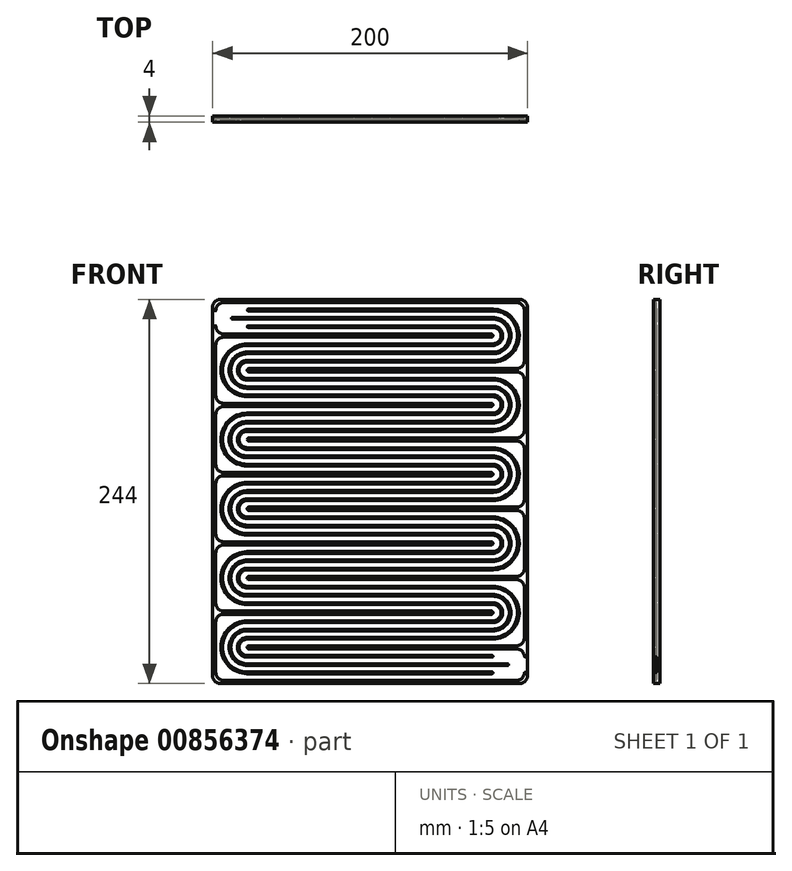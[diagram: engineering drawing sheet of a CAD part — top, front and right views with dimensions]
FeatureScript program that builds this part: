
annotation { "Feature Type Name" : "Feature", "Feature Type Description" : "" }
export const myFeature = defineFeature(function(context is Context, id is Id, definition is map)
    precondition{}
    {
        {
            var Q0;
            Q0=qCreatedBy(makeId("Front.planeOp"),FACE);
            var sketch = newSketch(context, id + "F0", { "sketchPlane" : qUnion([Q0])});
            skLineSegment(sketch, "E0.bottom", {"start": v(5, 0) * mm, "end": v(195, 0) * mm});
            skLineSegment(sketch, "E0.top", {"start": v(5, 244) * mm, "end": v(195, 244) * mm});
            skLineSegment(sketch, "E0.left", {"start": v(0, 5) * mm, "end": v(0, 239) * mm});
            skLineSegment(sketch, "E0.right", {"start": v(200, 5) * mm, "end": v(200, 239) * mm});
            skPoint(sketch, "E1.visualSharp", {"position": v(0, 244) * mm});
            skArc(sketch, "E1.filletArc", {"start": v(5, 244) * mm, "mid": v(1.46, 242.54) * mm, "end": v(0, 239) * mm});
            skPoint(sketch, "E2.visualSharp", {"position": v(200, 244) * mm});
            skArc(sketch, "E2.filletArc", {"start": v(200, 239) * mm, "mid": v(198.54, 242.54) * mm, "end": v(195, 244) * mm});
            skPoint(sketch, "E3.visualSharp", {"position": v(200, 0) * mm});
            skArc(sketch, "E3.filletArc", {"start": v(195, 0) * mm, "mid": v(198.54, 1.46) * mm, "end": v(200, 5) * mm});
            skPoint(sketch, "E4.visualSharp", {"position": v(0, 0) * mm});
            skArc(sketch, "E4.filletArc", {"start": v(0, 5) * mm, "mid": v(1.46, 1.46) * mm, "end": v(5, 0) * mm});
            skSolve(sketch);
        }
        {
            var Q0;
            Q0 = qSketchRegion(id + "F0", true);
            extrude(context, id + "F1", {"entities" : qUnion([Q0]), "depth" : 4 * mm, "offsetDistance" : 25 * mm});
        }
        {
            var Q0;
            Q0=makeQuery(id+"F1.opExtrude","CAP_FACE",FACE,{"disambiguationData":[OSD([sQuery(id+"F0.wireOp",EDGE,"E0.bottom"),sQuery(id+"F0.wireOp",EDGE,"E0.top"),sQuery(id+"F0.wireOp",EDGE,"E0.left"),sQuery(id+"F0.wireOp",EDGE,"E0.right"),sQuery(id+"F0.wireOp",EDGE,"E1.filletArc"),sQuery(id+"F0.wireOp",EDGE,"E2.filletArc"),sQuery(id+"F0.wireOp",EDGE,"E3.filletArc"),sQuery(id+"F0.wireOp",EDGE,"E4.filletArc")])],"isStart":false});
            var sketch = newSketch(context, id + "F2", { "sketchPlane" : qUnion([Q0])});
            skLineSegment(sketch, "E5.bottom", {"start": v(7, 242) * mm, "end": v(193, 242) * mm});
            skLineSegment(sketch, "E5.top", {"start": v(7, 2) * mm, "end": v(193, 2) * mm});
            skLineSegment(sketch, "E5.right", {"start": v(198, 237) * mm, "end": v(198, 205) * mm});
            skPoint(sketch, "E6.visualSharp", {"position": v(2, 242) * mm});
            skArc(sketch, "E6.filletArc", {"start": v(7, 242) * mm, "mid": v(3.46, 240.54) * mm, "end": v(2, 237) * mm});
            skPoint(sketch, "E7.visualSharp", {"position": v(198, 242) * mm});
            skArc(sketch, "E7.filletArc", {"start": v(198, 237) * mm, "mid": v(196.54, 240.54) * mm, "end": v(193, 242) * mm});
            skLineSegment(sketch, "E8.bottom", {"start": v(7, 46) * mm, "end": v(177, 46) * mm});
            skLineSegment(sketch, "E8.top", {"start": v(6.8, 44) * mm, "end": v(177, 44) * mm});
            skLineSegment(sketch, "E8.right", {"start": v(178, 45) * mm, "end": v(178, 45) * mm});
            skLineSegment(sketch, "E9.bottom", {"start": v(193, 24) * mm, "end": v(23, 24) * mm});
            skLineSegment(sketch, "E9.top", {"start": v(193, 22) * mm, "end": v(23, 22) * mm});
            skLineSegment(sketch, "E9.right", {"start": v(22, 23) * mm, "end": v(22, 23) * mm});
            skPoint(sketch, "E10.visualSharp", {"position": v(178, 46) * mm});
            skArc(sketch, "E10.filletArc", {"start": v(178, 45) * mm, "mid": v(177.7, 45.7) * mm, "end": v(177, 46) * mm});
            skPoint(sketch, "E11.visualSharp", {"position": v(178, 44) * mm});
            skArc(sketch, "E11.filletArc", {"start": v(177, 44) * mm, "mid": v(177.7, 44.3) * mm, "end": v(178, 45) * mm});
            skPoint(sketch, "E12.visualSharp", {"position": v(22, 24) * mm});
            skArc(sketch, "E12.filletArc", {"start": v(23, 24) * mm, "mid": v(22.3, 23.7) * mm, "end": v(22, 23) * mm});
            skPoint(sketch, "E13.visualSharp", {"position": v(22, 22) * mm});
            skArc(sketch, "E13.filletArc", {"start": v(22, 23) * mm, "mid": v(22.3, 22.3) * mm, "end": v(23, 22) * mm});
            skLineSegment(sketch, "E14.0.1.0", {"start": v(7, 88) * mm, "end": v(177, 88) * mm});
            skLineSegment(sketch, "E14.0.1.1", {"start": v(193, 68) * mm, "end": v(23, 68) * mm});
            skPoint(sketch, "E14.0.1.2", {"position": v(22, 68) * mm});
            skLineSegment(sketch, "E14.0.1.3", {"start": v(193, 66) * mm, "end": v(23, 66) * mm});
            skLineSegment(sketch, "E14.0.1.4", {"start": v(7, 90) * mm, "end": v(177, 90) * mm});
            skPoint(sketch, "E14.0.1.5", {"position": v(178, 90) * mm});
            skPoint(sketch, "E14.0.1.6", {"position": v(22, 66) * mm});
            skPoint(sketch, "E14.0.1.7", {"position": v(178, 88) * mm});
            skArc(sketch, "E14.0.1.10", {"start": v(22, 67) * mm, "mid": v(22.3, 66.3) * mm, "end": v(23, 66) * mm});
            skArc(sketch, "E14.0.1.11", {"start": v(23, 68) * mm, "mid": v(22.3, 67.7) * mm, "end": v(22, 67) * mm});
            skArc(sketch, "E14.0.1.12", {"start": v(177, 88) * mm, "mid": v(177.7, 88.3) * mm, "end": v(178, 89) * mm});
            skArc(sketch, "E14.0.1.13", {"start": v(178, 89) * mm, "mid": v(177.7, 89.7) * mm, "end": v(177, 90) * mm});
            skLineSegment(sketch, "E14.0.2.0", {"start": v(7, 132) * mm, "end": v(177, 132) * mm});
            skLineSegment(sketch, "E14.0.2.1", {"start": v(193, 112) * mm, "end": v(23, 112) * mm});
            skPoint(sketch, "E14.0.2.2", {"position": v(22, 112) * mm});
            skLineSegment(sketch, "E14.0.2.3", {"start": v(193, 110) * mm, "end": v(23, 110) * mm});
            skLineSegment(sketch, "E14.0.2.4", {"start": v(7, 134) * mm, "end": v(177, 134) * mm});
            skPoint(sketch, "E14.0.2.5", {"position": v(178, 134) * mm});
            skPoint(sketch, "E14.0.2.6", {"position": v(22, 110) * mm});
            skPoint(sketch, "E14.0.2.7", {"position": v(178, 132) * mm});
            skArc(sketch, "E14.0.2.10", {"start": v(22, 111) * mm, "mid": v(22.3, 110.3) * mm, "end": v(23, 110) * mm});
            skArc(sketch, "E14.0.2.11", {"start": v(23, 112) * mm, "mid": v(22.3, 111.7) * mm, "end": v(22, 111) * mm});
            skArc(sketch, "E14.0.2.12", {"start": v(177, 132) * mm, "mid": v(177.7, 132.3) * mm, "end": v(178, 133) * mm});
            skArc(sketch, "E14.0.2.13", {"start": v(178, 133) * mm, "mid": v(177.7, 133.7) * mm, "end": v(177, 134) * mm});
            skLineSegment(sketch, "E14.0.3.0", {"start": v(7, 176) * mm, "end": v(177, 176) * mm});
            skLineSegment(sketch, "E14.0.3.1", {"start": v(193, 156) * mm, "end": v(23, 156) * mm});
            skPoint(sketch, "E14.0.3.2", {"position": v(22, 156) * mm});
            skLineSegment(sketch, "E14.0.3.3", {"start": v(193, 154) * mm, "end": v(23, 154) * mm});
            skLineSegment(sketch, "E14.0.3.4", {"start": v(7, 178) * mm, "end": v(177, 178) * mm});
            skPoint(sketch, "E14.0.3.5", {"position": v(178, 178) * mm});
            skPoint(sketch, "E14.0.3.6", {"position": v(22, 154) * mm});
            skPoint(sketch, "E14.0.3.7", {"position": v(178, 176) * mm});
            skArc(sketch, "E14.0.3.10", {"start": v(22, 155) * mm, "mid": v(22.3, 154.3) * mm, "end": v(23, 154) * mm});
            skArc(sketch, "E14.0.3.11", {"start": v(23, 156) * mm, "mid": v(22.3, 155.7) * mm, "end": v(22, 155) * mm});
            skArc(sketch, "E14.0.3.12", {"start": v(177, 176) * mm, "mid": v(177.7, 176.3) * mm, "end": v(178, 177) * mm});
            skArc(sketch, "E14.0.3.13", {"start": v(178, 177) * mm, "mid": v(177.7, 177.7) * mm, "end": v(177, 178) * mm});
            skLineSegment(sketch, "E14.0.4.0", {"start": v(7, 220) * mm, "end": v(177, 220) * mm});
            skLineSegment(sketch, "E14.0.4.1", {"start": v(193, 200) * mm, "end": v(23, 200) * mm});
            skPoint(sketch, "E14.0.4.2", {"position": v(22, 200) * mm});
            skLineSegment(sketch, "E14.0.4.3", {"start": v(193, 198) * mm, "end": v(23, 198) * mm});
            skLineSegment(sketch, "E14.0.4.4", {"start": v(7, 222) * mm, "end": v(177, 222) * mm});
            skPoint(sketch, "E14.0.4.5", {"position": v(178, 222) * mm});
            skPoint(sketch, "E14.0.4.6", {"position": v(22, 198) * mm});
            skPoint(sketch, "E14.0.4.7", {"position": v(178, 220) * mm});
            skArc(sketch, "E14.0.4.10", {"start": v(22, 199) * mm, "mid": v(22.3, 198.3) * mm, "end": v(23, 198) * mm});
            skArc(sketch, "E14.0.4.11", {"start": v(23, 200) * mm, "mid": v(22.3, 199.7) * mm, "end": v(22, 199) * mm});
            skArc(sketch, "E14.0.4.12", {"start": v(177, 220) * mm, "mid": v(177.7, 220.3) * mm, "end": v(178, 221) * mm});
            skArc(sketch, "E14.0.4.13", {"start": v(178, 221) * mm, "mid": v(177.7, 221.7) * mm, "end": v(177, 222) * mm});
            skLineSegment(sketch, "E14.direction1", {"start": v(22, 22) * mm, "end": v(47, 22) * mm, "construction": true});
            skLineSegment(sketch, "E14.direction2", {"start": v(22, 22) * mm, "end": v(22, 66) * mm, "construction": true});
            skLineSegment(sketch, "E15.trimOffspring", {"start": v(2, 215) * mm, "end": v(2, 183) * mm});
            skLineSegment(sketch, "E16.trimOffspring", {"start": v(2, 171) * mm, "end": v(2, 139) * mm});
            skLineSegment(sketch, "E17.trimOffspring", {"start": v(2, 127) * mm, "end": v(2, 95) * mm});
            skLineSegment(sketch, "E18.trimOffspring", {"start": v(2, 83) * mm, "end": v(2, 51) * mm});
            skLineSegment(sketch, "E19.trimOffspring", {"start": v(2, 39.2) * mm, "end": v(2, 7) * mm});
            skLineSegment(sketch, "E20", {"start": v(2, 227) * mm, "end": v(2, 227) * mm});
            skLineSegment(sketch, "E21.trimOffspring", {"start": v(198, 17) * mm, "end": v(198, 17) * mm});
            skLineSegment(sketch, "E22.trimOffspring", {"start": v(198, 61) * mm, "end": v(198, 29) * mm});
            skLineSegment(sketch, "E23.trimOffspring", {"start": v(198, 193) * mm, "end": v(198, 161) * mm});
            skLineSegment(sketch, "E24.trimOffspring", {"start": v(198, 149) * mm, "end": v(198, 117) * mm});
            skPoint(sketch, "E25.visualSharp", {"position": v(2, 2) * mm});
            skArc(sketch, "E25.filletArc", {"start": v(2, 7) * mm, "mid": v(3.46, 3.46) * mm, "end": v(7, 2) * mm});
            skPoint(sketch, "E26.visualSharp", {"position": v(198, 2) * mm});
            skArc(sketch, "E26.filletArc", {"start": v(193, 2) * mm, "mid": v(196.54, 3.46) * mm, "end": v(198, 7) * mm});
            skLineSegment(sketch, "E27.trimOffspring", {"start": v(198, 105) * mm, "end": v(198, 73) * mm});
            skLineSegment(sketch, "E28", {"start": v(2, 237) * mm, "end": v(0, 237) * mm});
            skLineSegment(sketch, "E29", {"start": v(2, 227) * mm, "end": v(0, 227) * mm});
            skLineSegment(sketch, "E30", {"start": v(198, 7) * mm, "end": v(200, 7) * mm});
            skLineSegment(sketch, "E31", {"start": v(198, 17) * mm, "end": v(200, 17) * mm});
            skLineSegment(sketch, "E32", {"start": v(200, 17) * mm, "end": v(200, 7) * mm});
            skLineSegment(sketch, "E33", {"start": v(0, 237) * mm, "end": v(0, 227) * mm});
            skPoint(sketch, "E34.visualSharp", {"position": v(2, 222) * mm});
            skArc(sketch, "E34.filletArc", {"start": v(2, 227) * mm, "mid": v(3.46, 223.46) * mm, "end": v(7, 222) * mm});
            skPoint(sketch, "E35.visualSharp", {"position": v(2, 220) * mm});
            skArc(sketch, "E35.filletArc", {"start": v(7, 220) * mm, "mid": v(3.46, 218.54) * mm, "end": v(2, 215) * mm});
            skPoint(sketch, "E36.visualSharp", {"position": v(2, 178) * mm});
            skArc(sketch, "E36.filletArc", {"start": v(2, 183) * mm, "mid": v(3.46, 179.46) * mm, "end": v(7, 178) * mm});
            skPoint(sketch, "E37.visualSharp", {"position": v(2, 176) * mm});
            skArc(sketch, "E37.filletArc", {"start": v(7, 176) * mm, "mid": v(3.46, 174.54) * mm, "end": v(2, 171) * mm});
            skPoint(sketch, "E38.visualSharp", {"position": v(2, 134) * mm});
            skArc(sketch, "E38.filletArc", {"start": v(2, 139) * mm, "mid": v(3.46, 135.46) * mm, "end": v(7, 134) * mm});
            skPoint(sketch, "E39.visualSharp", {"position": v(2, 132) * mm});
            skArc(sketch, "E39.filletArc", {"start": v(7, 132) * mm, "mid": v(3.46, 130.54) * mm, "end": v(2, 127) * mm});
            skPoint(sketch, "E40.visualSharp", {"position": v(2, 90) * mm});
            skArc(sketch, "E40.filletArc", {"start": v(2, 95) * mm, "mid": v(3.46, 91.46) * mm, "end": v(7, 90) * mm});
            skPoint(sketch, "E41.visualSharp", {"position": v(198, 200) * mm});
            skArc(sketch, "E41.filletArc", {"start": v(193, 200) * mm, "mid": v(196.54, 201.46) * mm, "end": v(198, 205) * mm});
            skPoint(sketch, "E42.visualSharp", {"position": v(198, 198) * mm});
            skArc(sketch, "E42.filletArc", {"start": v(198, 193) * mm, "mid": v(196.54, 196.54) * mm, "end": v(193, 198) * mm});
            skPoint(sketch, "E43.visualSharp", {"position": v(198, 156) * mm});
            skArc(sketch, "E43.filletArc", {"start": v(193, 156) * mm, "mid": v(196.54, 157.46) * mm, "end": v(198, 161) * mm});
            skPoint(sketch, "E44.visualSharp", {"position": v(198, 112) * mm});
            skArc(sketch, "E44.filletArc", {"start": v(193, 112) * mm, "mid": v(196.54, 113.46) * mm, "end": v(198, 117) * mm});
            skPoint(sketch, "E45.visualSharp", {"position": v(198, 154) * mm});
            skArc(sketch, "E45.filletArc", {"start": v(198, 149) * mm, "mid": v(196.54, 152.54) * mm, "end": v(193, 154) * mm});
            skPoint(sketch, "E46.visualSharp", {"position": v(198, 110) * mm});
            skArc(sketch, "E46.filletArc", {"start": v(198, 105) * mm, "mid": v(196.54, 108.54) * mm, "end": v(193, 110) * mm});
            skPoint(sketch, "E47.visualSharp", {"position": v(198, 68) * mm});
            skArc(sketch, "E47.filletArc", {"start": v(193, 68) * mm, "mid": v(196.54, 69.46) * mm, "end": v(198, 73) * mm});
            skPoint(sketch, "E48.visualSharp", {"position": v(198, 24) * mm});
            skArc(sketch, "E48.filletArc", {"start": v(193, 24) * mm, "mid": v(196.54, 25.46) * mm, "end": v(198, 29) * mm});
            skPoint(sketch, "E49.visualSharp", {"position": v(2, 88) * mm});
            skArc(sketch, "E49.filletArc", {"start": v(7, 88) * mm, "mid": v(3.46, 86.54) * mm, "end": v(2, 83) * mm});
            skPoint(sketch, "E50.visualSharp", {"position": v(2, 46) * mm});
            skArc(sketch, "E50.filletArc", {"start": v(2, 51) * mm, "mid": v(3.46, 47.46) * mm, "end": v(7, 46) * mm});
            skPoint(sketch, "E51.visualSharp", {"position": v(2, 44) * mm});
            skArc(sketch, "E51.filletArc", {"start": v(6.8, 44) * mm, "mid": v(3.4, 42.6) * mm, "end": v(2, 39.2) * mm});
            skPoint(sketch, "E52.visualSharp", {"position": v(198, 66) * mm});
            skArc(sketch, "E52.filletArc", {"start": v(198, 61) * mm, "mid": v(196.54, 64.54) * mm, "end": v(193, 66) * mm});
            skPoint(sketch, "E53.visualSharp", {"position": v(198, 22) * mm});
            skArc(sketch, "E53.filletArc", {"start": v(198, 17) * mm, "mid": v(196.54, 20.54) * mm, "end": v(193, 22) * mm});
            skSolve(sketch);
        }
        {
            var Q0;
            Q0 = qSketchRegion(id + "F2", true);
            extrude(context, id + "F3", {"entities" : qUnion([Q0]), "operationType" : NewBodyOperationType.REMOVE, "oppositeDirection" : true, "depth" : 2 * mm, "offsetDistance" : 25 * mm});
        }
        {
            var Q0;
            Q0=makeQuery(id+"F3.boolean.opBoolean","COPY",FACE,{"derivedFrom":makeQuery(id+"F3.opExtrude","CAP_FACE",FACE,{"disambiguationData":[OSD([sQuery(id+"F2.wireOp",EDGE,"E5.bottom"),sQuery(id+"F2.wireOp",EDGE,"E5.top"),sQuery(id+"F2.wireOp",EDGE,"E5.right"),sQuery(id+"F2.wireOp",EDGE,"E6.filletArc"),sQuery(id+"F2.wireOp",EDGE,"E7.filletArc"),sQuery(id+"F2.wireOp",EDGE,"E8.bottom"),sQuery(id+"F2.wireOp",EDGE,"E8.top"),sQuery(id+"F2.wireOp",EDGE,"E9.bottom"),sQuery(id+"F2.wireOp",EDGE,"E9.top"),sQuery(id+"F2.wireOp",EDGE,"E10.filletArc"),sQuery(id+"F2.wireOp",EDGE,"E11.filletArc"),sQuery(id+"F2.wireOp",EDGE,"E12.filletArc"),sQuery(id+"F2.wireOp",EDGE,"E13.filletArc"),sQuery(id+"F2.wireOp",EDGE,"E14.0.1.0"),sQuery(id+"F2.wireOp",EDGE,"E14.0.1.1"),sQuery(id+"F2.wireOp",EDGE,"E14.0.1.3"),sQuery(id+"F2.wireOp",EDGE,"E14.0.1.4"),sQuery(id+"F2.wireOp",EDGE,"E14.0.1.10"),sQuery(id+"F2.wireOp",EDGE,"E14.0.1.11"),sQuery(id+"F2.wireOp",EDGE,"E14.0.1.12"),sQuery(id+"F2.wireOp",EDGE,"E14.0.1.13"),sQuery(id+"F2.wireOp",EDGE,"E14.0.2.0"),sQuery(id+"F2.wireOp",EDGE,"E14.0.2.1"),sQuery(id+"F2.wireOp",EDGE,"E14.0.2.3"),sQuery(id+"F2.wireOp",EDGE,"E14.0.2.4"),sQuery(id+"F2.wireOp",EDGE,"E14.0.2.10"),sQuery(id+"F2.wireOp",EDGE,"E14.0.2.11"),sQuery(id+"F2.wireOp",EDGE,"E14.0.2.12"),sQuery(id+"F2.wireOp",EDGE,"E14.0.2.13"),sQuery(id+"F2.wireOp",EDGE,"E14.0.3.0"),sQuery(id+"F2.wireOp",EDGE,"E14.0.3.1"),sQuery(id+"F2.wireOp",EDGE,"E14.0.3.3"),sQuery(id+"F2.wireOp",EDGE,"E14.0.3.4"),sQuery(id+"F2.wireOp",EDGE,"E14.0.3.10"),sQuery(id+"F2.wireOp",EDGE,"E14.0.3.11"),sQuery(id+"F2.wireOp",EDGE,"E14.0.3.12"),sQuery(id+"F2.wireOp",EDGE,"E14.0.3.13"),sQuery(id+"F2.wireOp",EDGE,"E14.0.4.0"),sQuery(id+"F2.wireOp",EDGE,"E14.0.4.1"),sQuery(id+"F2.wireOp",EDGE,"E14.0.4.3"),sQuery(id+"F2.wireOp",EDGE,"E14.0.4.4"),sQuery(id+"F2.wireOp",EDGE,"E14.0.4.10"),sQuery(id+"F2.wireOp",EDGE,"E14.0.4.11"),sQuery(id+"F2.wireOp",EDGE,"E14.0.4.12"),sQuery(id+"F2.wireOp",EDGE,"E14.0.4.13"),sQuery(id+"F2.wireOp",EDGE,"E15.trimOffspring"),sQuery(id+"F2.wireOp",EDGE,"E16.trimOffspring"),sQuery(id+"F2.wireOp",EDGE,"E17.trimOffspring"),sQuery(id+"F2.wireOp",EDGE,"E18.trimOffspring"),sQuery(id+"F2.wireOp",EDGE,"E19.trimOffspring"),sQuery(id+"F2.wireOp",EDGE,"E22.trimOffspring"),sQuery(id+"F2.wireOp",EDGE,"E23.trimOffspring"),sQuery(id+"F2.wireOp",EDGE,"E24.trimOffspring"),sQuery(id+"F2.wireOp",EDGE,"E25.filletArc"),sQuery(id+"F2.wireOp",EDGE,"E26.filletArc"),sQuery(id+"F2.wireOp",EDGE,"E27.trimOffspring"),sQuery(id+"F2.wireOp",EDGE,"E28"),sQuery(id+"F2.wireOp",EDGE,"E29"),sQuery(id+"F2.wireOp",EDGE,"E30"),sQuery(id+"F2.wireOp",EDGE,"E31"),sQuery(id+"F2.wireOp",EDGE,"E32"),sQuery(id+"F2.wireOp",EDGE,"E33"),sQuery(id+"F2.wireOp",EDGE,"E34.filletArc"),sQuery(id+"F2.wireOp",EDGE,"E35.filletArc"),sQuery(id+"F2.wireOp",EDGE,"E36.filletArc"),sQuery(id+"F2.wireOp",EDGE,"E37.filletArc"),sQuery(id+"F2.wireOp",EDGE,"E38.filletArc"),sQuery(id+"F2.wireOp",EDGE,"E39.filletArc"),sQuery(id+"F2.wireOp",EDGE,"E40.filletArc"),sQuery(id+"F2.wireOp",EDGE,"E41.filletArc"),sQuery(id+"F2.wireOp",EDGE,"E42.filletArc"),sQuery(id+"F2.wireOp",EDGE,"E43.filletArc"),sQuery(id+"F2.wireOp",EDGE,"E44.filletArc"),sQuery(id+"F2.wireOp",EDGE,"E45.filletArc"),sQuery(id+"F2.wireOp",EDGE,"E46.filletArc"),sQuery(id+"F2.wireOp",EDGE,"E47.filletArc"),sQuery(id+"F2.wireOp",EDGE,"E48.filletArc"),sQuery(id+"F2.wireOp",EDGE,"E49.filletArc"),sQuery(id+"F2.wireOp",EDGE,"E50.filletArc"),sQuery(id+"F2.wireOp",EDGE,"E51.filletArc"),sQuery(id+"F2.wireOp",EDGE,"E52.filletArc"),sQuery(id+"F2.wireOp",EDGE,"E53.filletArc")])],"isStart":false})});
            var sketch = newSketch(context, id + "F4", { "sketchPlane" : qUnion([Q0])});
            skLineSegment(sketch, "E54.bottom", {"start": v(22, 7.25) * mm, "end": v(178, 7.25) * mm});
            skLineSegment(sketch, "E54.top", {"start": v(22, 6.25) * mm, "end": v(178, 6.25) * mm});
            skLineSegment(sketch, "E54.left", {"start": v(22, 7.25) * mm, "end": v(22, 6.25) * mm});
            skLineSegment(sketch, "E54.right", {"start": v(178, 7.25) * mm, "end": v(178, 6.25) * mm});
            skLineSegment(sketch, "E55.0.1.0", {"start": v(22, 12.5) * mm, "end": v(178, 12.5) * mm});
            skLineSegment(sketch, "E55.0.1.1", {"start": v(22, 11.5) * mm, "end": v(178, 11.5) * mm});
            skLineSegment(sketch, "E55.0.1.3", {"start": v(22, 12.5) * mm, "end": v(22, 11.5) * mm});
            skLineSegment(sketch, "E55.0.2.0", {"start": v(22, 17.75) * mm, "end": v(178, 17.75) * mm});
            skLineSegment(sketch, "E55.0.2.1", {"start": v(22, 16.75) * mm, "end": v(178, 16.75) * mm});
            skLineSegment(sketch, "E55.0.2.2", {"start": v(178, 17.75) * mm, "end": v(178, 16.75) * mm});
            skLineSegment(sketch, "E55.0.2.3", {"start": v(22, 17.75) * mm, "end": v(22, 16.75) * mm});
            skLineSegment(sketch, "E55.direction1", {"start": v(22, 6.25) * mm, "end": v(47, 6.25) * mm, "construction": true});
            skLineSegment(sketch, "E56.0.1.0", {"start": v(22, 38.75) * mm, "end": v(178, 38.75) * mm});
            skLineSegment(sketch, "E56.0.1.1", {"start": v(22, 29.25) * mm, "end": v(178, 29.25) * mm});
            skLineSegment(sketch, "E56.0.1.2", {"start": v(22, 34.5) * mm, "end": v(178, 34.5) * mm});
            skLineSegment(sketch, "E56.0.1.3", {"start": v(22, 28.25) * mm, "end": v(178, 28.25) * mm});
            skLineSegment(sketch, "E56.0.1.4", {"start": v(22, 39.75) * mm, "end": v(178, 39.75) * mm});
            skLineSegment(sketch, "E56.0.1.5", {"start": v(22, 33.5) * mm, "end": v(178, 33.5) * mm});
            skLineSegment(sketch, "E56.0.1.6", {"start": v(22, 28.25) * mm, "end": v(47, 28.25) * mm, "construction": true});
            skLineSegment(sketch, "E56.0.1.9", {"start": v(22, 29.25) * mm, "end": v(22, 33.5) * mm, "construction": true});
            skLineSegment(sketch, "E56.0.1.13", {"start": v(22, 29.25) * mm, "end": v(22, 28.25) * mm});
            skLineSegment(sketch, "E56.0.2.0", {"start": v(22, 60.75) * mm, "end": v(178, 60.75) * mm});
            skLineSegment(sketch, "E56.0.2.1", {"start": v(22, 51.25) * mm, "end": v(178, 51.25) * mm});
            skLineSegment(sketch, "E56.0.2.2", {"start": v(22, 56.5) * mm, "end": v(178, 56.5) * mm});
            skLineSegment(sketch, "E56.0.2.3", {"start": v(22, 50.25) * mm, "end": v(178, 50.25) * mm});
            skLineSegment(sketch, "E56.0.2.4", {"start": v(22, 61.75) * mm, "end": v(178, 61.75) * mm});
            skLineSegment(sketch, "E56.0.2.5", {"start": v(22, 55.5) * mm, "end": v(178, 55.5) * mm});
            skLineSegment(sketch, "E56.0.2.6", {"start": v(22, 50.25) * mm, "end": v(47, 50.25) * mm, "construction": true});
            skLineSegment(sketch, "E56.0.2.7", {"start": v(22, 61.75) * mm, "end": v(22, 60.75) * mm});
            skLineSegment(sketch, "E56.0.2.9", {"start": v(22, 50.25) * mm, "end": v(22, 55.5) * mm, "construction": true});
            skLineSegment(sketch, "E56.0.2.12", {"start": v(22, 56.5) * mm, "end": v(22, 55.5) * mm});
            skLineSegment(sketch, "E56.0.2.13", {"start": v(22, 51.25) * mm, "end": v(22, 50.25) * mm});
            skLineSegment(sketch, "E56.0.3.0", {"start": v(22, 82.75) * mm, "end": v(178, 82.75) * mm});
            skLineSegment(sketch, "E56.0.3.1", {"start": v(22, 73.25) * mm, "end": v(178, 73.25) * mm});
            skLineSegment(sketch, "E56.0.3.2", {"start": v(22, 78.5) * mm, "end": v(178, 78.5) * mm});
            skLineSegment(sketch, "E56.0.3.3", {"start": v(22, 72.25) * mm, "end": v(178, 72.25) * mm});
            skLineSegment(sketch, "E56.0.3.4", {"start": v(22, 83.75) * mm, "end": v(178, 83.75) * mm});
            skLineSegment(sketch, "E56.0.3.5", {"start": v(22, 77.5) * mm, "end": v(178, 77.5) * mm});
            skLineSegment(sketch, "E56.0.3.6", {"start": v(22, 72.25) * mm, "end": v(47, 72.25) * mm, "construction": true});
            skLineSegment(sketch, "E56.0.3.7", {"start": v(22, 83.75) * mm, "end": v(22, 82.75) * mm});
            skLineSegment(sketch, "E56.0.3.8", {"start": v(178, 83.75) * mm, "end": v(178, 82.75) * mm});
            skLineSegment(sketch, "E56.0.3.9", {"start": v(22, 72.25) * mm, "end": v(22, 77.5) * mm, "construction": true});
            skLineSegment(sketch, "E56.0.3.10", {"start": v(178, 78.5) * mm, "end": v(178, 77.5) * mm});
            skLineSegment(sketch, "E56.0.3.11", {"start": v(178, 73.25) * mm, "end": v(178, 72.25) * mm});
            skLineSegment(sketch, "E56.0.3.12", {"start": v(22, 78.5) * mm, "end": v(22, 77.5) * mm});
            skLineSegment(sketch, "E56.0.3.13", {"start": v(22, 73.25) * mm, "end": v(22, 72.25) * mm});
            skLineSegment(sketch, "E56.0.4.0", {"start": v(22, 104.75) * mm, "end": v(178, 104.75) * mm});
            skLineSegment(sketch, "E56.0.4.1", {"start": v(22, 95.25) * mm, "end": v(178, 95.25) * mm});
            skLineSegment(sketch, "E56.0.4.2", {"start": v(22, 100.5) * mm, "end": v(178, 100.5) * mm});
            skLineSegment(sketch, "E56.0.4.3", {"start": v(22, 94.25) * mm, "end": v(178, 94.25) * mm});
            skLineSegment(sketch, "E56.0.4.4", {"start": v(22, 105.75) * mm, "end": v(178, 105.75) * mm});
            skLineSegment(sketch, "E56.0.4.5", {"start": v(22, 99.5) * mm, "end": v(178, 99.5) * mm});
            skLineSegment(sketch, "E56.0.4.6", {"start": v(22, 94.25) * mm, "end": v(47, 94.25) * mm, "construction": true});
            skLineSegment(sketch, "E56.0.4.7", {"start": v(22, 105.75) * mm, "end": v(22, 104.75) * mm});
            skLineSegment(sketch, "E56.0.4.8", {"start": v(178, 105.75) * mm, "end": v(178, 104.75) * mm});
            skLineSegment(sketch, "E56.0.4.9", {"start": v(22, 94.25) * mm, "end": v(22, 99.5) * mm, "construction": true});
            skLineSegment(sketch, "E56.0.4.10", {"start": v(178, 100.5) * mm, "end": v(178, 99.5) * mm});
            skLineSegment(sketch, "E56.0.4.11", {"start": v(178, 95.25) * mm, "end": v(178, 94.25) * mm});
            skLineSegment(sketch, "E56.0.4.12", {"start": v(22, 100.5) * mm, "end": v(22, 99.5) * mm});
            skLineSegment(sketch, "E56.0.4.13", {"start": v(22, 95.25) * mm, "end": v(22, 94.25) * mm});
            skLineSegment(sketch, "E56.0.5.0", {"start": v(22, 126.75) * mm, "end": v(178, 126.75) * mm});
            skLineSegment(sketch, "E56.0.5.1", {"start": v(22, 117.25) * mm, "end": v(178, 117.25) * mm});
            skLineSegment(sketch, "E56.0.5.2", {"start": v(22, 122.5) * mm, "end": v(178, 122.5) * mm});
            skLineSegment(sketch, "E56.0.5.3", {"start": v(22, 116.25) * mm, "end": v(178, 116.25) * mm});
            skLineSegment(sketch, "E56.0.5.4", {"start": v(22, 127.75) * mm, "end": v(178, 127.75) * mm});
            skLineSegment(sketch, "E56.0.5.5", {"start": v(22, 121.5) * mm, "end": v(178, 121.5) * mm});
            skLineSegment(sketch, "E56.0.5.6", {"start": v(22, 116.25) * mm, "end": v(47, 116.25) * mm, "construction": true});
            skLineSegment(sketch, "E56.0.5.7", {"start": v(22, 127.75) * mm, "end": v(22, 126.75) * mm});
            skLineSegment(sketch, "E56.0.5.8", {"start": v(178, 127.75) * mm, "end": v(178, 126.75) * mm});
            skLineSegment(sketch, "E56.0.5.9", {"start": v(22, 116.25) * mm, "end": v(22, 121.5) * mm, "construction": true});
            skLineSegment(sketch, "E56.0.5.10", {"start": v(178, 122.5) * mm, "end": v(178, 121.5) * mm});
            skLineSegment(sketch, "E56.0.5.11", {"start": v(178, 117.25) * mm, "end": v(178, 116.25) * mm});
            skLineSegment(sketch, "E56.0.5.12", {"start": v(22, 122.5) * mm, "end": v(22, 121.5) * mm});
            skLineSegment(sketch, "E56.0.5.13", {"start": v(22, 117.25) * mm, "end": v(22, 116.25) * mm});
            skLineSegment(sketch, "E56.0.6.0", {"start": v(22, 148.75) * mm, "end": v(178, 148.75) * mm});
            skLineSegment(sketch, "E56.0.6.1", {"start": v(22, 139.25) * mm, "end": v(178, 139.25) * mm});
            skLineSegment(sketch, "E56.0.6.2", {"start": v(22, 144.5) * mm, "end": v(178, 144.5) * mm});
            skLineSegment(sketch, "E56.0.6.3", {"start": v(22, 138.25) * mm, "end": v(178, 138.25) * mm});
            skLineSegment(sketch, "E56.0.6.4", {"start": v(22, 149.75) * mm, "end": v(178, 149.75) * mm});
            skLineSegment(sketch, "E56.0.6.5", {"start": v(22, 143.5) * mm, "end": v(178, 143.5) * mm});
            skLineSegment(sketch, "E56.0.6.6", {"start": v(22, 138.25) * mm, "end": v(47, 138.25) * mm, "construction": true});
            skLineSegment(sketch, "E56.0.6.7", {"start": v(22, 149.75) * mm, "end": v(22, 148.75) * mm});
            skLineSegment(sketch, "E56.0.6.8", {"start": v(178, 149.75) * mm, "end": v(178, 148.75) * mm});
            skLineSegment(sketch, "E56.0.6.9", {"start": v(22, 138.25) * mm, "end": v(22, 143.5) * mm, "construction": true});
            skLineSegment(sketch, "E56.0.6.10", {"start": v(178, 144.5) * mm, "end": v(178, 143.5) * mm});
            skLineSegment(sketch, "E56.0.6.11", {"start": v(178, 139.25) * mm, "end": v(178, 138.25) * mm});
            skLineSegment(sketch, "E56.0.6.12", {"start": v(22, 144.5) * mm, "end": v(22, 143.5) * mm});
            skLineSegment(sketch, "E56.0.6.13", {"start": v(22, 139.25) * mm, "end": v(22, 138.25) * mm});
            skLineSegment(sketch, "E56.0.7.0", {"start": v(22, 170.75) * mm, "end": v(178, 170.75) * mm});
            skLineSegment(sketch, "E56.0.7.1", {"start": v(22, 161.25) * mm, "end": v(178, 161.25) * mm});
            skLineSegment(sketch, "E56.0.7.2", {"start": v(22, 166.5) * mm, "end": v(178, 166.5) * mm});
            skLineSegment(sketch, "E56.0.7.3", {"start": v(22, 160.25) * mm, "end": v(178, 160.25) * mm});
            skLineSegment(sketch, "E56.0.7.4", {"start": v(22, 171.75) * mm, "end": v(178, 171.75) * mm});
            skLineSegment(sketch, "E56.0.7.5", {"start": v(22, 165.5) * mm, "end": v(178, 165.5) * mm});
            skLineSegment(sketch, "E56.0.7.6", {"start": v(22, 160.25) * mm, "end": v(47, 160.25) * mm, "construction": true});
            skLineSegment(sketch, "E56.0.7.7", {"start": v(22, 171.75) * mm, "end": v(22, 170.75) * mm});
            skLineSegment(sketch, "E56.0.7.8", {"start": v(178, 171.75) * mm, "end": v(178, 170.75) * mm});
            skLineSegment(sketch, "E56.0.7.9", {"start": v(22, 160.25) * mm, "end": v(22, 165.5) * mm, "construction": true});
            skLineSegment(sketch, "E56.0.7.10", {"start": v(178, 166.5) * mm, "end": v(178, 165.5) * mm});
            skLineSegment(sketch, "E56.0.7.11", {"start": v(178, 161.25) * mm, "end": v(178, 160.25) * mm});
            skLineSegment(sketch, "E56.0.7.12", {"start": v(22, 166.5) * mm, "end": v(22, 165.5) * mm});
            skLineSegment(sketch, "E56.0.7.13", {"start": v(22, 161.25) * mm, "end": v(22, 160.25) * mm});
            skLineSegment(sketch, "E56.0.8.0", {"start": v(22, 192.75) * mm, "end": v(178, 192.75) * mm});
            skLineSegment(sketch, "E56.0.8.1", {"start": v(22, 183.25) * mm, "end": v(178, 183.25) * mm});
            skLineSegment(sketch, "E56.0.8.2", {"start": v(22, 188.5) * mm, "end": v(178, 188.5) * mm});
            skLineSegment(sketch, "E56.0.8.3", {"start": v(22, 182.25) * mm, "end": v(178, 182.25) * mm});
            skLineSegment(sketch, "E56.0.8.4", {"start": v(22, 193.75) * mm, "end": v(178, 193.75) * mm});
            skLineSegment(sketch, "E56.0.8.5", {"start": v(22, 187.5) * mm, "end": v(178, 187.5) * mm});
            skLineSegment(sketch, "E56.0.8.6", {"start": v(22, 182.25) * mm, "end": v(47, 182.25) * mm, "construction": true});
            skLineSegment(sketch, "E56.0.8.7", {"start": v(22, 193.75) * mm, "end": v(22, 192.75) * mm});
            skLineSegment(sketch, "E56.0.8.8", {"start": v(178, 193.75) * mm, "end": v(178, 192.75) * mm});
            skLineSegment(sketch, "E56.0.8.9", {"start": v(22, 182.25) * mm, "end": v(22, 187.5) * mm, "construction": true});
            skLineSegment(sketch, "E56.0.8.10", {"start": v(178, 188.5) * mm, "end": v(178, 187.5) * mm});
            skLineSegment(sketch, "E56.0.8.11", {"start": v(178, 183.25) * mm, "end": v(178, 182.25) * mm});
            skLineSegment(sketch, "E56.0.8.12", {"start": v(22, 188.5) * mm, "end": v(22, 187.5) * mm});
            skLineSegment(sketch, "E56.0.8.13", {"start": v(22, 183.25) * mm, "end": v(22, 182.25) * mm});
            skLineSegment(sketch, "E56.0.9.0", {"start": v(22, 214.75) * mm, "end": v(178, 214.75) * mm});
            skLineSegment(sketch, "E56.0.9.1", {"start": v(22, 205.25) * mm, "end": v(178, 205.25) * mm});
            skLineSegment(sketch, "E56.0.9.2", {"start": v(22, 210.5) * mm, "end": v(178, 210.5) * mm});
            skLineSegment(sketch, "E56.0.9.3", {"start": v(22, 204.25) * mm, "end": v(178, 204.25) * mm});
            skLineSegment(sketch, "E56.0.9.4", {"start": v(22, 215.75) * mm, "end": v(178, 215.75) * mm});
            skLineSegment(sketch, "E56.0.9.5", {"start": v(22, 209.5) * mm, "end": v(178, 209.5) * mm});
            skLineSegment(sketch, "E56.0.9.6", {"start": v(22, 204.25) * mm, "end": v(47, 204.25) * mm, "construction": true});
            skLineSegment(sketch, "E56.0.9.7", {"start": v(22, 215.75) * mm, "end": v(22, 214.75) * mm});
            skLineSegment(sketch, "E56.0.9.8", {"start": v(178, 215.75) * mm, "end": v(178, 214.75) * mm});
            skLineSegment(sketch, "E56.0.9.9", {"start": v(22, 204.25) * mm, "end": v(22, 209.5) * mm, "construction": true});
            skLineSegment(sketch, "E56.0.9.10", {"start": v(178, 210.5) * mm, "end": v(178, 209.5) * mm});
            skLineSegment(sketch, "E56.0.9.11", {"start": v(178, 205.25) * mm, "end": v(178, 204.25) * mm});
            skLineSegment(sketch, "E56.0.9.12", {"start": v(22, 210.5) * mm, "end": v(22, 209.5) * mm});
            skLineSegment(sketch, "E56.0.9.13", {"start": v(22, 205.25) * mm, "end": v(22, 204.25) * mm});
            skLineSegment(sketch, "E56.0.10.0", {"start": v(22, 236.75) * mm, "end": v(178, 236.75) * mm});
            skLineSegment(sketch, "E56.0.10.1", {"start": v(22, 227.25) * mm, "end": v(178, 227.25) * mm});
            skLineSegment(sketch, "E56.0.10.2", {"start": v(22, 232.5) * mm, "end": v(178, 232.5) * mm});
            skLineSegment(sketch, "E56.0.10.3", {"start": v(22, 226.25) * mm, "end": v(178, 226.25) * mm});
            skLineSegment(sketch, "E56.0.10.4", {"start": v(22, 237.75) * mm, "end": v(178, 237.75) * mm});
            skLineSegment(sketch, "E56.0.10.5", {"start": v(22, 231.5) * mm, "end": v(178, 231.5) * mm});
            skLineSegment(sketch, "E56.0.10.6", {"start": v(22, 226.25) * mm, "end": v(47, 226.25) * mm, "construction": true});
            skLineSegment(sketch, "E56.0.10.7", {"start": v(22, 237.75) * mm, "end": v(22, 236.75) * mm});
            skLineSegment(sketch, "E56.0.10.8", {"start": v(178, 237.75) * mm, "end": v(178, 236.75) * mm});
            skLineSegment(sketch, "E56.0.10.10", {"start": v(178, 232.5) * mm, "end": v(178, 231.5) * mm});
            skLineSegment(sketch, "E56.0.10.11", {"start": v(178, 227.25) * mm, "end": v(178, 226.25) * mm});
            skLineSegment(sketch, "E56.0.10.13", {"start": v(22, 227.25) * mm, "end": v(22, 226.25) * mm});
            skLineSegment(sketch, "E56.direction2", {"start": v(22, 6.25) * mm, "end": v(22, 11.5) * mm, "construction": true});
            skLineSegment(sketch, "E57.trimOffspring", {"start": v(22, 23) * mm, "end": v(22.36, 23) * mm, "construction": true});
            skArc(sketch, "E58", {"start": v(22, 28.25) * mm, "mid": v(16.75, 23) * mm, "end": v(22, 17.75) * mm});
            skArc(sketch, "E59", {"start": v(22, 29.25) * mm, "mid": v(15.75, 23) * mm, "end": v(22, 16.75) * mm});
            skLineSegment(sketch, "E60.trimOffspring", {"start": v(22, 17.75) * mm, "end": v(22, 28.25) * mm, "construction": true});
            skArc(sketch, "E61", {"start": v(22, 33.5) * mm, "mid": v(11.5, 23) * mm, "end": v(22, 12.5) * mm});
            skArc(sketch, "E62", {"start": v(22, 34.5) * mm, "mid": v(10.5, 23) * mm, "end": v(22, 11.5) * mm});
            skArc(sketch, "E63", {"start": v(22, 38.75) * mm, "mid": v(6.25, 23) * mm, "end": v(22, 7.25) * mm});
            skArc(sketch, "E64", {"start": v(22, 39.75) * mm, "mid": v(5.27, 22.1) * mm, "end": v(23.8, 6.35) * mm});
            skLineSegment(sketch, "E65.trimOffspring", {"start": v(22, 12.5) * mm, "end": v(22, 16.75) * mm, "construction": true});
            skArc(sketch, "E66.0.1.0", {"start": v(22, 83.75) * mm, "mid": v(5.27, 66.1) * mm, "end": v(23.8, 50.35) * mm});
            skLineSegment(sketch, "E66.0.1.1", {"start": v(22, 73.25) * mm, "end": v(22, 77.5) * mm, "construction": true});
            skArc(sketch, "E66.0.1.2", {"start": v(22, 73.25) * mm, "mid": v(15.75, 67) * mm, "end": v(22, 60.75) * mm});
            skArc(sketch, "E66.0.1.3", {"start": v(22, 78.5) * mm, "mid": v(10.5, 67) * mm, "end": v(22, 55.5) * mm});
            skLineSegment(sketch, "E66.0.1.4", {"start": v(22, 61.75) * mm, "end": v(22, 72.25) * mm, "construction": true});
            skArc(sketch, "E66.0.1.5", {"start": v(22, 77.5) * mm, "mid": v(11.5, 67) * mm, "end": v(22, 56.5) * mm});
            skLineSegment(sketch, "E66.0.1.6", {"start": v(22, 56.5) * mm, "end": v(22, 60.75) * mm, "construction": true});
            skArc(sketch, "E66.0.1.8", {"start": v(22, 72.25) * mm, "mid": v(16.75, 67) * mm, "end": v(22, 61.75) * mm});
            skArc(sketch, "E66.0.1.9", {"start": v(22, 82.75) * mm, "mid": v(6.25, 67) * mm, "end": v(22, 51.25) * mm});
            skLineSegment(sketch, "E66.0.1.14", {"start": v(22, 67) * mm, "end": v(22.36, 67) * mm, "construction": true});
            skArc(sketch, "E66.0.2.0", {"start": v(22, 127.75) * mm, "mid": v(5.27, 110.1) * mm, "end": v(23.8, 94.35) * mm});
            skLineSegment(sketch, "E66.0.2.1", {"start": v(22, 117.25) * mm, "end": v(22, 121.5) * mm, "construction": true});
            skArc(sketch, "E66.0.2.2", {"start": v(22, 117.25) * mm, "mid": v(15.75, 111) * mm, "end": v(22, 104.75) * mm});
            skArc(sketch, "E66.0.2.3", {"start": v(22, 122.5) * mm, "mid": v(10.5, 111) * mm, "end": v(22, 99.5) * mm});
            skLineSegment(sketch, "E66.0.2.4", {"start": v(22, 105.75) * mm, "end": v(22, 116.25) * mm, "construction": true});
            skArc(sketch, "E66.0.2.5", {"start": v(22, 121.5) * mm, "mid": v(11.5, 111) * mm, "end": v(22, 100.5) * mm});
            skLineSegment(sketch, "E66.0.2.6", {"start": v(22, 100.5) * mm, "end": v(22, 104.75) * mm, "construction": true});
            skArc(sketch, "E66.0.2.8", {"start": v(22, 116.25) * mm, "mid": v(16.75, 111) * mm, "end": v(22, 105.75) * mm});
            skArc(sketch, "E66.0.2.9", {"start": v(22, 126.75) * mm, "mid": v(6.25, 111) * mm, "end": v(22, 95.25) * mm});
            skLineSegment(sketch, "E66.0.2.14", {"start": v(22, 111) * mm, "end": v(22.36, 111) * mm, "construction": true});
            skArc(sketch, "E66.0.3.0", {"start": v(22, 171.75) * mm, "mid": v(5.27, 154.1) * mm, "end": v(23.8, 138.35) * mm});
            skLineSegment(sketch, "E66.0.3.1", {"start": v(22, 161.25) * mm, "end": v(22, 165.5) * mm, "construction": true});
            skArc(sketch, "E66.0.3.2", {"start": v(22, 161.25) * mm, "mid": v(15.75, 155) * mm, "end": v(22, 148.75) * mm});
            skArc(sketch, "E66.0.3.3", {"start": v(22, 166.5) * mm, "mid": v(10.5, 155) * mm, "end": v(22, 143.5) * mm});
            skLineSegment(sketch, "E66.0.3.4", {"start": v(22, 149.75) * mm, "end": v(22, 160.25) * mm, "construction": true});
            skArc(sketch, "E66.0.3.5", {"start": v(22, 165.5) * mm, "mid": v(11.5, 155) * mm, "end": v(22, 144.5) * mm});
            skLineSegment(sketch, "E66.0.3.6", {"start": v(22, 144.5) * mm, "end": v(22, 148.75) * mm, "construction": true});
            skArc(sketch, "E66.0.3.8", {"start": v(22, 160.25) * mm, "mid": v(16.75, 155) * mm, "end": v(22, 149.75) * mm});
            skArc(sketch, "E66.0.3.9", {"start": v(22, 170.75) * mm, "mid": v(6.25, 155) * mm, "end": v(22, 139.25) * mm});
            skLineSegment(sketch, "E66.0.3.14", {"start": v(22, 155) * mm, "end": v(22.36, 155) * mm, "construction": true});
            skArc(sketch, "E66.0.4.0", {"start": v(22, 215.75) * mm, "mid": v(5.27, 198.1) * mm, "end": v(23.8, 182.35) * mm});
            skLineSegment(sketch, "E66.0.4.1", {"start": v(22, 205.25) * mm, "end": v(22, 209.5) * mm, "construction": true});
            skArc(sketch, "E66.0.4.2", {"start": v(22, 205.25) * mm, "mid": v(15.75, 199) * mm, "end": v(22, 192.75) * mm});
            skArc(sketch, "E66.0.4.3", {"start": v(22, 210.5) * mm, "mid": v(10.5, 199) * mm, "end": v(22, 187.5) * mm});
            skLineSegment(sketch, "E66.0.4.4", {"start": v(22, 193.75) * mm, "end": v(22, 204.25) * mm, "construction": true});
            skArc(sketch, "E66.0.4.5", {"start": v(22, 209.5) * mm, "mid": v(11.5, 199) * mm, "end": v(22, 188.5) * mm});
            skLineSegment(sketch, "E66.0.4.6", {"start": v(22, 188.5) * mm, "end": v(22, 192.75) * mm, "construction": true});
            skArc(sketch, "E66.0.4.8", {"start": v(22, 204.25) * mm, "mid": v(16.75, 199) * mm, "end": v(22, 193.75) * mm});
            skArc(sketch, "E66.0.4.9", {"start": v(22, 214.75) * mm, "mid": v(6.25, 199) * mm, "end": v(22, 183.25) * mm});
            skLineSegment(sketch, "E66.0.4.14", {"start": v(22, 199) * mm, "end": v(22.36, 199) * mm, "construction": true});
            skLineSegment(sketch, "E66.direction2", {"start": v(22, 6.25) * mm, "end": v(22, 50.25) * mm, "construction": true});
            skArc(sketch, "E67", {"start": v(178, 50.25) * mm, "mid": v(183.25, 45) * mm, "end": v(178, 39.75) * mm});
            skArc(sketch, "E68", {"start": v(178, 51.25) * mm, "mid": v(184.25, 45) * mm, "end": v(178, 38.75) * mm});
            skArc(sketch, "E69", {"start": v(178, 55.5) * mm, "mid": v(188.5, 45) * mm, "end": v(178, 34.5) * mm});
            skArc(sketch, "E70", {"start": v(178, 56.5) * mm, "mid": v(189.5, 45) * mm, "end": v(178, 33.5) * mm});
            skArc(sketch, "E71", {"start": v(178, 60.75) * mm, "mid": v(193.75, 45) * mm, "end": v(178, 29.25) * mm});
            skArc(sketch, "E72", {"start": v(178, 61.75) * mm, "mid": v(194.75, 45) * mm, "end": v(178, 28.25) * mm});
            skLineSegment(sketch, "E73.bottom", {"start": v(178, 12.5) * mm, "end": v(178, 12.5) * mm});
            skLineSegment(sketch, "E73.top", {"start": v(178, 11.5) * mm, "end": v(178, 11.5) * mm});
            skLineSegment(sketch, "E74.bottom", {"start": v(178, 12.5) * mm, "end": v(188, 12.5) * mm});
            skLineSegment(sketch, "E74.top", {"start": v(178, 11.5) * mm, "end": v(188, 11.5) * mm});
            skLineSegment(sketch, "E74.right", {"start": v(188, 12.5) * mm, "end": v(188, 11.5) * mm});
            skLineSegment(sketch, "E75.bottom", {"start": v(22, 232.5) * mm, "end": v(12, 232.5) * mm});
            skLineSegment(sketch, "E75.top", {"start": v(22, 231.5) * mm, "end": v(12, 231.5) * mm});
            skLineSegment(sketch, "E75.right", {"start": v(12, 232.5) * mm, "end": v(12, 231.5) * mm});
            skArc(sketch, "E76.0.1.0", {"start": v(178, 94.25) * mm, "mid": v(183.25, 89) * mm, "end": v(178, 83.75) * mm});
            skArc(sketch, "E76.0.1.1", {"start": v(178, 104.75) * mm, "mid": v(193.75, 89) * mm, "end": v(178, 73.25) * mm});
            skArc(sketch, "E76.0.1.2", {"start": v(178, 105.75) * mm, "mid": v(194.75, 89) * mm, "end": v(178, 72.25) * mm});
            skArc(sketch, "E76.0.1.3", {"start": v(178, 99.5) * mm, "mid": v(188.5, 89) * mm, "end": v(178, 78.5) * mm});
            skArc(sketch, "E76.0.1.4", {"start": v(178, 100.5) * mm, "mid": v(189.5, 89) * mm, "end": v(178, 77.5) * mm});
            skArc(sketch, "E76.0.1.5", {"start": v(178, 95.25) * mm, "mid": v(184.25, 89) * mm, "end": v(178, 82.75) * mm});
            skArc(sketch, "E76.0.2.0", {"start": v(178, 138.25) * mm, "mid": v(183.25, 133) * mm, "end": v(178, 127.75) * mm});
            skArc(sketch, "E76.0.2.1", {"start": v(178, 148.75) * mm, "mid": v(193.75, 133) * mm, "end": v(178, 117.25) * mm});
            skArc(sketch, "E76.0.2.2", {"start": v(178, 149.75) * mm, "mid": v(194.75, 133) * mm, "end": v(178, 116.25) * mm});
            skArc(sketch, "E76.0.2.3", {"start": v(178, 143.5) * mm, "mid": v(188.5, 133) * mm, "end": v(178, 122.5) * mm});
            skArc(sketch, "E76.0.2.4", {"start": v(178, 144.5) * mm, "mid": v(189.5, 133) * mm, "end": v(178, 121.5) * mm});
            skArc(sketch, "E76.0.2.5", {"start": v(178, 139.25) * mm, "mid": v(184.25, 133) * mm, "end": v(178, 126.75) * mm});
            skArc(sketch, "E76.0.3.0", {"start": v(178, 182.25) * mm, "mid": v(183.25, 177) * mm, "end": v(178, 171.75) * mm});
            skArc(sketch, "E76.0.3.1", {"start": v(178, 192.75) * mm, "mid": v(193.75, 177) * mm, "end": v(178, 161.25) * mm});
            skArc(sketch, "E76.0.3.2", {"start": v(178, 193.75) * mm, "mid": v(194.75, 177) * mm, "end": v(178, 160.25) * mm});
            skArc(sketch, "E76.0.3.3", {"start": v(178, 187.5) * mm, "mid": v(188.5, 177) * mm, "end": v(178, 166.5) * mm});
            skArc(sketch, "E76.0.3.4", {"start": v(178, 188.5) * mm, "mid": v(189.5, 177) * mm, "end": v(178, 165.5) * mm});
            skArc(sketch, "E76.0.3.5", {"start": v(178, 183.25) * mm, "mid": v(184.25, 177) * mm, "end": v(178, 170.75) * mm});
            skArc(sketch, "E76.0.4.0", {"start": v(178, 226.25) * mm, "mid": v(183.25, 221) * mm, "end": v(178, 215.75) * mm});
            skArc(sketch, "E76.0.4.1", {"start": v(178, 236.75) * mm, "mid": v(193.75, 221) * mm, "end": v(178, 205.25) * mm});
            skArc(sketch, "E76.0.4.2", {"start": v(178, 237.75) * mm, "mid": v(194.75, 221) * mm, "end": v(178, 204.25) * mm});
            skArc(sketch, "E76.0.4.3", {"start": v(178, 231.5) * mm, "mid": v(188.5, 221) * mm, "end": v(178, 210.5) * mm});
            skArc(sketch, "E76.0.4.4", {"start": v(178, 232.5) * mm, "mid": v(189.5, 221) * mm, "end": v(178, 209.5) * mm});
            skArc(sketch, "E76.0.4.5", {"start": v(178, 227.25) * mm, "mid": v(184.25, 221) * mm, "end": v(178, 214.75) * mm});
            skLineSegment(sketch, "E76.direction1", {"start": v(178, 28.25) * mm, "end": v(203, 28.25) * mm, "construction": true});
            skLineSegment(sketch, "E76.direction2", {"start": v(178, 28.25) * mm, "end": v(178, 72.25) * mm, "construction": true});
            skSolve(sketch);
        }
        {
            var Q0;
            Q0 = qSketchRegion(id + "F4", true);
            extrude(context, id + "F5", {"entities" : qUnion([Q0]), "operationType" : NewBodyOperationType.ADD, "depth" : 2 * mm, "offsetDistance" : 25 * mm});
        }
        {
            var Q0;
            Q0=makeQuery(id+"F3.boolean.opBoolean","COPY",FACE,{"derivedFrom":makeQuery(id+"F3.opExtrude","SWEPT_FACE",FACE,{"disambiguationData":[OSD([sQuery(id+"F2.wireOp",EDGE,"E14.0.1.4")])]})});
            var Q1;
            Q1=makeQuery(id+"F3.boolean.opBoolean","COPY",FACE,{"derivedFrom":makeQuery(id+"F3.opExtrude","SWEPT_FACE",FACE,{"disambiguationData":[OSD([sQuery(id+"F2.wireOp",EDGE,"E14.0.1.1")])]})});
            var Q2;
            Q2=makeQuery(id+"F3.boolean.opBoolean","COPY",FACE,{"derivedFrom":makeQuery(id+"F3.opExtrude","SWEPT_FACE",FACE,{"disambiguationData":[OSD([sQuery(id+"F2.wireOp",EDGE,"E14.0.1.3")])]})});
            var Q3;
            Q3=makeQuery(id+"F3.boolean.opBoolean","COPY",FACE,{"derivedFrom":makeQuery(id+"F3.opExtrude","SWEPT_FACE",FACE,{"disambiguationData":[OSD([sQuery(id+"F2.wireOp",EDGE,"E5.bottom")])]})});
            var Q4;
            Q4=makeQuery(id+"F3.boolean.opBoolean","COPY",FACE,{"derivedFrom":makeQuery(id+"F3.opExtrude","SWEPT_FACE",FACE,{"disambiguationData":[OSD([sQuery(id+"F2.wireOp",EDGE,"E5.right")])]})});
            var Q5;
            Q5=makeQuery(id+"F3.boolean.opBoolean","COPY",FACE,{"derivedFrom":makeQuery(id+"F3.opExtrude","SWEPT_FACE",FACE,{"disambiguationData":[OSD([sQuery(id+"F2.wireOp",EDGE,"E7.filletArc")])]})});
            var Q6;
            Q6=makeQuery(id+"F3.boolean.opBoolean","COPY",FACE,{"derivedFrom":makeQuery(id+"F3.opExtrude","SWEPT_FACE",FACE,{"disambiguationData":[OSD([sQuery(id+"F2.wireOp",EDGE,"E8.bottom")])]})});
            var Q7;
            Q7=makeQuery(id+"F3.boolean.opBoolean","COPY",FACE,{"derivedFrom":makeQuery(id+"F3.opExtrude","SWEPT_FACE",FACE,{"disambiguationData":[OSD([sQuery(id+"F2.wireOp",EDGE,"E8.top")])]})});
            var Q8;
            Q8=makeQuery(id+"F3.boolean.opBoolean","COPY",FACE,{"derivedFrom":makeQuery(id+"F3.opExtrude","SWEPT_FACE",FACE,{"disambiguationData":[OSD([sQuery(id+"F2.wireOp",EDGE,"E9.bottom")])]})});
            var Q9;
            Q9=makeQuery(id+"F3.boolean.opBoolean","COPY",FACE,{"derivedFrom":makeQuery(id+"F3.opExtrude","SWEPT_FACE",FACE,{"disambiguationData":[OSD([sQuery(id+"F2.wireOp",EDGE,"E9.top")])]})});
            var Q10;
            Q10=makeQuery(id+"F3.boolean.opBoolean","COPY",FACE,{"derivedFrom":makeQuery(id+"F3.opExtrude","SWEPT_FACE",FACE,{"disambiguationData":[OSD([sQuery(id+"F2.wireOp",EDGE,"E14.0.1.0")])]})});
            var Q11;
            Q11=makeQuery(id+"F5.opExtrude","SWEPT_FACE",FACE,{"disambiguationData":[OSD([sQuery(id+"F4.wireOp",EDGE,"E56.0.1.1")])]});
            var Q12;
            Q12=makeQuery(id+"F5.opExtrude","SWEPT_FACE",FACE,{"disambiguationData":[OSD([sQuery(id+"F4.wireOp",EDGE,"E55.0.2.2")])]});
            var Q13;
            Q13=makeQuery(id+"F5.opExtrude","SWEPT_FACE",FACE,{"disambiguationData":[OSD([sQuery(id+"F4.wireOp",EDGE,"E56.0.1.0")])]});
            var Q14;
            Q14=makeQuery(id+"F5.opExtrude","SWEPT_FACE",FACE,{"disambiguationData":[OSD([sQuery(id+"F4.wireOp",EDGE,"E54.bottom")])]});
            var Q15;
            Q15=makeQuery(id+"F5.opExtrude","CAP_FACE",FACE,{"disambiguationData":[OSD([sQuery(id+"F4.wireOp",EDGE,"E54.bottom"),sQuery(id+"F4.wireOp",EDGE,"E54.top"),sQuery(id+"F4.wireOp",EDGE,"E54.right"),sQuery(id+"F4.wireOp",EDGE,"E56.0.1.0"),sQuery(id+"F4.wireOp",EDGE,"E56.0.1.4"),sQuery(id+"F4.wireOp",EDGE,"E56.0.2.1"),sQuery(id+"F4.wireOp",EDGE,"E56.0.2.3"),sQuery(id+"F4.wireOp",EDGE,"E56.0.3.0"),sQuery(id+"F4.wireOp",EDGE,"E56.0.3.4"),sQuery(id+"F4.wireOp",EDGE,"E56.0.4.1"),sQuery(id+"F4.wireOp",EDGE,"E56.0.4.3"),sQuery(id+"F4.wireOp",EDGE,"E56.0.5.0"),sQuery(id+"F4.wireOp",EDGE,"E56.0.5.4"),sQuery(id+"F4.wireOp",EDGE,"E56.0.6.1"),sQuery(id+"F4.wireOp",EDGE,"E56.0.6.3"),sQuery(id+"F4.wireOp",EDGE,"E56.0.7.0"),sQuery(id+"F4.wireOp",EDGE,"E56.0.7.4"),sQuery(id+"F4.wireOp",EDGE,"E56.0.8.1"),sQuery(id+"F4.wireOp",EDGE,"E56.0.8.3"),sQuery(id+"F4.wireOp",EDGE,"E56.0.9.0"),sQuery(id+"F4.wireOp",EDGE,"E56.0.9.4"),sQuery(id+"F4.wireOp",EDGE,"E56.0.10.1"),sQuery(id+"F4.wireOp",EDGE,"E56.0.10.3"),sQuery(id+"F4.wireOp",EDGE,"E56.0.10.13"),sQuery(id+"F4.wireOp",EDGE,"E63"),sQuery(id+"F4.wireOp",EDGE,"E64"),sQuery(id+"F4.wireOp",EDGE,"E66.0.1.0"),sQuery(id+"F4.wireOp",EDGE,"E66.0.1.9"),sQuery(id+"F4.wireOp",EDGE,"E66.0.2.0"),sQuery(id+"F4.wireOp",EDGE,"E66.0.2.9"),sQuery(id+"F4.wireOp",EDGE,"E66.0.3.0"),sQuery(id+"F4.wireOp",EDGE,"E66.0.3.9"),sQuery(id+"F4.wireOp",EDGE,"E66.0.4.0"),sQuery(id+"F4.wireOp",EDGE,"E66.0.4.9"),sQuery(id+"F4.wireOp",EDGE,"E67"),sQuery(id+"F4.wireOp",EDGE,"E68"),sQuery(id+"F4.wireOp",EDGE,"E76.0.1.0"),sQuery(id+"F4.wireOp",EDGE,"E76.0.1.5"),sQuery(id+"F4.wireOp",EDGE,"E76.0.2.0"),sQuery(id+"F4.wireOp",EDGE,"E76.0.2.5"),sQuery(id+"F4.wireOp",EDGE,"E76.0.3.0"),sQuery(id+"F4.wireOp",EDGE,"E76.0.3.5"),sQuery(id+"F4.wireOp",EDGE,"E76.0.4.0"),sQuery(id+"F4.wireOp",EDGE,"E76.0.4.5")])],"isStart":false});
            var Q16;
            Q16=makeQuery(id+"F5.opExtrude","CAP_FACE",FACE,{"disambiguationData":[OSD([sQuery(id+"F4.wireOp",EDGE,"E55.0.1.0"),sQuery(id+"F4.wireOp",EDGE,"E55.0.1.1"),sQuery(id+"F4.wireOp",EDGE,"E56.0.1.2"),sQuery(id+"F4.wireOp",EDGE,"E56.0.1.5"),sQuery(id+"F4.wireOp",EDGE,"E56.0.2.2"),sQuery(id+"F4.wireOp",EDGE,"E56.0.2.5"),sQuery(id+"F4.wireOp",EDGE,"E56.0.3.2"),sQuery(id+"F4.wireOp",EDGE,"E56.0.3.5"),sQuery(id+"F4.wireOp",EDGE,"E56.0.4.2"),sQuery(id+"F4.wireOp",EDGE,"E56.0.4.5"),sQuery(id+"F4.wireOp",EDGE,"E56.0.5.2"),sQuery(id+"F4.wireOp",EDGE,"E56.0.5.5"),sQuery(id+"F4.wireOp",EDGE,"E56.0.6.2"),sQuery(id+"F4.wireOp",EDGE,"E56.0.6.5"),sQuery(id+"F4.wireOp",EDGE,"E56.0.7.2"),sQuery(id+"F4.wireOp",EDGE,"E56.0.7.5"),sQuery(id+"F4.wireOp",EDGE,"E56.0.8.2"),sQuery(id+"F4.wireOp",EDGE,"E56.0.8.5"),sQuery(id+"F4.wireOp",EDGE,"E56.0.9.2"),sQuery(id+"F4.wireOp",EDGE,"E56.0.9.5"),sQuery(id+"F4.wireOp",EDGE,"E56.0.10.2"),sQuery(id+"F4.wireOp",EDGE,"E56.0.10.5"),sQuery(id+"F4.wireOp",EDGE,"E61"),sQuery(id+"F4.wireOp",EDGE,"E62"),sQuery(id+"F4.wireOp",EDGE,"E66.0.1.3"),sQuery(id+"F4.wireOp",EDGE,"E66.0.1.5"),sQuery(id+"F4.wireOp",EDGE,"E66.0.2.3"),sQuery(id+"F4.wireOp",EDGE,"E66.0.2.5"),sQuery(id+"F4.wireOp",EDGE,"E66.0.3.3"),sQuery(id+"F4.wireOp",EDGE,"E66.0.3.5"),sQuery(id+"F4.wireOp",EDGE,"E66.0.4.3"),sQuery(id+"F4.wireOp",EDGE,"E66.0.4.5"),sQuery(id+"F4.wireOp",EDGE,"E69"),sQuery(id+"F4.wireOp",EDGE,"E70"),sQuery(id+"F4.wireOp",EDGE,"E74.bottom"),sQuery(id+"F4.wireOp",EDGE,"E74.top"),sQuery(id+"F4.wireOp",EDGE,"E74.right"),sQuery(id+"F4.wireOp",EDGE,"E75.bottom"),sQuery(id+"F4.wireOp",EDGE,"E75.top"),sQuery(id+"F4.wireOp",EDGE,"E75.right"),sQuery(id+"F4.wireOp",EDGE,"E76.0.1.3"),sQuery(id+"F4.wireOp",EDGE,"E76.0.1.4"),sQuery(id+"F4.wireOp",EDGE,"E76.0.2.3"),sQuery(id+"F4.wireOp",EDGE,"E76.0.2.4"),sQuery(id+"F4.wireOp",EDGE,"E76.0.3.3"),sQuery(id+"F4.wireOp",EDGE,"E76.0.3.4"),sQuery(id+"F4.wireOp",EDGE,"E76.0.4.3"),sQuery(id+"F4.wireOp",EDGE,"E76.0.4.4")])],"isStart":false});
            var Q17;
            Q17=makeQuery(id+"F5.opExtrude","SWEPT_FACE",FACE,{"disambiguationData":[OSD([sQuery(id+"F4.wireOp",EDGE,"E55.0.1.0"),sQuery(id+"F4.wireOp",EDGE,"E74.bottom")])]});
            var Q18;
            Q18=makeQuery(id+"F5.opExtrude","SWEPT_FACE",FACE,{"disambiguationData":[OSD([sQuery(id+"F4.wireOp",EDGE,"E55.0.1.1"),sQuery(id+"F4.wireOp",EDGE,"E74.top")])]});
            var Q19;
            Q19=makeQuery(id+"F5.opExtrude","SWEPT_FACE",FACE,{"disambiguationData":[OSD([sQuery(id+"F4.wireOp",EDGE,"E55.0.2.0")])]});
            var Q20;
            Q20=makeQuery(id+"F5.opExtrude","CAP_FACE",FACE,{"disambiguationData":[OSD([sQuery(id+"F4.wireOp",EDGE,"E55.0.2.0"),sQuery(id+"F4.wireOp",EDGE,"E55.0.2.1"),sQuery(id+"F4.wireOp",EDGE,"E55.0.2.2"),sQuery(id+"F4.wireOp",EDGE,"E56.0.1.1"),sQuery(id+"F4.wireOp",EDGE,"E56.0.1.3"),sQuery(id+"F4.wireOp",EDGE,"E56.0.2.0"),sQuery(id+"F4.wireOp",EDGE,"E56.0.2.4"),sQuery(id+"F4.wireOp",EDGE,"E56.0.3.1"),sQuery(id+"F4.wireOp",EDGE,"E56.0.3.3"),sQuery(id+"F4.wireOp",EDGE,"E56.0.4.0"),sQuery(id+"F4.wireOp",EDGE,"E56.0.4.4"),sQuery(id+"F4.wireOp",EDGE,"E56.0.5.1"),sQuery(id+"F4.wireOp",EDGE,"E56.0.5.3"),sQuery(id+"F4.wireOp",EDGE,"E56.0.6.0"),sQuery(id+"F4.wireOp",EDGE,"E56.0.6.4"),sQuery(id+"F4.wireOp",EDGE,"E56.0.7.1"),sQuery(id+"F4.wireOp",EDGE,"E56.0.7.3"),sQuery(id+"F4.wireOp",EDGE,"E56.0.8.0"),sQuery(id+"F4.wireOp",EDGE,"E56.0.8.4"),sQuery(id+"F4.wireOp",EDGE,"E56.0.9.1"),sQuery(id+"F4.wireOp",EDGE,"E56.0.9.3"),sQuery(id+"F4.wireOp",EDGE,"E56.0.10.0"),sQuery(id+"F4.wireOp",EDGE,"E56.0.10.4"),sQuery(id+"F4.wireOp",EDGE,"E56.0.10.7"),sQuery(id+"F4.wireOp",EDGE,"E58"),sQuery(id+"F4.wireOp",EDGE,"E59"),sQuery(id+"F4.wireOp",EDGE,"E66.0.1.2"),sQuery(id+"F4.wireOp",EDGE,"E66.0.1.8"),sQuery(id+"F4.wireOp",EDGE,"E66.0.2.2"),sQuery(id+"F4.wireOp",EDGE,"E66.0.2.8"),sQuery(id+"F4.wireOp",EDGE,"E66.0.3.2"),sQuery(id+"F4.wireOp",EDGE,"E66.0.3.8"),sQuery(id+"F4.wireOp",EDGE,"E66.0.4.2"),sQuery(id+"F4.wireOp",EDGE,"E66.0.4.8"),sQuery(id+"F4.wireOp",EDGE,"E71"),sQuery(id+"F4.wireOp",EDGE,"E72"),sQuery(id+"F4.wireOp",EDGE,"E76.0.1.1"),sQuery(id+"F4.wireOp",EDGE,"E76.0.1.2"),sQuery(id+"F4.wireOp",EDGE,"E76.0.2.1"),sQuery(id+"F4.wireOp",EDGE,"E76.0.2.2"),sQuery(id+"F4.wireOp",EDGE,"E76.0.3.1"),sQuery(id+"F4.wireOp",EDGE,"E76.0.3.2"),sQuery(id+"F4.wireOp",EDGE,"E76.0.4.1"),sQuery(id+"F4.wireOp",EDGE,"E76.0.4.2")])],"isStart":false});
            var Q21;
            Q21=makeQuery(id+"F5.opExtrude","SWEPT_FACE",FACE,{"disambiguationData":[OSD([sQuery(id+"F4.wireOp",EDGE,"E55.0.2.1")])]});
            var Q22;
            Q22=makeQuery(id+"F3.boolean.opBoolean","COPY",FACE,{"derivedFrom":makeQuery(id+"F3.opExtrude","SWEPT_FACE",FACE,{"disambiguationData":[OSD([sQuery(id+"F2.wireOp",EDGE,"E14.0.4.1")])]})});
            var Q23;
            Q23=makeQuery(id+"F3.boolean.opBoolean","COPY",FACE,{"derivedFrom":makeQuery(id+"F3.opExtrude","SWEPT_FACE",FACE,{"disambiguationData":[OSD([sQuery(id+"F2.wireOp",EDGE,"E46.filletArc")])]})});
            var Q24;
            Q24=makeQuery(id+"F3.boolean.opBoolean","COPY",FACE,{"derivedFrom":makeQuery(id+"F3.opExtrude","SWEPT_FACE",FACE,{"disambiguationData":[OSD([sQuery(id+"F2.wireOp",EDGE,"E44.filletArc")])]})});
            var Q25;
            Q25=makeQuery(id+"F3.boolean.opBoolean","COPY",FACE,{"derivedFrom":makeQuery(id+"F3.opExtrude","SWEPT_FACE",FACE,{"disambiguationData":[OSD([sQuery(id+"F2.wireOp",EDGE,"E14.0.4.0")])]})});
            var Q26;
            Q26=makeQuery(id+"F3.boolean.opBoolean","COPY",FACE,{"derivedFrom":makeQuery(id+"F3.opExtrude","SWEPT_FACE",FACE,{"disambiguationData":[OSD([sQuery(id+"F2.wireOp",EDGE,"E27.trimOffspring")])]})});
            var Q27;
            Q27=makeQuery(id+"F3.boolean.opBoolean","COPY",FACE,{"derivedFrom":makeQuery(id+"F3.opExtrude","SWEPT_FACE",FACE,{"disambiguationData":[OSD([sQuery(id+"F2.wireOp",EDGE,"E45.filletArc")])]})});
            var Q28;
            Q28=makeQuery(id+"F3.boolean.opBoolean","COPY",FACE,{"derivedFrom":makeQuery(id+"F3.opExtrude","SWEPT_FACE",FACE,{"disambiguationData":[OSD([sQuery(id+"F2.wireOp",EDGE,"E14.0.4.3")])]})});
            var Q29;
            Q29=makeQuery(id+"F3.boolean.opBoolean","COPY",FACE,{"derivedFrom":makeQuery(id+"F3.opExtrude","SWEPT_FACE",FACE,{"disambiguationData":[OSD([sQuery(id+"F2.wireOp",EDGE,"E47.filletArc")])]})});
            var Q30;
            Q30=makeQuery(id+"F3.boolean.opBoolean","COPY",FACE,{"derivedFrom":makeQuery(id+"F3.opExtrude","SWEPT_FACE",FACE,{"disambiguationData":[OSD([sQuery(id+"F2.wireOp",EDGE,"E14.0.4.4")])]})});
            var Q31;
            Q31=makeQuery(id+"F3.boolean.opBoolean","COPY",FACE,{"derivedFrom":makeQuery(id+"F3.opExtrude","SWEPT_FACE",FACE,{"disambiguationData":[OSD([sQuery(id+"F2.wireOp",EDGE,"E48.filletArc")])]})});
            var Q32;
            Q32=makeQuery(id+"F3.boolean.opBoolean","COPY",EDGE,{"derivedFrom":makeQuery(id+"F3.opExtrude","CAP_EDGE",EDGE,{"disambiguationData":[OSD([sQuery(id+"F2.wireOp",EDGE,"E52.filletArc")])],"isStart":true})});
            var Q33;
            Q33=makeQuery(id+"F3.boolean.opBoolean","COPY",FACE,{"derivedFrom":makeQuery(id+"F3.opExtrude","SWEPT_FACE",FACE,{"disambiguationData":[OSD([sQuery(id+"F2.wireOp",EDGE,"E14.0.2.0")])]})});
            var Q34;
            Q34=makeQuery(id+"F3.boolean.opBoolean","COPY",FACE,{"derivedFrom":makeQuery(id+"F3.opExtrude","SWEPT_FACE",FACE,{"disambiguationData":[OSD([sQuery(id+"F2.wireOp",EDGE,"E14.0.2.1")])]})});
            var Q35;
            Q35=makeQuery(id+"F3.boolean.opBoolean","COPY",EDGE,{"derivedFrom":makeQuery(id+"F3.opExtrude","CAP_EDGE",EDGE,{"disambiguationData":[OSD([sQuery(id+"F2.wireOp",EDGE,"E53.filletArc")])],"isStart":true})});
            var Q36;
            Q36=makeQuery(id+"F3.boolean.opBoolean","COPY",FACE,{"derivedFrom":makeQuery(id+"F3.opExtrude","SWEPT_FACE",FACE,{"disambiguationData":[OSD([sQuery(id+"F2.wireOp",EDGE,"E14.0.2.3")])]})});
            var Q37;
            Q37=makeQuery(id+"F3.boolean.opBoolean","COPY",FACE,{"derivedFrom":makeQuery(id+"F3.opExtrude","SWEPT_FACE",FACE,{"disambiguationData":[OSD([sQuery(id+"F2.wireOp",EDGE,"E14.0.2.4")])]})});
            var Q38;
            Q38=makeQuery(id+"F3.boolean.opBoolean","COPY",FACE,{"derivedFrom":makeQuery(id+"F3.opExtrude","SWEPT_FACE",FACE,{"disambiguationData":[OSD([sQuery(id+"F2.wireOp",EDGE,"E52.filletArc")])]})});
            var Q39;
            Q39=makeQuery(id+"F3.boolean.opBoolean","COPY",FACE,{"derivedFrom":makeQuery(id+"F3.opExtrude","SWEPT_FACE",FACE,{"disambiguationData":[OSD([sQuery(id+"F2.wireOp",EDGE,"E53.filletArc")])]})});
            var Q40;
            Q40=makeQuery(id+"F3.boolean.opBoolean","COPY",EDGE,{"derivedFrom":makeQuery(id+"F3.opExtrude","CAP_EDGE",EDGE,{"disambiguationData":[OSD([sQuery(id+"F2.wireOp",EDGE,"E47.filletArc")])],"isStart":true})});
            var Q41;
            Q41=makeQuery(id+"F3.boolean.opBoolean","COPY",FACE,{"derivedFrom":makeQuery(id+"F3.opExtrude","SWEPT_FACE",FACE,{"disambiguationData":[OSD([sQuery(id+"F2.wireOp",EDGE,"E14.0.3.0")])]})});
            var Q42;
            Q42=makeQuery(id+"F3.boolean.opBoolean","COPY",FACE,{"derivedFrom":makeQuery(id+"F3.opExtrude","SWEPT_FACE",FACE,{"disambiguationData":[OSD([sQuery(id+"F2.wireOp",EDGE,"E14.0.3.1")])]})});
            var Q43;
            Q43=makeQuery(id+"F3.boolean.opBoolean","COPY",FACE,{"derivedFrom":makeQuery(id+"F3.opExtrude","SWEPT_FACE",FACE,{"disambiguationData":[OSD([sQuery(id+"F2.wireOp",EDGE,"E22.trimOffspring")])]})});
            var Q44;
            Q44=makeQuery(id+"F3.boolean.opBoolean","COPY",EDGE,{"derivedFrom":makeQuery(id+"F3.opExtrude","CAP_EDGE",EDGE,{"disambiguationData":[OSD([sQuery(id+"F2.wireOp",EDGE,"E48.filletArc")])],"isStart":true})});
            var Q45;
            Q45=makeQuery(id+"F3.boolean.opBoolean","COPY",FACE,{"derivedFrom":makeQuery(id+"F3.opExtrude","SWEPT_FACE",FACE,{"disambiguationData":[OSD([sQuery(id+"F2.wireOp",EDGE,"E14.0.3.3")])]})});
            var Q46;
            Q46=makeQuery(id+"F3.boolean.opBoolean","COPY",FACE,{"derivedFrom":makeQuery(id+"F3.opExtrude","SWEPT_FACE",FACE,{"disambiguationData":[OSD([sQuery(id+"F2.wireOp",EDGE,"E23.trimOffspring")])]})});
            var Q47;
            Q47=makeQuery(id+"F3.boolean.opBoolean","COPY",FACE,{"derivedFrom":makeQuery(id+"F3.opExtrude","SWEPT_FACE",FACE,{"disambiguationData":[OSD([sQuery(id+"F2.wireOp",EDGE,"E41.filletArc")])]})});
            var Q48;
            Q48=makeQuery(id+"F3.boolean.opBoolean","COPY",FACE,{"derivedFrom":makeQuery(id+"F3.opExtrude","SWEPT_FACE",FACE,{"disambiguationData":[OSD([sQuery(id+"F2.wireOp",EDGE,"E14.0.3.4")])]})});
            var Q49;
            Q49=makeQuery(id+"F3.boolean.opBoolean","COPY",FACE,{"derivedFrom":makeQuery(id+"F3.opExtrude","SWEPT_FACE",FACE,{"disambiguationData":[OSD([sQuery(id+"F2.wireOp",EDGE,"E24.trimOffspring")])]})});
            var Q50;
            Q50=makeQuery(id+"F3.boolean.opBoolean","COPY",FACE,{"derivedFrom":makeQuery(id+"F3.opExtrude","SWEPT_FACE",FACE,{"disambiguationData":[OSD([sQuery(id+"F2.wireOp",EDGE,"E42.filletArc")])]})});
            var Q51;
            Q51=makeQuery(id+"F3.boolean.opBoolean","COPY",FACE,{"derivedFrom":makeQuery(id+"F3.opExtrude","SWEPT_FACE",FACE,{"disambiguationData":[OSD([sQuery(id+"F2.wireOp",EDGE,"E43.filletArc")])]})});
            var Q52;
            Q52=makeQuery(id+"F5.opExtrude","SWEPT_FACE",FACE,{"disambiguationData":[OSD([sQuery(id+"F4.wireOp",EDGE,"E56.0.3.5")])]});
            var Q53;
            Q53=makeQuery(id+"F5.opExtrude","SWEPT_FACE",FACE,{"disambiguationData":[OSD([sQuery(id+"F4.wireOp",EDGE,"E56.0.6.3")])]});
            var Q54;
            Q54=makeQuery(id+"F5.opExtrude","SWEPT_FACE",FACE,{"disambiguationData":[OSD([sQuery(id+"F4.wireOp",EDGE,"E56.0.9.1")])]});
            var Q55;
            Q55=makeQuery(id+"F5.opExtrude","SWEPT_FACE",FACE,{"disambiguationData":[OSD([sQuery(id+"F4.wireOp",EDGE,"E62")])]});
            var Q56;
            Q56=makeQuery(id+"F5.opExtrude","SWEPT_FACE",FACE,{"disambiguationData":[OSD([sQuery(id+"F4.wireOp",EDGE,"E66.0.3.2")])]});
            var Q57;
            Q57=makeQuery(id+"F5.opExtrude","SWEPT_FACE",FACE,{"disambiguationData":[OSD([sQuery(id+"F4.wireOp",EDGE,"E72")])]});
            var Q58;
            Q58=makeQuery(id+"F5.opExtrude","CAP_EDGE",EDGE,{"disambiguationData":[OSD([sQuery(id+"F4.wireOp",EDGE,"E66.0.1.0")])],"isStart":false});
            var Q59;
            Q59=makeQuery(id+"F5.opExtrude","CAP_EDGE",EDGE,{"disambiguationData":[OSD([sQuery(id+"F4.wireOp",EDGE,"E66.0.2.3")])],"isStart":false});
            var Q60;
            Q60=makeQuery(id+"F5.opExtrude","CAP_EDGE",EDGE,{"disambiguationData":[OSD([sQuery(id+"F4.wireOp",EDGE,"E66.0.3.8")])],"isStart":false});
            var Q61;
            Q61=makeQuery(id+"F5.opExtrude","CAP_EDGE",EDGE,{"disambiguationData":[OSD([sQuery(id+"F4.wireOp",EDGE,"E76.0.1.0")])],"isStart":false});
            var Q62;
            Q62=makeQuery(id+"F5.opExtrude","CAP_EDGE",EDGE,{"disambiguationData":[OSD([sQuery(id+"F4.wireOp",EDGE,"E76.0.2.2")])],"isStart":false});
            var Q63;
            Q63=makeQuery(id+"F5.opExtrude","CAP_EDGE",EDGE,{"disambiguationData":[OSD([sQuery(id+"F4.wireOp",EDGE,"E76.0.3.4")])],"isStart":false});
            var Q64;
            Q64=makeQuery(id+"F5.opExtrude","SWEPT_FACE",FACE,{"disambiguationData":[OSD([sQuery(id+"F4.wireOp",EDGE,"E56.0.3.3")])]});
            var Q65;
            Q65=makeQuery(id+"F5.opExtrude","SWEPT_FACE",FACE,{"disambiguationData":[OSD([sQuery(id+"F4.wireOp",EDGE,"E56.0.6.1")])]});
            var Q66;
            Q66=makeQuery(id+"F5.opExtrude","SWEPT_FACE",FACE,{"disambiguationData":[OSD([sQuery(id+"F4.wireOp",EDGE,"E56.0.8.5")])]});
            var Q67;
            Q67=makeQuery(id+"F5.opExtrude","SWEPT_FACE",FACE,{"disambiguationData":[OSD([sQuery(id+"F4.wireOp",EDGE,"E59")])]});
            var Q68;
            Q68=makeQuery(id+"F5.opExtrude","SWEPT_FACE",FACE,{"disambiguationData":[OSD([sQuery(id+"F4.wireOp",EDGE,"E70")])]});
            var Q69;
            Q69=makeQuery(id+"F5.opExtrude","SWEPT_FACE",FACE,{"disambiguationData":[OSD([sQuery(id+"F4.wireOp",EDGE,"E76.0.2.5")])]});
            var Q70;
            Q70=makeQuery(id+"F5.opExtrude","SWEPT_FACE",FACE,{"disambiguationData":[OSD([sQuery(id+"F4.wireOp",EDGE,"E56.0.6.2")])]});
            var Q71;
            Q71=makeQuery(id+"F5.opExtrude","SWEPT_FACE",FACE,{"disambiguationData":[OSD([sQuery(id+"F4.wireOp",EDGE,"E56.0.9.0")])]});
            var Q72;
            Q72=makeQuery(id+"F5.opExtrude","SWEPT_FACE",FACE,{"disambiguationData":[OSD([sQuery(id+"F4.wireOp",EDGE,"E66.0.3.0")])]});
            var Q73;
            Q73=makeQuery(id+"F5.opExtrude","CAP_EDGE",EDGE,{"disambiguationData":[OSD([sQuery(id+"F4.wireOp",EDGE,"E66.0.2.5")])],"isStart":false});
            var Q74;
            Q74=makeQuery(id+"F5.opExtrude","CAP_EDGE",EDGE,{"disambiguationData":[OSD([sQuery(id+"F4.wireOp",EDGE,"E66.0.3.9")])],"isStart":false});
            var Q75;
            Q75=makeQuery(id+"F5.opExtrude","CAP_EDGE",EDGE,{"disambiguationData":[OSD([sQuery(id+"F4.wireOp",EDGE,"E68")])],"isStart":false});
            var Q76;
            Q76=makeQuery(id+"F5.opExtrude","CAP_EDGE",EDGE,{"disambiguationData":[OSD([sQuery(id+"F4.wireOp",EDGE,"E76.0.1.1")])],"isStart":false});
            var Q77;
            Q77=makeQuery(id+"F5.opExtrude","CAP_EDGE",EDGE,{"disambiguationData":[OSD([sQuery(id+"F4.wireOp",EDGE,"E76.0.2.3")])],"isStart":false});
            var Q78;
            Q78=makeQuery(id+"F5.opExtrude","CAP_EDGE",EDGE,{"disambiguationData":[OSD([sQuery(id+"F4.wireOp",EDGE,"E76.0.3.5")])],"isStart":false});
            var Q79;
            Q79=makeQuery(id+"F5.opExtrude","SWEPT_FACE",FACE,{"disambiguationData":[OSD([sQuery(id+"F4.wireOp",EDGE,"E56.0.1.2")])]});
            var Q80;
            Q80=makeQuery(id+"F5.opExtrude","SWEPT_FACE",FACE,{"disambiguationData":[OSD([sQuery(id+"F4.wireOp",EDGE,"E56.0.6.4")])]});
            var Q81;
            Q81=makeQuery(id+"F5.opExtrude","SWEPT_FACE",FACE,{"disambiguationData":[OSD([sQuery(id+"F4.wireOp",EDGE,"E66.0.3.3")])]});
            var Q82;
            Q82=makeQuery(id+"F5.opExtrude","SWEPT_FACE",FACE,{"disambiguationData":[OSD([sQuery(id+"F4.wireOp",EDGE,"E74.right")])]});
            var Q83;
            Q83=makeQuery(id+"F5.opExtrude","SWEPT_FACE",FACE,{"disambiguationData":[OSD([sQuery(id+"F4.wireOp",EDGE,"E76.0.3.2")])]});
            var Q84;
            Q84=makeQuery(id+"F5.opExtrude","CAP_EDGE",EDGE,{"disambiguationData":[OSD([sQuery(id+"F4.wireOp",EDGE,"E58")])],"isStart":false});
            var Q85;
            Q85=makeQuery(id+"F5.opExtrude","CAP_EDGE",EDGE,{"disambiguationData":[OSD([sQuery(id+"F4.wireOp",EDGE,"E66.0.1.3")])],"isStart":false});
            var Q86;
            Q86=makeQuery(id+"F5.opExtrude","CAP_EDGE",EDGE,{"disambiguationData":[OSD([sQuery(id+"F4.wireOp",EDGE,"E66.0.2.8")])],"isStart":false});
            var Q87;
            Q87=makeQuery(id+"F5.opExtrude","CAP_EDGE",EDGE,{"disambiguationData":[OSD([sQuery(id+"F4.wireOp",EDGE,"E66.0.4.0")])],"isStart":false});
            var Q88;
            Q88=makeQuery(id+"F5.opExtrude","CAP_EDGE",EDGE,{"disambiguationData":[OSD([sQuery(id+"F4.wireOp",EDGE,"E69")])],"isStart":false});
            var Q89;
            Q89=makeQuery(id+"F5.opExtrude","CAP_EDGE",EDGE,{"disambiguationData":[OSD([sQuery(id+"F4.wireOp",EDGE,"E76.0.1.2")])],"isStart":false});
            var Q90;
            Q90=makeQuery(id+"F5.opExtrude","CAP_EDGE",EDGE,{"disambiguationData":[OSD([sQuery(id+"F4.wireOp",EDGE,"E76.0.2.4")])],"isStart":false});
            var Q91;
            Q91=makeQuery(id+"F5.opExtrude","CAP_EDGE",EDGE,{"disambiguationData":[OSD([sQuery(id+"F4.wireOp",EDGE,"E76.0.4.0")])],"isStart":false});
            var Q92;
            Q92=makeQuery(id+"F5.opExtrude","SWEPT_FACE",FACE,{"disambiguationData":[OSD([sQuery(id+"F4.wireOp",EDGE,"E56.0.4.1")])]});
            var Q93;
            Q93=makeQuery(id+"F5.opExtrude","SWEPT_FACE",FACE,{"disambiguationData":[OSD([sQuery(id+"F4.wireOp",EDGE,"E56.0.6.5")])]});
            var Q94;
            Q94=makeQuery(id+"F5.opExtrude","SWEPT_FACE",FACE,{"disambiguationData":[OSD([sQuery(id+"F4.wireOp",EDGE,"E56.0.9.3")])]});
            var Q95;
            Q95=makeQuery(id+"F5.opExtrude","SWEPT_FACE",FACE,{"disambiguationData":[OSD([sQuery(id+"F4.wireOp",EDGE,"E64")])]});
            var Q96;
            Q96=makeQuery(id+"F5.opExtrude","SWEPT_FACE",FACE,{"disambiguationData":[OSD([sQuery(id+"F4.wireOp",EDGE,"E56.0.4.2")])]});
            var Q97;
            Q97=makeQuery(id+"F5.opExtrude","SWEPT_FACE",FACE,{"disambiguationData":[OSD([sQuery(id+"F4.wireOp",EDGE,"E56.0.7.0")])]});
            var Q98;
            Q98=makeQuery(id+"F5.opExtrude","SWEPT_FACE",FACE,{"disambiguationData":[OSD([sQuery(id+"F4.wireOp",EDGE,"E56.0.9.4")])]});
            var Q99;
            Q99=makeQuery(id+"F5.opExtrude","SWEPT_FACE",FACE,{"disambiguationData":[OSD([sQuery(id+"F4.wireOp",EDGE,"E66.0.1.0")])]});
            var Q100;
            Q100=makeQuery(id+"F5.opExtrude","SWEPT_FACE",FACE,{"disambiguationData":[OSD([sQuery(id+"F4.wireOp",EDGE,"E76.0.3.4")])]});
            var Q101;
            Q101=makeQuery(id+"F5.opExtrude","CAP_EDGE",EDGE,{"disambiguationData":[OSD([sQuery(id+"F4.wireOp",EDGE,"E66.0.1.5")])],"isStart":false});
            var Q102;
            Q102=makeQuery(id+"F5.opExtrude","CAP_EDGE",EDGE,{"disambiguationData":[OSD([sQuery(id+"F4.wireOp",EDGE,"E66.0.2.9")])],"isStart":false});
            var Q103;
            Q103=makeQuery(id+"F5.opExtrude","CAP_EDGE",EDGE,{"disambiguationData":[OSD([sQuery(id+"F4.wireOp",EDGE,"E66.0.4.2")])],"isStart":false});
            var Q104;
            Q104=makeQuery(id+"F5.opExtrude","CAP_EDGE",EDGE,{"disambiguationData":[OSD([sQuery(id+"F4.wireOp",EDGE,"E70")])],"isStart":false});
            var Q105;
            Q105=makeQuery(id+"F5.opExtrude","CAP_EDGE",EDGE,{"disambiguationData":[OSD([sQuery(id+"F4.wireOp",EDGE,"E76.0.1.3")])],"isStart":false});
            var Q106;
            Q106=makeQuery(id+"F5.opExtrude","CAP_EDGE",EDGE,{"disambiguationData":[OSD([sQuery(id+"F4.wireOp",EDGE,"E76.0.2.5")])],"isStart":false});
            var Q107;
            Q107=makeQuery(id+"F5.opExtrude","CAP_EDGE",EDGE,{"disambiguationData":[OSD([sQuery(id+"F4.wireOp",EDGE,"E76.0.4.1")])],"isStart":false});
            var Q108;
            Q108=makeQuery(id+"F5.opExtrude","SWEPT_FACE",FACE,{"disambiguationData":[OSD([sQuery(id+"F4.wireOp",EDGE,"E56.0.1.5")])]});
            var Q109;
            Q109=makeQuery(id+"F5.opExtrude","SWEPT_FACE",FACE,{"disambiguationData":[OSD([sQuery(id+"F4.wireOp",EDGE,"E56.0.4.3")])]});
            var Q110;
            Q110=makeQuery(id+"F5.opExtrude","SWEPT_FACE",FACE,{"disambiguationData":[OSD([sQuery(id+"F4.wireOp",EDGE,"E56.0.7.1")])]});
            var Q111;
            Q111=makeQuery(id+"F5.opExtrude","SWEPT_FACE",FACE,{"disambiguationData":[OSD([sQuery(id+"F4.wireOp",EDGE,"E56.0.9.5")])]});
            var Q112;
            Q112=makeQuery(id+"F5.opExtrude","SWEPT_FACE",FACE,{"disambiguationData":[OSD([sQuery(id+"F4.wireOp",EDGE,"E66.0.1.2")])]});
            var Q113;
            Q113=makeQuery(id+"F5.opExtrude","SWEPT_FACE",FACE,{"disambiguationData":[OSD([sQuery(id+"F4.wireOp",EDGE,"E76.0.3.5")])]});
            var Q114;
            Q114=makeQuery(id+"F5.opExtrude","SWEPT_FACE",FACE,{"disambiguationData":[OSD([sQuery(id+"F4.wireOp",EDGE,"E56.0.10.0")])]});
            var Q115;
            Q115=makeQuery(id+"F5.opExtrude","SWEPT_FACE",FACE,{"disambiguationData":[OSD([sQuery(id+"F4.wireOp",EDGE,"E66.0.1.3")])]});
            var Q116;
            Q116=makeQuery(id+"F5.opExtrude","SWEPT_FACE",FACE,{"disambiguationData":[OSD([sQuery(id+"F4.wireOp",EDGE,"E66.0.4.0")])]});
            var Q117;
            Q117=makeQuery(id+"F5.opExtrude","SWEPT_FACE",FACE,{"disambiguationData":[OSD([sQuery(id+"F4.wireOp",EDGE,"E76.0.1.2")])]});
            var Q118;
            Q118=makeQuery(id+"F5.opExtrude","CAP_EDGE",EDGE,{"disambiguationData":[OSD([sQuery(id+"F4.wireOp",EDGE,"E61")])],"isStart":false});
            var Q119;
            Q119=makeQuery(id+"F5.opExtrude","CAP_EDGE",EDGE,{"disambiguationData":[OSD([sQuery(id+"F4.wireOp",EDGE,"E66.0.1.8")])],"isStart":false});
            var Q120;
            Q120=makeQuery(id+"F5.opExtrude","CAP_EDGE",EDGE,{"disambiguationData":[OSD([sQuery(id+"F4.wireOp",EDGE,"E66.0.3.0")])],"isStart":false});
            var Q121;
            Q121=makeQuery(id+"F5.opExtrude","CAP_EDGE",EDGE,{"disambiguationData":[OSD([sQuery(id+"F4.wireOp",EDGE,"E66.0.4.3")])],"isStart":false});
            var Q122;
            Q122=makeQuery(id+"F5.opExtrude","CAP_EDGE",EDGE,{"disambiguationData":[OSD([sQuery(id+"F4.wireOp",EDGE,"E71")])],"isStart":false});
            var Q123;
            Q123=makeQuery(id+"F5.opExtrude","CAP_EDGE",EDGE,{"disambiguationData":[OSD([sQuery(id+"F4.wireOp",EDGE,"E76.0.1.4")])],"isStart":false});
            var Q124;
            Q124=makeQuery(id+"F5.opExtrude","CAP_EDGE",EDGE,{"disambiguationData":[OSD([sQuery(id+"F4.wireOp",EDGE,"E76.0.3.0")])],"isStart":false});
            var Q125;
            Q125=makeQuery(id+"F5.opExtrude","CAP_EDGE",EDGE,{"disambiguationData":[OSD([sQuery(id+"F4.wireOp",EDGE,"E76.0.4.2")])],"isStart":false});
            var Q126;
            Q126=makeQuery(id+"F5.opExtrude","SWEPT_FACE",FACE,{"disambiguationData":[OSD([sQuery(id+"F4.wireOp",EDGE,"E56.0.2.1")])]});
            var Q127;
            Q127=makeQuery(id+"F5.opExtrude","SWEPT_FACE",FACE,{"disambiguationData":[OSD([sQuery(id+"F4.wireOp",EDGE,"E56.0.4.5")])]});
            var Q128;
            Q128=makeQuery(id+"F5.opExtrude","SWEPT_FACE",FACE,{"disambiguationData":[OSD([sQuery(id+"F4.wireOp",EDGE,"E56.0.7.3")])]});
            var Q129;
            Q129=makeQuery(id+"F5.opExtrude","SWEPT_FACE",FACE,{"disambiguationData":[OSD([sQuery(id+"F4.wireOp",EDGE,"E56.0.10.1")])]});
            var Q130;
            Q130=makeQuery(id+"F5.opExtrude","SWEPT_FACE",FACE,{"disambiguationData":[OSD([sQuery(id+"F4.wireOp",EDGE,"E66.0.4.2")])]});
            var Q131;
            Q131=makeQuery(id+"F5.opExtrude","SWEPT_FACE",FACE,{"disambiguationData":[OSD([sQuery(id+"F4.wireOp",EDGE,"E56.0.2.2")])]});
            var Q132;
            Q132=makeQuery(id+"F5.opExtrude","SWEPT_FACE",FACE,{"disambiguationData":[OSD([sQuery(id+"F4.wireOp",EDGE,"E56.0.5.0")])]});
            var Q133;
            Q133=makeQuery(id+"F5.opExtrude","SWEPT_FACE",FACE,{"disambiguationData":[OSD([sQuery(id+"F4.wireOp",EDGE,"E56.0.7.4")])]});
            var Q134;
            Q134=makeQuery(id+"F5.opExtrude","SWEPT_FACE",FACE,{"disambiguationData":[OSD([sQuery(id+"F4.wireOp",EDGE,"E66.0.4.3")])]});
            var Q135;
            Q135=makeQuery(id+"F5.opExtrude","SWEPT_FACE",FACE,{"disambiguationData":[OSD([sQuery(id+"F4.wireOp",EDGE,"E76.0.1.4")])]});
            var Q136;
            Q136=makeQuery(id+"F5.opExtrude","SWEPT_FACE",FACE,{"disambiguationData":[OSD([sQuery(id+"F4.wireOp",EDGE,"E76.0.4.2")])]});
            var Q137;
            Q137=makeQuery(id+"F5.opExtrude","CAP_EDGE",EDGE,{"disambiguationData":[OSD([sQuery(id+"F4.wireOp",EDGE,"E62")])],"isStart":false});
            var Q138;
            Q138=makeQuery(id+"F5.opExtrude","CAP_EDGE",EDGE,{"disambiguationData":[OSD([sQuery(id+"F4.wireOp",EDGE,"E66.0.1.9")])],"isStart":false});
            var Q139;
            Q139=makeQuery(id+"F5.opExtrude","CAP_EDGE",EDGE,{"disambiguationData":[OSD([sQuery(id+"F4.wireOp",EDGE,"E66.0.3.2")])],"isStart":false});
            var Q140;
            Q140=makeQuery(id+"F5.opExtrude","CAP_EDGE",EDGE,{"disambiguationData":[OSD([sQuery(id+"F4.wireOp",EDGE,"E66.0.4.5")])],"isStart":false});
            var Q141;
            Q141=makeQuery(id+"F5.opExtrude","CAP_EDGE",EDGE,{"disambiguationData":[OSD([sQuery(id+"F4.wireOp",EDGE,"E72")])],"isStart":false});
            var Q142;
            Q142=makeQuery(id+"F5.opExtrude","CAP_EDGE",EDGE,{"disambiguationData":[OSD([sQuery(id+"F4.wireOp",EDGE,"E76.0.1.5")])],"isStart":false});
            var Q143;
            Q143=makeQuery(id+"F5.opExtrude","CAP_EDGE",EDGE,{"disambiguationData":[OSD([sQuery(id+"F4.wireOp",EDGE,"E76.0.3.1")])],"isStart":false});
            var Q144;
            Q144=makeQuery(id+"F5.opExtrude","CAP_EDGE",EDGE,{"disambiguationData":[OSD([sQuery(id+"F4.wireOp",EDGE,"E76.0.4.3")])],"isStart":false});
            var Q145;
            Q145=makeQuery(id+"F5.opExtrude","SWEPT_FACE",FACE,{"disambiguationData":[OSD([sQuery(id+"F4.wireOp",EDGE,"E56.0.2.3")])]});
            var Q146;
            Q146=makeQuery(id+"F5.opExtrude","SWEPT_FACE",FACE,{"disambiguationData":[OSD([sQuery(id+"F4.wireOp",EDGE,"E56.0.5.1")])]});
            var Q147;
            Q147=makeQuery(id+"F5.opExtrude","SWEPT_FACE",FACE,{"disambiguationData":[OSD([sQuery(id+"F4.wireOp",EDGE,"E56.0.7.5")])]});
            var Q148;
            Q148=makeQuery(id+"F5.opExtrude","SWEPT_FACE",FACE,{"disambiguationData":[OSD([sQuery(id+"F4.wireOp",EDGE,"E56.0.10.3")])]});
            var Q149;
            Q149=makeQuery(id+"F5.opExtrude","SWEPT_FACE",FACE,{"disambiguationData":[OSD([sQuery(id+"F4.wireOp",EDGE,"E76.0.1.5")])]});
            var Q150;
            Q150=makeQuery(id+"F5.opExtrude","SWEPT_FACE",FACE,{"disambiguationData":[OSD([sQuery(id+"F4.wireOp",EDGE,"E56.0.5.2")])]});
            var Q151;
            Q151=makeQuery(id+"F5.opExtrude","SWEPT_FACE",FACE,{"disambiguationData":[OSD([sQuery(id+"F4.wireOp",EDGE,"E56.0.8.0")])]});
            var Q152;
            Q152=makeQuery(id+"F5.opExtrude","SWEPT_FACE",FACE,{"disambiguationData":[OSD([sQuery(id+"F4.wireOp",EDGE,"E56.0.10.4")])]});
            var Q153;
            Q153=makeQuery(id+"F5.opExtrude","SWEPT_FACE",FACE,{"disambiguationData":[OSD([sQuery(id+"F4.wireOp",EDGE,"E66.0.2.0")])]});
            var Q154;
            Q154=makeQuery(id+"F5.opExtrude","SWEPT_FACE",FACE,{"disambiguationData":[OSD([sQuery(id+"F4.wireOp",EDGE,"E76.0.4.4")])]});
            var Q155;
            Q155=makeQuery(id+"F5.opExtrude","CAP_EDGE",EDGE,{"disambiguationData":[OSD([sQuery(id+"F4.wireOp",EDGE,"E63")])],"isStart":false});
            var Q156;
            Q156=makeQuery(id+"F5.opExtrude","CAP_EDGE",EDGE,{"disambiguationData":[OSD([sQuery(id+"F4.wireOp",EDGE,"E66.0.2.0")])],"isStart":false});
            var Q157;
            Q157=makeQuery(id+"F5.opExtrude","CAP_EDGE",EDGE,{"disambiguationData":[OSD([sQuery(id+"F4.wireOp",EDGE,"E66.0.3.3")])],"isStart":false});
            var Q158;
            Q158=makeQuery(id+"F5.opExtrude","CAP_EDGE",EDGE,{"disambiguationData":[OSD([sQuery(id+"F4.wireOp",EDGE,"E66.0.4.8")])],"isStart":false});
            var Q159;
            Q159=makeQuery(id+"F5.opExtrude","CAP_EDGE",EDGE,{"disambiguationData":[OSD([sQuery(id+"F4.wireOp",EDGE,"E76.0.2.0")])],"isStart":false});
            var Q160;
            Q160=makeQuery(id+"F5.opExtrude","CAP_EDGE",EDGE,{"disambiguationData":[OSD([sQuery(id+"F4.wireOp",EDGE,"E76.0.3.2")])],"isStart":false});
            var Q161;
            Q161=makeQuery(id+"F5.opExtrude","CAP_EDGE",EDGE,{"disambiguationData":[OSD([sQuery(id+"F4.wireOp",EDGE,"E76.0.4.4")])],"isStart":false});
            var Q162;
            Q162=makeQuery(id+"F5.opExtrude","SWEPT_FACE",FACE,{"disambiguationData":[OSD([sQuery(id+"F4.wireOp",EDGE,"E56.0.2.5")])]});
            var Q163;
            Q163=makeQuery(id+"F5.opExtrude","SWEPT_FACE",FACE,{"disambiguationData":[OSD([sQuery(id+"F4.wireOp",EDGE,"E56.0.5.3")])]});
            var Q164;
            Q164=makeQuery(id+"F5.opExtrude","SWEPT_FACE",FACE,{"disambiguationData":[OSD([sQuery(id+"F4.wireOp",EDGE,"E56.0.8.1")])]});
            var Q165;
            Q165=makeQuery(id+"F5.opExtrude","SWEPT_FACE",FACE,{"disambiguationData":[OSD([sQuery(id+"F4.wireOp",EDGE,"E66.0.2.2")])]});
            var Q166;
            Q166=makeQuery(id+"F5.opExtrude","SWEPT_FACE",FACE,{"disambiguationData":[OSD([sQuery(id+"F4.wireOp",EDGE,"E76.0.4.5")])]});
            var Q167;
            Q167=makeQuery(id+"F5.opExtrude","SWEPT_FACE",FACE,{"disambiguationData":[OSD([sQuery(id+"F4.wireOp",EDGE,"E56.0.5.4")])]});
            var Q168;
            Q168=makeQuery(id+"F5.opExtrude","SWEPT_FACE",FACE,{"disambiguationData":[OSD([sQuery(id+"F4.wireOp",EDGE,"E56.0.10.7")])]});
            var Q169;
            Q169=makeQuery(id+"F5.opExtrude","SWEPT_FACE",FACE,{"disambiguationData":[OSD([sQuery(id+"F4.wireOp",EDGE,"E66.0.2.3")])]});
            var Q170;
            Q170=makeQuery(id+"F5.opExtrude","SWEPT_FACE",FACE,{"disambiguationData":[OSD([sQuery(id+"F4.wireOp",EDGE,"E76.0.2.2")])]});
            var Q171;
            Q171=makeQuery(id+"F5.opExtrude","CAP_EDGE",EDGE,{"disambiguationData":[OSD([sQuery(id+"F4.wireOp",EDGE,"E64")])],"isStart":false});
            var Q172;
            Q172=makeQuery(id+"F5.opExtrude","CAP_EDGE",EDGE,{"disambiguationData":[OSD([sQuery(id+"F4.wireOp",EDGE,"E66.0.2.2")])],"isStart":false});
            var Q173;
            Q173=makeQuery(id+"F5.opExtrude","CAP_EDGE",EDGE,{"disambiguationData":[OSD([sQuery(id+"F4.wireOp",EDGE,"E66.0.3.5")])],"isStart":false});
            var Q174;
            Q174=makeQuery(id+"F5.opExtrude","CAP_EDGE",EDGE,{"disambiguationData":[OSD([sQuery(id+"F4.wireOp",EDGE,"E66.0.4.9")])],"isStart":false});
            var Q175;
            Q175=makeQuery(id+"F5.opExtrude","CAP_EDGE",EDGE,{"disambiguationData":[OSD([sQuery(id+"F4.wireOp",EDGE,"E76.0.2.1")])],"isStart":false});
            var Q176;
            Q176=makeQuery(id+"F5.opExtrude","CAP_EDGE",EDGE,{"disambiguationData":[OSD([sQuery(id+"F4.wireOp",EDGE,"E76.0.3.3")])],"isStart":false});
            var Q177;
            Q177=makeQuery(id+"F5.opExtrude","CAP_EDGE",EDGE,{"disambiguationData":[OSD([sQuery(id+"F4.wireOp",EDGE,"E76.0.4.5")])],"isStart":false});
            var Q178;
            Q178=makeQuery(id+"F5.opExtrude","SWEPT_FACE",FACE,{"disambiguationData":[OSD([sQuery(id+"F4.wireOp",EDGE,"E56.0.3.1")])]});
            var Q179;
            Q179=makeQuery(id+"F5.opExtrude","SWEPT_FACE",FACE,{"disambiguationData":[OSD([sQuery(id+"F4.wireOp",EDGE,"E56.0.5.5")])]});
            var Q180;
            Q180=makeQuery(id+"F5.opExtrude","SWEPT_FACE",FACE,{"disambiguationData":[OSD([sQuery(id+"F4.wireOp",EDGE,"E56.0.8.3")])]});
            var Q181;
            Q181=makeQuery(id+"F5.opExtrude","SWEPT_FACE",FACE,{"disambiguationData":[OSD([sQuery(id+"F4.wireOp",EDGE,"E56.0.10.13")])]});
            var Q182;
            Q182=makeQuery(id+"F5.opExtrude","SWEPT_FACE",FACE,{"disambiguationData":[OSD([sQuery(id+"F4.wireOp",EDGE,"E68")])]});
            var Q183;
            Q183=makeQuery(id+"F5.opExtrude","SWEPT_FACE",FACE,{"disambiguationData":[OSD([sQuery(id+"F4.wireOp",EDGE,"E56.0.3.2")])]});
            var Q184;
            Q184=makeQuery(id+"F5.opExtrude","SWEPT_FACE",FACE,{"disambiguationData":[OSD([sQuery(id+"F4.wireOp",EDGE,"E56.0.6.0")])]});
            var Q185;
            Q185=makeQuery(id+"F5.opExtrude","SWEPT_FACE",FACE,{"disambiguationData":[OSD([sQuery(id+"F4.wireOp",EDGE,"E56.0.8.4")])]});
            var Q186;
            Q186=makeQuery(id+"F5.opExtrude","SWEPT_FACE",FACE,{"disambiguationData":[OSD([sQuery(id+"F4.wireOp",EDGE,"E76.0.2.4")])]});
            var Q187;
            Q187=makeQuery(id+"F3.boolean.opBoolean","COPY",EDGE,{"derivedFrom":makeQuery(id+"F3.opExtrude","SWEPT_EDGE",EDGE,{"disambiguationData":[OSD([sQuery(id+"F2.wireOp",EDGE,"E9.top"),sQuery(id+"F2.wireOp",EDGE,"E53.filletArc")])]})});
            var Q188;
            Q188=makeQuery(id+"F3.boolean.opBoolean","COPY",EDGE,{"derivedFrom":makeQuery(id+"F3.opExtrude","SWEPT_EDGE",EDGE,{"disambiguationData":[OSD([sQuery(id+"F2.wireOp",EDGE,"E8.bottom"),sQuery(id+"F2.wireOp",EDGE,"E10.filletArc")])]})});
            var Q189;
            Q189=makeQuery(id+"F3.boolean.opBoolean","COPY",EDGE,{"derivedFrom":makeQuery(id+"F3.opExtrude","SWEPT_EDGE",EDGE,{"disambiguationData":[OSD([sQuery(id+"F2.wireOp",EDGE,"E9.bottom"),sQuery(id+"F2.wireOp",EDGE,"E48.filletArc")])]})});
            var Q190;
            Q190=makeQuery(id+"F5.opExtrude","SWEPT_EDGE",EDGE,{"disambiguationData":[OSD([sQuery(id+"F4.wireOp",EDGE,"E54.bottom"),sQuery(id+"F4.wireOp",EDGE,"E54.left"),sQuery(id+"F4.wireOp",EDGE,"E63")])]});
            var Q191;
            Q191=makeQuery(id+"F5.opExtrude","SWEPT_FACE",FACE,{"disambiguationData":[OSD([sQuery(id+"F4.wireOp",EDGE,"E54.top")])]});
            var Q192;
            Q192=makeQuery(id+"F3.boolean.opBoolean","COPY",EDGE,{"derivedFrom":makeQuery(id+"F3.opExtrude","CAP_EDGE",EDGE,{"disambiguationData":[OSD([sQuery(id+"F2.wireOp",EDGE,"E14.0.1.0")])],"isStart":true})});
            var Q193;
            Q193=makeQuery(id+"F3.boolean.opBoolean","COPY",EDGE,{"derivedFrom":makeQuery(id+"F3.opExtrude","CAP_EDGE",EDGE,{"disambiguationData":[OSD([sQuery(id+"F2.wireOp",EDGE,"E14.0.2.3")])],"isStart":true})});
            var Q194;
            Q194=makeQuery(id+"F3.boolean.opBoolean","COPY",EDGE,{"derivedFrom":makeQuery(id+"F3.opExtrude","CAP_EDGE",EDGE,{"disambiguationData":[OSD([sQuery(id+"F2.wireOp",EDGE,"E14.0.3.10"),sQuery(id+"F2.wireOp",EDGE,"E14.0.3.11")])],"isStart":true})});
            var Q195;
            Q195=makeQuery(id+"F3.boolean.opBoolean","COPY",EDGE,{"derivedFrom":makeQuery(id+"F3.opExtrude","CAP_EDGE",EDGE,{"disambiguationData":[OSD([sQuery(id+"F2.wireOp",EDGE,"E42.filletArc")])],"isStart":true})});
            var Q196;
            Q196=makeQuery(id+"F3.boolean.opBoolean","COPY",EDGE,{"derivedFrom":makeQuery(id+"F3.opExtrude","CAP_EDGE",EDGE,{"disambiguationData":[OSD([sQuery(id+"F2.wireOp",EDGE,"E7.filletArc")])],"isStart":true})});
            var Q197;
            Q197=makeQuery(id+"F3.boolean.opBoolean","COPY",EDGE,{"derivedFrom":makeQuery(id+"F3.opExtrude","CAP_EDGE",EDGE,{"disambiguationData":[OSD([sQuery(id+"F2.wireOp",EDGE,"E14.0.1.1")])],"isStart":true})});
            var Q198;
            Q198=makeQuery(id+"F3.boolean.opBoolean","COPY",EDGE,{"derivedFrom":makeQuery(id+"F3.opExtrude","CAP_EDGE",EDGE,{"disambiguationData":[OSD([sQuery(id+"F2.wireOp",EDGE,"E14.0.2.4")])],"isStart":true})});
            var Q199;
            Q199=makeQuery(id+"F3.boolean.opBoolean","COPY",EDGE,{"derivedFrom":makeQuery(id+"F3.opExtrude","CAP_EDGE",EDGE,{"disambiguationData":[OSD([sQuery(id+"F2.wireOp",EDGE,"E14.0.3.12"),sQuery(id+"F2.wireOp",EDGE,"E14.0.3.13")])],"isStart":true})});
            var Q200;
            Q200=makeQuery(id+"F3.boolean.opBoolean","COPY",EDGE,{"derivedFrom":makeQuery(id+"F3.opExtrude","CAP_EDGE",EDGE,{"disambiguationData":[OSD([sQuery(id+"F2.wireOp",EDGE,"E43.filletArc")])],"isStart":true})});
            var Q201;
            Q201=makeQuery(id+"F3.boolean.opBoolean","COPY",EDGE,{"derivedFrom":makeQuery(id+"F3.opExtrude","CAP_EDGE",EDGE,{"disambiguationData":[OSD([sQuery(id+"F2.wireOp",EDGE,"E8.bottom")])],"isStart":true})});
            var Q202;
            Q202=makeQuery(id+"F3.boolean.opBoolean","COPY",EDGE,{"derivedFrom":makeQuery(id+"F3.opExtrude","CAP_EDGE",EDGE,{"disambiguationData":[OSD([sQuery(id+"F2.wireOp",EDGE,"E14.0.1.3")])],"isStart":true})});
            var Q203;
            Q203=makeQuery(id+"F3.boolean.opBoolean","COPY",EDGE,{"derivedFrom":makeQuery(id+"F3.opExtrude","CAP_EDGE",EDGE,{"disambiguationData":[OSD([sQuery(id+"F2.wireOp",EDGE,"E14.0.2.10"),sQuery(id+"F2.wireOp",EDGE,"E14.0.2.11")])],"isStart":true})});
            var Q204;
            Q204=makeQuery(id+"F3.boolean.opBoolean","COPY",EDGE,{"derivedFrom":makeQuery(id+"F3.opExtrude","CAP_EDGE",EDGE,{"disambiguationData":[OSD([sQuery(id+"F2.wireOp",EDGE,"E14.0.4.0")])],"isStart":true})});
            var Q205;
            Q205=makeQuery(id+"F3.boolean.opBoolean","COPY",EDGE,{"derivedFrom":makeQuery(id+"F3.opExtrude","CAP_EDGE",EDGE,{"disambiguationData":[OSD([sQuery(id+"F2.wireOp",EDGE,"E27.trimOffspring")])],"isStart":true})});
            var Q206;
            Q206=makeQuery(id+"F3.boolean.opBoolean","COPY",EDGE,{"derivedFrom":makeQuery(id+"F3.opExtrude","CAP_EDGE",EDGE,{"disambiguationData":[OSD([sQuery(id+"F2.wireOp",EDGE,"E44.filletArc")])],"isStart":true})});
            var Q207;
            Q207=makeQuery(id+"F3.boolean.opBoolean","COPY",EDGE,{"derivedFrom":makeQuery(id+"F3.opExtrude","CAP_EDGE",EDGE,{"disambiguationData":[OSD([sQuery(id+"F2.wireOp",EDGE,"E52.filletArc")])],"isStart":false})});
            var Q208;
            Q208=makeQuery(id+"F3.boolean.opBoolean","COPY",EDGE,{"derivedFrom":makeQuery(id+"F3.opExtrude","CAP_EDGE",EDGE,{"disambiguationData":[OSD([sQuery(id+"F2.wireOp",EDGE,"E8.top")])],"isStart":true})});
            var Q209;
            Q209=makeQuery(id+"F3.boolean.opBoolean","COPY",EDGE,{"derivedFrom":makeQuery(id+"F3.opExtrude","CAP_EDGE",EDGE,{"disambiguationData":[OSD([sQuery(id+"F2.wireOp",EDGE,"E14.0.1.4")])],"isStart":true})});
            var Q210;
            Q210=makeQuery(id+"F3.boolean.opBoolean","COPY",EDGE,{"derivedFrom":makeQuery(id+"F3.opExtrude","CAP_EDGE",EDGE,{"disambiguationData":[OSD([sQuery(id+"F2.wireOp",EDGE,"E14.0.2.12"),sQuery(id+"F2.wireOp",EDGE,"E14.0.2.13")])],"isStart":true})});
            var Q211;
            Q211=makeQuery(id+"F3.boolean.opBoolean","COPY",EDGE,{"derivedFrom":makeQuery(id+"F3.opExtrude","CAP_EDGE",EDGE,{"disambiguationData":[OSD([sQuery(id+"F2.wireOp",EDGE,"E14.0.4.1")])],"isStart":true})});
            var Q212;
            Q212=makeQuery(id+"F3.boolean.opBoolean","COPY",EDGE,{"derivedFrom":makeQuery(id+"F3.opExtrude","CAP_EDGE",EDGE,{"disambiguationData":[OSD([sQuery(id+"F2.wireOp",EDGE,"E45.filletArc")])],"isStart":true})});
            var Q213;
            Q213=makeQuery(id+"F3.boolean.opBoolean","COPY",EDGE,{"derivedFrom":makeQuery(id+"F3.opExtrude","CAP_EDGE",EDGE,{"disambiguationData":[OSD([sQuery(id+"F2.wireOp",EDGE,"E53.filletArc")])],"isStart":false})});
            var Q214;
            Q214=makeQuery(id+"F3.boolean.opBoolean","COPY",EDGE,{"derivedFrom":makeQuery(id+"F3.opExtrude","SWEPT_EDGE",EDGE,{"disambiguationData":[OSD([sQuery(id+"F2.wireOp",EDGE,"E31"),sQuery(id+"F2.wireOp",EDGE,"E53.filletArc")])]})});
            var Q215;
            Q215=makeQuery(id+"F3.boolean.opBoolean","COPY",EDGE,{"derivedFrom":makeQuery(id+"F3.opExtrude","CAP_EDGE",EDGE,{"disambiguationData":[OSD([sQuery(id+"F2.wireOp",EDGE,"E9.bottom")])],"isStart":true})});
            var Q216;
            Q216=makeQuery(id+"F3.boolean.opBoolean","COPY",EDGE,{"derivedFrom":makeQuery(id+"F3.opExtrude","CAP_EDGE",EDGE,{"disambiguationData":[OSD([sQuery(id+"F2.wireOp",EDGE,"E14.0.1.10"),sQuery(id+"F2.wireOp",EDGE,"E14.0.1.11")])],"isStart":true})});
            var Q217;
            Q217=makeQuery(id+"F3.boolean.opBoolean","COPY",EDGE,{"derivedFrom":makeQuery(id+"F3.opExtrude","CAP_EDGE",EDGE,{"disambiguationData":[OSD([sQuery(id+"F2.wireOp",EDGE,"E14.0.3.0")])],"isStart":true})});
            var Q218;
            Q218=makeQuery(id+"F3.boolean.opBoolean","COPY",EDGE,{"derivedFrom":makeQuery(id+"F3.opExtrude","CAP_EDGE",EDGE,{"disambiguationData":[OSD([sQuery(id+"F2.wireOp",EDGE,"E14.0.4.3")])],"isStart":true})});
            var Q219;
            Q219=makeQuery(id+"F3.boolean.opBoolean","COPY",EDGE,{"derivedFrom":makeQuery(id+"F3.opExtrude","CAP_EDGE",EDGE,{"disambiguationData":[OSD([sQuery(id+"F2.wireOp",EDGE,"E46.filletArc")])],"isStart":true})});
            var Q220;
            Q220=makeQuery(id+"F3.boolean.opBoolean","COPY",EDGE,{"derivedFrom":makeQuery(id+"F3.opExtrude","CAP_EDGE",EDGE,{"disambiguationData":[OSD([sQuery(id+"F2.wireOp",EDGE,"E5.bottom")])],"isStart":true})});
            var Q221;
            Q221=makeQuery(id+"F3.boolean.opBoolean","COPY",EDGE,{"derivedFrom":makeQuery(id+"F3.opExtrude","CAP_EDGE",EDGE,{"disambiguationData":[OSD([sQuery(id+"F2.wireOp",EDGE,"E9.top")])],"isStart":true})});
            var Q222;
            Q222=makeQuery(id+"F3.boolean.opBoolean","COPY",EDGE,{"derivedFrom":makeQuery(id+"F3.opExtrude","CAP_EDGE",EDGE,{"disambiguationData":[OSD([sQuery(id+"F2.wireOp",EDGE,"E14.0.1.12"),sQuery(id+"F2.wireOp",EDGE,"E14.0.1.13")])],"isStart":true})});
            var Q223;
            Q223=makeQuery(id+"F3.boolean.opBoolean","COPY",EDGE,{"derivedFrom":makeQuery(id+"F3.opExtrude","CAP_EDGE",EDGE,{"disambiguationData":[OSD([sQuery(id+"F2.wireOp",EDGE,"E14.0.3.1")])],"isStart":true})});
            var Q224;
            Q224=makeQuery(id+"F3.boolean.opBoolean","COPY",EDGE,{"derivedFrom":makeQuery(id+"F3.opExtrude","CAP_EDGE",EDGE,{"disambiguationData":[OSD([sQuery(id+"F2.wireOp",EDGE,"E14.0.4.4")])],"isStart":true})});
            var Q225;
            Q225=makeQuery(id+"F3.boolean.opBoolean","COPY",EDGE,{"derivedFrom":makeQuery(id+"F3.opExtrude","CAP_EDGE",EDGE,{"disambiguationData":[OSD([sQuery(id+"F2.wireOp",EDGE,"E22.trimOffspring")])],"isStart":true})});
            var Q226;
            Q226=makeQuery(id+"F3.boolean.opBoolean","COPY",EDGE,{"derivedFrom":makeQuery(id+"F3.opExtrude","CAP_EDGE",EDGE,{"disambiguationData":[OSD([sQuery(id+"F2.wireOp",EDGE,"E47.filletArc")])],"isStart":false})});
            var Q227;
            Q227=makeQuery(id+"F3.boolean.opBoolean","COPY",EDGE,{"derivedFrom":makeQuery(id+"F3.opExtrude","CAP_EDGE",EDGE,{"disambiguationData":[OSD([sQuery(id+"F2.wireOp",EDGE,"E10.filletArc"),sQuery(id+"F2.wireOp",EDGE,"E11.filletArc")])],"isStart":true})});
            var Q228;
            Q228=makeQuery(id+"F3.boolean.opBoolean","COPY",EDGE,{"derivedFrom":makeQuery(id+"F3.opExtrude","CAP_EDGE",EDGE,{"disambiguationData":[OSD([sQuery(id+"F2.wireOp",EDGE,"E14.0.2.0")])],"isStart":true})});
            var Q229;
            Q229=makeQuery(id+"F3.boolean.opBoolean","COPY",EDGE,{"derivedFrom":makeQuery(id+"F3.opExtrude","CAP_EDGE",EDGE,{"disambiguationData":[OSD([sQuery(id+"F2.wireOp",EDGE,"E14.0.3.3")])],"isStart":true})});
            var Q230;
            Q230=makeQuery(id+"F3.boolean.opBoolean","COPY",EDGE,{"derivedFrom":makeQuery(id+"F3.opExtrude","CAP_EDGE",EDGE,{"disambiguationData":[OSD([sQuery(id+"F2.wireOp",EDGE,"E14.0.4.10"),sQuery(id+"F2.wireOp",EDGE,"E14.0.4.11")])],"isStart":true})});
            var Q231;
            Q231=makeQuery(id+"F3.boolean.opBoolean","COPY",EDGE,{"derivedFrom":makeQuery(id+"F3.opExtrude","CAP_EDGE",EDGE,{"disambiguationData":[OSD([sQuery(id+"F2.wireOp",EDGE,"E23.trimOffspring")])],"isStart":true})});
            var Q232;
            Q232=makeQuery(id+"F3.boolean.opBoolean","COPY",EDGE,{"derivedFrom":makeQuery(id+"F3.opExtrude","CAP_EDGE",EDGE,{"disambiguationData":[OSD([sQuery(id+"F2.wireOp",EDGE,"E48.filletArc")])],"isStart":false})});
            var Q233;
            Q233=makeQuery(id+"F3.boolean.opBoolean","COPY",EDGE,{"derivedFrom":makeQuery(id+"F3.opExtrude","CAP_EDGE",EDGE,{"disambiguationData":[OSD([sQuery(id+"F2.wireOp",EDGE,"E5.right")])],"isStart":true})});
            var Q234;
            Q234=makeQuery(id+"F3.boolean.opBoolean","COPY",EDGE,{"derivedFrom":makeQuery(id+"F3.opExtrude","CAP_EDGE",EDGE,{"disambiguationData":[OSD([sQuery(id+"F2.wireOp",EDGE,"E14.0.2.1")])],"isStart":true})});
            var Q235;
            Q235=makeQuery(id+"F3.boolean.opBoolean","COPY",EDGE,{"derivedFrom":makeQuery(id+"F3.opExtrude","CAP_EDGE",EDGE,{"disambiguationData":[OSD([sQuery(id+"F2.wireOp",EDGE,"E14.0.3.4")])],"isStart":true})});
            var Q236;
            Q236=makeQuery(id+"F3.boolean.opBoolean","COPY",EDGE,{"derivedFrom":makeQuery(id+"F3.opExtrude","CAP_EDGE",EDGE,{"disambiguationData":[OSD([sQuery(id+"F2.wireOp",EDGE,"E14.0.4.12"),sQuery(id+"F2.wireOp",EDGE,"E14.0.4.13")])],"isStart":true})});
            var Q237;
            Q237=makeQuery(id+"F3.boolean.opBoolean","COPY",EDGE,{"derivedFrom":makeQuery(id+"F3.opExtrude","CAP_EDGE",EDGE,{"disambiguationData":[OSD([sQuery(id+"F2.wireOp",EDGE,"E24.trimOffspring")])],"isStart":true})});
            var Q238;
            Q238=makeQuery(id+"F3.boolean.opBoolean","COPY",EDGE,{"derivedFrom":makeQuery(id+"F3.opExtrude","CAP_EDGE",EDGE,{"disambiguationData":[OSD([sQuery(id+"F2.wireOp",EDGE,"E41.filletArc")])],"isStart":true})});
            var Q239;
            Q239=makeQuery(id+"F5.opExtrude","SWEPT_FACE",FACE,{"disambiguationData":[OSD([sQuery(id+"F4.wireOp",EDGE,"E76.0.3.1")])]});
            var Q240;
            Q240=makeQuery(id+"F5.opExtrude","CAP_EDGE",EDGE,{"disambiguationData":[OSD([sQuery(id+"F4.wireOp",EDGE,"E55.0.1.1"),sQuery(id+"F4.wireOp",EDGE,"E74.top")])],"isStart":false});
            var Q241;
            Q241=makeQuery(id+"F5.opExtrude","CAP_EDGE",EDGE,{"disambiguationData":[OSD([sQuery(id+"F4.wireOp",EDGE,"E56.0.4.2")])],"isStart":false});
            var Q242;
            Q242=makeQuery(id+"F5.opExtrude","CAP_EDGE",EDGE,{"disambiguationData":[OSD([sQuery(id+"F4.wireOp",EDGE,"E56.0.5.4")])],"isStart":false});
            var Q243;
            Q243=makeQuery(id+"F5.opExtrude","CAP_EDGE",EDGE,{"disambiguationData":[OSD([sQuery(id+"F4.wireOp",EDGE,"E56.0.7.0")])],"isStart":false});
            var Q244;
            Q244=makeQuery(id+"F5.opExtrude","CAP_EDGE",EDGE,{"disambiguationData":[OSD([sQuery(id+"F4.wireOp",EDGE,"E56.0.9.4")])],"isStart":false});
            var Q245;
            Q245=makeQuery(id+"F5.opExtrude","CAP_EDGE",EDGE,{"disambiguationData":[OSD([sQuery(id+"F4.wireOp",EDGE,"E67")])],"isStart":false});
            var Q246;
            Q246=makeQuery(id+"F5.opExtrude","SWEPT_FACE",FACE,{"disambiguationData":[OSD([sQuery(id+"F4.wireOp",EDGE,"E66.0.2.9")])]});
            var Q247;
            Q247=makeQuery(id+"F5.opExtrude","SWEPT_FACE",FACE,{"disambiguationData":[OSD([sQuery(id+"F4.wireOp",EDGE,"E56.0.3.4")])]});
            var Q248;
            Q248=makeQuery(id+"F5.opExtrude","SWEPT_FACE",FACE,{"disambiguationData":[OSD([sQuery(id+"F4.wireOp",EDGE,"E61")])]});
            var Q249;
            Q249=makeQuery(id+"F5.opExtrude","SWEPT_FACE",FACE,{"disambiguationData":[OSD([sQuery(id+"F4.wireOp",EDGE,"E71")])]});
            var Q250;
            Q250=makeQuery(id+"F5.opExtrude","SWEPT_FACE",FACE,{"disambiguationData":[OSD([sQuery(id+"F4.wireOp",EDGE,"E76.0.3.0")])]});
            var Q251;
            Q251=makeQuery(id+"F5.opExtrude","CAP_EDGE",EDGE,{"disambiguationData":[OSD([sQuery(id+"F4.wireOp",EDGE,"E55.0.2.0")])],"isStart":false});
            var Q252;
            Q252=makeQuery(id+"F5.opExtrude","CAP_EDGE",EDGE,{"disambiguationData":[OSD([sQuery(id+"F4.wireOp",EDGE,"E56.0.1.5")])],"isStart":false});
            var Q253;
            Q253=makeQuery(id+"F5.opExtrude","CAP_EDGE",EDGE,{"disambiguationData":[OSD([sQuery(id+"F4.wireOp",EDGE,"E56.0.3.1")])],"isStart":false});
            var Q254;
            Q254=makeQuery(id+"F5.opExtrude","CAP_EDGE",EDGE,{"disambiguationData":[OSD([sQuery(id+"F4.wireOp",EDGE,"E56.0.4.3")])],"isStart":false});
            var Q255;
            Q255=makeQuery(id+"F5.opExtrude","CAP_EDGE",EDGE,{"disambiguationData":[OSD([sQuery(id+"F4.wireOp",EDGE,"E56.0.5.5")])],"isStart":false});
            var Q256;
            Q256=makeQuery(id+"F5.opExtrude","CAP_EDGE",EDGE,{"disambiguationData":[OSD([sQuery(id+"F4.wireOp",EDGE,"E56.0.7.1")])],"isStart":false});
            var Q257;
            Q257=makeQuery(id+"F5.opExtrude","CAP_EDGE",EDGE,{"disambiguationData":[OSD([sQuery(id+"F4.wireOp",EDGE,"E56.0.8.3")])],"isStart":false});
            var Q258;
            Q258=makeQuery(id+"F5.opExtrude","CAP_EDGE",EDGE,{"disambiguationData":[OSD([sQuery(id+"F4.wireOp",EDGE,"E66.0.1.2")])],"isStart":false});
            var Q259;
            Q259=makeQuery(id+"F5.opExtrude","SWEPT_EDGE",EDGE,{"disambiguationData":[OSD([sQuery(id+"F4.wireOp",EDGE,"E56.0.4.1"),sQuery(id+"F4.wireOp",EDGE,"E66.0.2.9"),sQuery(id+"F4.wireOp",EDGE,"E56.0.4.13")])]});
            var Q260;
            Q260=makeQuery(id+"F5.opExtrude","SWEPT_FACE",FACE,{"disambiguationData":[OSD([sQuery(id+"F4.wireOp",EDGE,"E56.0.4.0")])]});
            var Q261;
            Q261=makeQuery(id+"F5.opExtrude","SWEPT_FACE",FACE,{"disambiguationData":[OSD([sQuery(id+"F4.wireOp",EDGE,"E56.0.9.2")])]});
            var Q262;
            Q262=makeQuery(id+"F5.opExtrude","SWEPT_FACE",FACE,{"disambiguationData":[OSD([sQuery(id+"F4.wireOp",EDGE,"E63")])]});
            var Q263;
            Q263=makeQuery(id+"F5.opExtrude","CAP_EDGE",EDGE,{"disambiguationData":[OSD([sQuery(id+"F4.wireOp",EDGE,"E56.0.3.2")])],"isStart":false});
            var Q264;
            Q264=makeQuery(id+"F5.opExtrude","CAP_EDGE",EDGE,{"disambiguationData":[OSD([sQuery(id+"F4.wireOp",EDGE,"E56.0.6.0")])],"isStart":false});
            var Q265;
            Q265=makeQuery(id+"F5.opExtrude","CAP_EDGE",EDGE,{"disambiguationData":[OSD([sQuery(id+"F4.wireOp",EDGE,"E56.0.8.4")])],"isStart":false});
            var Q266;
            Q266=makeQuery(id+"F5.opExtrude","CAP_EDGE",EDGE,{"disambiguationData":[OSD([sQuery(id+"F4.wireOp",EDGE,"E56.0.10.0")])],"isStart":false});
            var Q267;
            Q267=makeQuery(id+"F5.opExtrude","SWEPT_FACE",FACE,{"disambiguationData":[OSD([sQuery(id+"F4.wireOp",EDGE,"E56.0.1.3")])]});
            var Q268;
            Q268=makeQuery(id+"F5.opExtrude","SWEPT_FACE",FACE,{"disambiguationData":[OSD([sQuery(id+"F4.wireOp",EDGE,"E66.0.3.5")])]});
            var Q269;
            Q269=makeQuery(id+"F5.opExtrude","SWEPT_FACE",FACE,{"disambiguationData":[OSD([sQuery(id+"F4.wireOp",EDGE,"E75.right")])]});
            var Q270;
            Q270=makeQuery(id+"F5.opExtrude","SWEPT_FACE",FACE,{"disambiguationData":[OSD([sQuery(id+"F4.wireOp",EDGE,"E76.0.3.3")])]});
            var Q271;
            Q271=makeQuery(id+"F5.opExtrude","SWEPT_FACE",FACE,{"disambiguationData":[OSD([sQuery(id+"F4.wireOp",EDGE,"E56.0.1.4")])]});
            var Q272;
            Q272=makeQuery(id+"F5.opExtrude","SWEPT_FACE",FACE,{"disambiguationData":[OSD([sQuery(id+"F4.wireOp",EDGE,"E66.0.3.8")])]});
            var Q273;
            Q273=makeQuery(id+"F5.opExtrude","SWEPT_FACE",FACE,{"disambiguationData":[OSD([sQuery(id+"F4.wireOp",EDGE,"E76.0.1.0")])]});
            var Q274;
            Q274=makeQuery(id+"F5.opExtrude","CAP_EDGE",EDGE,{"disambiguationData":[OSD([sQuery(id+"F4.wireOp",EDGE,"E56.0.2.1")])],"isStart":false});
            var Q275;
            Q275=makeQuery(id+"F5.opExtrude","CAP_EDGE",EDGE,{"disambiguationData":[OSD([sQuery(id+"F4.wireOp",EDGE,"E56.0.3.3")])],"isStart":false});
            var Q276;
            Q276=makeQuery(id+"F5.opExtrude","CAP_EDGE",EDGE,{"disambiguationData":[OSD([sQuery(id+"F4.wireOp",EDGE,"E56.0.4.5")])],"isStart":false});
            var Q277;
            Q277=makeQuery(id+"F5.opExtrude","CAP_EDGE",EDGE,{"disambiguationData":[OSD([sQuery(id+"F4.wireOp",EDGE,"E56.0.6.1")])],"isStart":false});
            var Q278;
            Q278=makeQuery(id+"F5.opExtrude","CAP_EDGE",EDGE,{"disambiguationData":[OSD([sQuery(id+"F4.wireOp",EDGE,"E56.0.7.3")])],"isStart":false});
            var Q279;
            Q279=makeQuery(id+"F5.opExtrude","CAP_EDGE",EDGE,{"disambiguationData":[OSD([sQuery(id+"F4.wireOp",EDGE,"E56.0.10.1")])],"isStart":false});
            var Q280;
            Q280=makeQuery(id+"F5.opExtrude","CAP_EDGE",EDGE,{"disambiguationData":[OSD([sQuery(id+"F4.wireOp",EDGE,"E59")])],"isStart":false});
            var Q281;
            Q281=makeQuery(id+"F5.opExtrude","SWEPT_FACE",FACE,{"disambiguationData":[OSD([sQuery(id+"F4.wireOp",EDGE,"E66.0.3.9")])]});
            var Q282;
            Q282=makeQuery(id+"F5.opExtrude","SWEPT_FACE",FACE,{"disambiguationData":[OSD([sQuery(id+"F4.wireOp",EDGE,"E76.0.1.1")])]});
            var Q283;
            Q283=makeQuery(id+"F5.opExtrude","SWEPT_FACE",FACE,{"disambiguationData":[OSD([sQuery(id+"F4.wireOp",EDGE,"E56.0.2.0")])]});
            var Q284;
            Q284=makeQuery(id+"F5.opExtrude","SWEPT_FACE",FACE,{"disambiguationData":[OSD([sQuery(id+"F4.wireOp",EDGE,"E56.0.4.4")])]});
            var Q285;
            Q285=makeQuery(id+"F5.opExtrude","SWEPT_FACE",FACE,{"disambiguationData":[OSD([sQuery(id+"F4.wireOp",EDGE,"E56.0.7.2")])]});
            var Q286;
            Q286=makeQuery(id+"F5.opExtrude","SWEPT_FACE",FACE,{"disambiguationData":[OSD([sQuery(id+"F4.wireOp",EDGE,"E76.0.4.0")])]});
            var Q287;
            Q287=makeQuery(id+"F5.opExtrude","CAP_EDGE",EDGE,{"disambiguationData":[OSD([sQuery(id+"F4.wireOp",EDGE,"E56.0.2.2")])],"isStart":false});
            var Q288;
            Q288=makeQuery(id+"F5.opExtrude","CAP_EDGE",EDGE,{"disambiguationData":[OSD([sQuery(id+"F4.wireOp",EDGE,"E56.0.5.0")])],"isStart":false});
            var Q289;
            Q289=makeQuery(id+"F5.opExtrude","CAP_EDGE",EDGE,{"disambiguationData":[OSD([sQuery(id+"F4.wireOp",EDGE,"E56.0.6.2")])],"isStart":false});
            var Q290;
            Q290=makeQuery(id+"F5.opExtrude","CAP_EDGE",EDGE,{"disambiguationData":[OSD([sQuery(id+"F4.wireOp",EDGE,"E56.0.7.4")])],"isStart":false});
            var Q291;
            Q291=makeQuery(id+"F5.opExtrude","CAP_EDGE",EDGE,{"disambiguationData":[OSD([sQuery(id+"F4.wireOp",EDGE,"E56.0.9.0")])],"isStart":false});
            var Q292;
            Q292=makeQuery(id+"F5.opExtrude","SWEPT_FACE",FACE,{"disambiguationData":[OSD([sQuery(id+"F4.wireOp",EDGE,"E66.0.1.5")])]});
            var Q293;
            Q293=makeQuery(id+"F5.opExtrude","SWEPT_FACE",FACE,{"disambiguationData":[OSD([sQuery(id+"F4.wireOp",EDGE,"E76.0.1.3")])]});
            var Q294;
            Q294=makeQuery(id+"F5.opExtrude","SWEPT_FACE",FACE,{"disambiguationData":[OSD([sQuery(id+"F4.wireOp",EDGE,"E76.0.4.1")])]});
            var Q295;
            Q295=makeQuery(id+"F5.opExtrude","SWEPT_FACE",FACE,{"disambiguationData":[OSD([sQuery(id+"F4.wireOp",EDGE,"E56.0.10.2"),sQuery(id+"F4.wireOp",EDGE,"E75.bottom")])]});
            var Q296;
            Q296=makeQuery(id+"F5.opExtrude","SWEPT_FACE",FACE,{"disambiguationData":[OSD([sQuery(id+"F4.wireOp",EDGE,"E66.0.1.8")])]});
            var Q297;
            Q297=makeQuery(id+"F5.opExtrude","CAP_EDGE",EDGE,{"disambiguationData":[OSD([sQuery(id+"F4.wireOp",EDGE,"E56.0.2.3")])],"isStart":false});
            var Q298;
            Q298=makeQuery(id+"F5.opExtrude","CAP_EDGE",EDGE,{"disambiguationData":[OSD([sQuery(id+"F4.wireOp",EDGE,"E56.0.3.5")])],"isStart":false});
            var Q299;
            Q299=makeQuery(id+"F5.opExtrude","CAP_EDGE",EDGE,{"disambiguationData":[OSD([sQuery(id+"F4.wireOp",EDGE,"E56.0.5.1")])],"isStart":false});
            var Q300;
            Q300=makeQuery(id+"F5.opExtrude","CAP_EDGE",EDGE,{"disambiguationData":[OSD([sQuery(id+"F4.wireOp",EDGE,"E56.0.6.3")])],"isStart":false});
            var Q301;
            Q301=makeQuery(id+"F5.opExtrude","CAP_EDGE",EDGE,{"disambiguationData":[OSD([sQuery(id+"F4.wireOp",EDGE,"E56.0.9.1")])],"isStart":false});
            var Q302;
            Q302=makeQuery(id+"F5.opExtrude","CAP_EDGE",EDGE,{"disambiguationData":[OSD([sQuery(id+"F4.wireOp",EDGE,"E56.0.10.3")])],"isStart":false});
            var Q303;
            Q303=makeQuery(id+"F5.opExtrude","SWEPT_FACE",FACE,{"disambiguationData":[OSD([sQuery(id+"F4.wireOp",EDGE,"E66.0.1.9")])]});
            var Q304;
            Q304=makeQuery(id+"F5.opExtrude","SWEPT_FACE",FACE,{"disambiguationData":[OSD([sQuery(id+"F4.wireOp",EDGE,"E66.0.4.5")])]});
            var Q305;
            Q305=makeQuery(id+"F5.opExtrude","SWEPT_FACE",FACE,{"disambiguationData":[OSD([sQuery(id+"F4.wireOp",EDGE,"E76.0.4.3")])]});
            var Q306;
            Q306=makeQuery(id+"F5.opExtrude","SWEPT_FACE",FACE,{"disambiguationData":[OSD([sQuery(id+"F4.wireOp",EDGE,"E56.0.2.4")])]});
            var Q307;
            Q307=makeQuery(id+"F5.opExtrude","SWEPT_FACE",FACE,{"disambiguationData":[OSD([sQuery(id+"F4.wireOp",EDGE,"E66.0.4.8")])]});
            var Q308;
            Q308=makeQuery(id+"F5.opExtrude","SWEPT_FACE",FACE,{"disambiguationData":[OSD([sQuery(id+"F4.wireOp",EDGE,"E76.0.2.0")])]});
            var Q309;
            Q309=makeQuery(id+"F5.opExtrude","CAP_EDGE",EDGE,{"disambiguationData":[OSD([sQuery(id+"F4.wireOp",EDGE,"E56.0.1.2")])],"isStart":false});
            var Q310;
            Q310=makeQuery(id+"F5.opExtrude","CAP_EDGE",EDGE,{"disambiguationData":[OSD([sQuery(id+"F4.wireOp",EDGE,"E56.0.5.2")])],"isStart":false});
            var Q311;
            Q311=makeQuery(id+"F5.opExtrude","CAP_EDGE",EDGE,{"disambiguationData":[OSD([sQuery(id+"F4.wireOp",EDGE,"E56.0.6.4")])],"isStart":false});
            var Q312;
            Q312=makeQuery(id+"F5.opExtrude","CAP_EDGE",EDGE,{"disambiguationData":[OSD([sQuery(id+"F4.wireOp",EDGE,"E56.0.8.0")])],"isStart":false});
            var Q313;
            Q313=makeQuery(id+"F5.opExtrude","CAP_EDGE",EDGE,{"disambiguationData":[OSD([sQuery(id+"F4.wireOp",EDGE,"E56.0.10.4")])],"isStart":false});
            var Q314;
            Q314=makeQuery(id+"F5.opExtrude","SWEPT_FACE",FACE,{"disambiguationData":[OSD([sQuery(id+"F4.wireOp",EDGE,"E66.0.4.9")])]});
            var Q315;
            Q315=makeQuery(id+"F5.opExtrude","SWEPT_FACE",FACE,{"disambiguationData":[OSD([sQuery(id+"F4.wireOp",EDGE,"E76.0.2.1")])]});
            var Q316;
            Q316=makeQuery(id+"F5.opExtrude","SWEPT_FACE",FACE,{"disambiguationData":[OSD([sQuery(id+"F4.wireOp",EDGE,"E56.0.8.2")])]});
            var Q317;
            Q317=makeQuery(id+"F5.opExtrude","CAP_EDGE",EDGE,{"disambiguationData":[OSD([sQuery(id+"F4.wireOp",EDGE,"E55.0.1.0"),sQuery(id+"F4.wireOp",EDGE,"E74.bottom")])],"isStart":false});
            var Q318;
            Q318=makeQuery(id+"F5.opExtrude","CAP_EDGE",EDGE,{"disambiguationData":[OSD([sQuery(id+"F4.wireOp",EDGE,"E56.0.2.5")])],"isStart":false});
            var Q319;
            Q319=makeQuery(id+"F5.opExtrude","CAP_EDGE",EDGE,{"disambiguationData":[OSD([sQuery(id+"F4.wireOp",EDGE,"E56.0.4.1")])],"isStart":false});
            var Q320;
            Q320=makeQuery(id+"F5.opExtrude","CAP_EDGE",EDGE,{"disambiguationData":[OSD([sQuery(id+"F4.wireOp",EDGE,"E56.0.5.3")])],"isStart":false});
            var Q321;
            Q321=makeQuery(id+"F5.opExtrude","CAP_EDGE",EDGE,{"disambiguationData":[OSD([sQuery(id+"F4.wireOp",EDGE,"E56.0.6.5")])],"isStart":false});
            var Q322;
            Q322=makeQuery(id+"F5.opExtrude","CAP_EDGE",EDGE,{"disambiguationData":[OSD([sQuery(id+"F4.wireOp",EDGE,"E56.0.8.1")])],"isStart":false});
            var Q323;
            Q323=makeQuery(id+"F5.opExtrude","CAP_EDGE",EDGE,{"disambiguationData":[OSD([sQuery(id+"F4.wireOp",EDGE,"E56.0.9.3")])],"isStart":false});
            var Q324;
            Q324=makeQuery(id+"F5.opExtrude","SWEPT_FACE",FACE,{"disambiguationData":[OSD([sQuery(id+"F4.wireOp",EDGE,"E66.0.2.5")])]});
            var Q325;
            Q325=makeQuery(id+"F5.opExtrude","SWEPT_FACE",FACE,{"disambiguationData":[OSD([sQuery(id+"F4.wireOp",EDGE,"E76.0.2.3")])]});
            var Q326;
            Q326=makeQuery(id+"F5.opExtrude","SWEPT_FACE",FACE,{"disambiguationData":[OSD([sQuery(id+"F4.wireOp",EDGE,"E58")])]});
            var Q327;
            Q327=makeQuery(id+"F5.opExtrude","SWEPT_FACE",FACE,{"disambiguationData":[OSD([sQuery(id+"F4.wireOp",EDGE,"E66.0.2.8")])]});
            var Q328;
            Q328=makeQuery(id+"F5.opExtrude","SWEPT_FACE",FACE,{"disambiguationData":[OSD([sQuery(id+"F4.wireOp",EDGE,"E69")])]});
            var Q329;
            Q329=makeQuery(id+"F5.opExtrude","CAP_EDGE",EDGE,{"disambiguationData":[OSD([sQuery(id+"F4.wireOp",EDGE,"E66.0.3.9")])],"isStart":true});
            var Q330;
            Q330=makeQuery(id+"F5.opExtrude","CAP_EDGE",EDGE,{"disambiguationData":[OSD([sQuery(id+"F4.wireOp",EDGE,"E76.0.1.1")])],"isStart":true});
            var Q331;
            Q331=makeQuery(id+"F5.opExtrude","CAP_EDGE",EDGE,{"disambiguationData":[OSD([sQuery(id+"F4.wireOp",EDGE,"E76.0.3.5")])],"isStart":true});
            var Q332;
            Q332=makeQuery(id+"F5.opExtrude","CAP_EDGE",EDGE,{"disambiguationData":[OSD([sQuery(id+"F4.wireOp",EDGE,"E66.0.1.3")])],"isStart":true});
            var Q333;
            Q333=makeQuery(id+"F5.opExtrude","CAP_EDGE",EDGE,{"disambiguationData":[OSD([sQuery(id+"F4.wireOp",EDGE,"E66.0.4.0")])],"isStart":true});
            var Q334;
            Q334=makeQuery(id+"F5.opExtrude","CAP_EDGE",EDGE,{"disambiguationData":[OSD([sQuery(id+"F4.wireOp",EDGE,"E76.0.1.2")])],"isStart":true});
            var Q335;
            Q335=makeQuery(id+"F5.opExtrude","CAP_EDGE",EDGE,{"disambiguationData":[OSD([sQuery(id+"F4.wireOp",EDGE,"E66.0.4.2")])],"isStart":true});
            var Q336;
            Q336=makeQuery(id+"F5.opExtrude","CAP_EDGE",EDGE,{"disambiguationData":[OSD([sQuery(id+"F4.wireOp",EDGE,"E76.0.1.3")])],"isStart":true});
            var Q337;
            Q337=makeQuery(id+"F5.opExtrude","CAP_EDGE",EDGE,{"disambiguationData":[OSD([sQuery(id+"F4.wireOp",EDGE,"E76.0.4.1")])],"isStart":true});
            var Q338;
            Q338=makeQuery(id+"F5.opExtrude","CAP_EDGE",EDGE,{"disambiguationData":[OSD([sQuery(id+"F4.wireOp",EDGE,"E66.0.4.3")])],"isStart":true});
            var Q339;
            Q339=makeQuery(id+"F5.opExtrude","CAP_EDGE",EDGE,{"disambiguationData":[OSD([sQuery(id+"F4.wireOp",EDGE,"E76.0.1.4")])],"isStart":true});
            var Q340;
            Q340=makeQuery(id+"F5.opExtrude","CAP_EDGE",EDGE,{"disambiguationData":[OSD([sQuery(id+"F4.wireOp",EDGE,"E76.0.4.2")])],"isStart":true});
            var Q341;
            Q341=makeQuery(id+"F5.opExtrude","CAP_EDGE",EDGE,{"disambiguationData":[OSD([sQuery(id+"F4.wireOp",EDGE,"E76.0.1.5")])],"isStart":true});
            var Q342;
            Q342=makeQuery(id+"F5.opExtrude","CAP_EDGE",EDGE,{"disambiguationData":[OSD([sQuery(id+"F4.wireOp",EDGE,"E66.0.2.0")])],"isStart":true});
            var Q343;
            Q343=makeQuery(id+"F5.opExtrude","CAP_EDGE",EDGE,{"disambiguationData":[OSD([sQuery(id+"F4.wireOp",EDGE,"E76.0.4.4")])],"isStart":true});
            var Q344;
            Q344=makeQuery(id+"F5.opExtrude","CAP_EDGE",EDGE,{"disambiguationData":[OSD([sQuery(id+"F4.wireOp",EDGE,"E66.0.2.2")])],"isStart":true});
            var Q345;
            Q345=makeQuery(id+"F5.opExtrude","CAP_EDGE",EDGE,{"disambiguationData":[OSD([sQuery(id+"F4.wireOp",EDGE,"E66.0.4.9")])],"isStart":true});
            var Q346;
            Q346=makeQuery(id+"F5.opExtrude","CAP_EDGE",EDGE,{"disambiguationData":[OSD([sQuery(id+"F4.wireOp",EDGE,"E76.0.4.5")])],"isStart":true});
            var Q347;
            Q347=makeQuery(id+"F5.opExtrude","CAP_EDGE",EDGE,{"disambiguationData":[OSD([sQuery(id+"F4.wireOp",EDGE,"E66.0.2.3")])],"isStart":true});
            var Q348;
            Q348=makeQuery(id+"F5.opExtrude","CAP_EDGE",EDGE,{"disambiguationData":[OSD([sQuery(id+"F4.wireOp",EDGE,"E76.0.2.2")])],"isStart":true});
            var Q349;
            Q349=makeQuery(id+"F5.opExtrude","CAP_EDGE",EDGE,{"disambiguationData":[OSD([sQuery(id+"F4.wireOp",EDGE,"E68")])],"isStart":true});
            var Q350;
            Q350=makeQuery(id+"F5.opExtrude","CAP_EDGE",EDGE,{"disambiguationData":[OSD([sQuery(id+"F4.wireOp",EDGE,"E76.0.2.3")])],"isStart":true});
            var Q351;
            Q351=makeQuery(id+"F5.opExtrude","CAP_EDGE",EDGE,{"disambiguationData":[OSD([sQuery(id+"F4.wireOp",EDGE,"E69")])],"isStart":true});
            var Q352;
            Q352=makeQuery(id+"F5.opExtrude","CAP_EDGE",EDGE,{"disambiguationData":[OSD([sQuery(id+"F4.wireOp",EDGE,"E76.0.2.4")])],"isStart":true});
            var Q353;
            Q353=makeQuery(id+"F5.opExtrude","CAP_EDGE",EDGE,{"disambiguationData":[OSD([sQuery(id+"F4.wireOp",EDGE,"E66.0.2.9")])],"isStart":true});
            var Q354;
            Q354=makeQuery(id+"F5.opExtrude","CAP_EDGE",EDGE,{"disambiguationData":[OSD([sQuery(id+"F4.wireOp",EDGE,"E70")])],"isStart":true});
            var Q355;
            Q355=makeQuery(id+"F5.opExtrude","CAP_EDGE",EDGE,{"disambiguationData":[OSD([sQuery(id+"F4.wireOp",EDGE,"E76.0.2.5")])],"isStart":true});
            var Q356;
            Q356=makeQuery(id+"F5.opExtrude","CAP_EDGE",EDGE,{"disambiguationData":[OSD([sQuery(id+"F4.wireOp",EDGE,"E66.0.3.0")])],"isStart":true});
            var Q357;
            Q357=makeQuery(id+"F5.opExtrude","CAP_EDGE",EDGE,{"disambiguationData":[OSD([sQuery(id+"F4.wireOp",EDGE,"E71")])],"isStart":true});
            var Q358;
            Q358=makeQuery(id+"F5.opExtrude","CAP_EDGE",EDGE,{"disambiguationData":[OSD([sQuery(id+"F4.wireOp",EDGE,"E62")])],"isStart":true});
            var Q359;
            Q359=makeQuery(id+"F5.opExtrude","CAP_EDGE",EDGE,{"disambiguationData":[OSD([sQuery(id+"F4.wireOp",EDGE,"E66.0.3.2")])],"isStart":true});
            var Q360;
            Q360=makeQuery(id+"F5.opExtrude","CAP_EDGE",EDGE,{"disambiguationData":[OSD([sQuery(id+"F4.wireOp",EDGE,"E72")])],"isStart":true});
            var Q361;
            Q361=makeQuery(id+"F5.opExtrude","CAP_EDGE",EDGE,{"disambiguationData":[OSD([sQuery(id+"F4.wireOp",EDGE,"E76.0.3.1")])],"isStart":true});
            var Q362;
            Q362=makeQuery(id+"F5.opExtrude","CAP_EDGE",EDGE,{"disambiguationData":[OSD([sQuery(id+"F4.wireOp",EDGE,"E63")])],"isStart":true});
            var Q363;
            Q363=makeQuery(id+"F5.opExtrude","CAP_EDGE",EDGE,{"disambiguationData":[OSD([sQuery(id+"F4.wireOp",EDGE,"E66.0.3.3")])],"isStart":true});
            var Q364;
            Q364=makeQuery(id+"F5.opExtrude","CAP_EDGE",EDGE,{"disambiguationData":[OSD([sQuery(id+"F4.wireOp",EDGE,"E76.0.3.2")])],"isStart":true});
            var Q365;
            Q365=makeQuery(id+"F5.opExtrude","CAP_EDGE",EDGE,{"disambiguationData":[OSD([sQuery(id+"F4.wireOp",EDGE,"E64")])],"isStart":true});
            var Q366;
            Q366=makeQuery(id+"F5.opExtrude","CAP_EDGE",EDGE,{"disambiguationData":[OSD([sQuery(id+"F4.wireOp",EDGE,"E76.0.3.3")])],"isStart":true});
            var Q367;
            Q367=makeQuery(id+"F5.opExtrude","CAP_EDGE",EDGE,{"disambiguationData":[OSD([sQuery(id+"F4.wireOp",EDGE,"E66.0.1.0")])],"isStart":true});
            var Q368;
            Q368=makeQuery(id+"F5.opExtrude","CAP_EDGE",EDGE,{"disambiguationData":[OSD([sQuery(id+"F4.wireOp",EDGE,"E76.0.3.4")])],"isStart":true});
            var Q369;
            Q369=makeQuery(id+"F3.boolean.opBoolean","COPY",EDGE,{"derivedFrom":makeQuery(id+"F3.opExtrude","SWEPT_EDGE",EDGE,{"disambiguationData":[OSD([sQuery(id+"F2.wireOp",EDGE,"E9.top"),sQuery(id+"F2.wireOp",EDGE,"E13.filletArc")])]})});
            var Q370;
            Q370=makeQuery(id+"F3.boolean.opBoolean","COPY",EDGE,{"derivedFrom":makeQuery(id+"F3.opExtrude","SWEPT_EDGE",EDGE,{"disambiguationData":[OSD([sQuery(id+"F2.wireOp",EDGE,"E14.0.1.0"),sQuery(id+"F2.wireOp",EDGE,"E49.filletArc")])]})});
            var Q371;
            Q371=makeQuery(id+"F3.boolean.opBoolean","COPY",EDGE,{"derivedFrom":makeQuery(id+"F3.opExtrude","SWEPT_EDGE",EDGE,{"disambiguationData":[OSD([sQuery(id+"F2.wireOp",EDGE,"E5.bottom"),sQuery(id+"F2.wireOp",EDGE,"E6.filletArc")])]})});
            var Q372;
            Q372=makeQuery(id+"F3.boolean.opBoolean","COPY",EDGE,{"derivedFrom":makeQuery(id+"F3.opExtrude","SWEPT_EDGE",EDGE,{"disambiguationData":[OSD([sQuery(id+"F2.wireOp",EDGE,"E5.bottom"),sQuery(id+"F2.wireOp",EDGE,"E7.filletArc")])]})});
            var Q373;
            Q373=makeQuery(id+"F3.boolean.opBoolean","COPY",EDGE,{"derivedFrom":makeQuery(id+"F3.opExtrude","SWEPT_EDGE",EDGE,{"disambiguationData":[OSD([sQuery(id+"F2.wireOp",EDGE,"E5.right"),sQuery(id+"F2.wireOp",EDGE,"E7.filletArc")])]})});
            var Q374;
            Q374=makeQuery(id+"F3.boolean.opBoolean","COPY",EDGE,{"derivedFrom":makeQuery(id+"F3.opExtrude","SWEPT_EDGE",EDGE,{"disambiguationData":[OSD([sQuery(id+"F2.wireOp",EDGE,"E5.right"),sQuery(id+"F2.wireOp",EDGE,"E41.filletArc")])]})});
            var Q375;
            Q375=makeQuery(id+"F3.boolean.opBoolean","COPY",EDGE,{"derivedFrom":makeQuery(id+"F3.opExtrude","SWEPT_EDGE",EDGE,{"disambiguationData":[OSD([sQuery(id+"F2.wireOp",EDGE,"E8.bottom"),sQuery(id+"F2.wireOp",EDGE,"E50.filletArc")])]})});
            var Q376;
            Q376=makeQuery(id+"F3.boolean.opBoolean","COPY",EDGE,{"derivedFrom":makeQuery(id+"F3.opExtrude","SWEPT_EDGE",EDGE,{"disambiguationData":[OSD([sQuery(id+"F2.wireOp",EDGE,"E8.top"),sQuery(id+"F2.wireOp",EDGE,"E51.filletArc")])]})});
            var Q377;
            Q377=makeQuery(id+"F3.boolean.opBoolean","COPY",EDGE,{"derivedFrom":makeQuery(id+"F3.opExtrude","SWEPT_EDGE",EDGE,{"disambiguationData":[OSD([sQuery(id+"F2.wireOp",EDGE,"E8.top"),sQuery(id+"F2.wireOp",EDGE,"E11.filletArc")])]})});
            var Q378;
            Q378=makeQuery(id+"F3.boolean.opBoolean","COPY",FACE,{"derivedFrom":makeQuery(id+"F3.opExtrude","SWEPT_FACE",FACE,{"disambiguationData":[OSD([sQuery(id+"F2.wireOp",EDGE,"E10.filletArc"),sQuery(id+"F2.wireOp",EDGE,"E11.filletArc")])]})});
            var Q379;
            Q379=makeQuery(id+"F3.boolean.opBoolean","COPY",EDGE,{"derivedFrom":makeQuery(id+"F3.opExtrude","SWEPT_EDGE",EDGE,{"disambiguationData":[OSD([sQuery(id+"F2.wireOp",EDGE,"E9.bottom"),sQuery(id+"F2.wireOp",EDGE,"E12.filletArc")])]})});
            var Q380;
            Q380=makeQuery(id+"F5.opExtrude","SWEPT_EDGE",EDGE,{"disambiguationData":[OSD([sQuery(id+"F4.wireOp",EDGE,"E56.0.1.2"),sQuery(id+"F4.wireOp",EDGE,"E62")])]});
            var Q381;
            Q381=makeQuery(id+"F5.opExtrude","SWEPT_EDGE",EDGE,{"disambiguationData":[OSD([sQuery(id+"F4.wireOp",EDGE,"E56.0.1.2"),sQuery(id+"F4.wireOp",EDGE,"E69")])]});
            var Q382;
            Q382=makeQuery(id+"F5.opExtrude","SWEPT_EDGE",EDGE,{"disambiguationData":[OSD([sQuery(id+"F4.wireOp",EDGE,"E54.top"),sQuery(id+"F4.wireOp",EDGE,"E54.left"),sQuery(id+"F4.wireOp",EDGE,"E64")])]});
            var Q383;
            Q383=makeQuery(id+"F5.opExtrude","SWEPT_EDGE",EDGE,{"disambiguationData":[OSD([sQuery(id+"F4.wireOp",EDGE,"E55.0.1.0"),sQuery(id+"F4.wireOp",EDGE,"E55.0.1.3"),sQuery(id+"F4.wireOp",EDGE,"E61")])]});
            var Q384;
            Q384=makeQuery(id+"F5.opExtrude","SWEPT_FACE",FACE,{"disambiguationData":[OSD([sQuery(id+"F4.wireOp",EDGE,"E54.right")])]});
            var Q385;
            Q385=makeQuery(id+"F5.opExtrude","SWEPT_EDGE",EDGE,{"disambiguationData":[OSD([sQuery(id+"F4.wireOp",EDGE,"E55.0.1.1"),sQuery(id+"F4.wireOp",EDGE,"E55.0.1.3"),sQuery(id+"F4.wireOp",EDGE,"E62")])]});
            var Q386;
            Q386=makeQuery(id+"F5.opExtrude","SWEPT_EDGE",EDGE,{"disambiguationData":[OSD([sQuery(id+"F4.wireOp",EDGE,"E55.0.2.0"),sQuery(id+"F4.wireOp",EDGE,"E55.0.2.3"),sQuery(id+"F4.wireOp",EDGE,"E58")])]});
            var Q387;
            Q387=makeQuery(id+"F5.opExtrude","SWEPT_EDGE",EDGE,{"disambiguationData":[OSD([sQuery(id+"F4.wireOp",EDGE,"E56.0.1.0"),sQuery(id+"F4.wireOp",EDGE,"E63")])]});
            var Q388;
            Q388=makeQuery(id+"F5.opExtrude","SWEPT_EDGE",EDGE,{"disambiguationData":[OSD([sQuery(id+"F4.wireOp",EDGE,"E56.0.1.1"),sQuery(id+"F4.wireOp",EDGE,"E56.0.1.13"),sQuery(id+"F4.wireOp",EDGE,"E59")])]});
            var Q389;
            Q389=makeQuery(id+"F5.opExtrude","CAP_EDGE",EDGE,{"disambiguationData":[OSD([sQuery(id+"F4.wireOp",EDGE,"E56.0.1.5")])],"isStart":true});
            var Q390;
            Q390=makeQuery(id+"F5.opExtrude","CAP_EDGE",EDGE,{"disambiguationData":[OSD([sQuery(id+"F4.wireOp",EDGE,"E56.0.2.1")])],"isStart":true});
            var Q391;
            Q391=makeQuery(id+"F5.opExtrude","CAP_EDGE",EDGE,{"disambiguationData":[OSD([sQuery(id+"F4.wireOp",EDGE,"E55.0.1.0"),sQuery(id+"F4.wireOp",EDGE,"E74.bottom")])],"isStart":true});
            var Q392;
            Q392=makeQuery(id+"F5.opExtrude","CAP_EDGE",EDGE,{"disambiguationData":[OSD([sQuery(id+"F4.wireOp",EDGE,"E55.0.1.1"),sQuery(id+"F4.wireOp",EDGE,"E74.top")])],"isStart":true});
            var Q393;
            Q393=makeQuery(id+"F5.opExtrude","CAP_EDGE",EDGE,{"disambiguationData":[OSD([sQuery(id+"F4.wireOp",EDGE,"E56.0.1.2")])],"isStart":true});
            var Q394;
            Q394=makeQuery(id+"F3.boolean.opBoolean","COPY",EDGE,{"derivedFrom":makeQuery(id+"F3.opExtrude","SWEPT_EDGE",EDGE,{"disambiguationData":[OSD([sQuery(id+"F2.wireOp",EDGE,"E14.0.2.4"),sQuery(id+"F2.wireOp",EDGE,"E38.filletArc")])]})});
            var Q395;
            Q395=makeQuery(id+"F3.boolean.opBoolean","COPY",EDGE,{"derivedFrom":makeQuery(id+"F3.opExtrude","SWEPT_EDGE",EDGE,{"disambiguationData":[OSD([sQuery(id+"F2.wireOp",EDGE,"E14.0.4.4"),sQuery(id+"F2.wireOp",EDGE,"E34.filletArc")])]})});
            var Q396;
            Q396=makeQuery(id+"F3.boolean.opBoolean","COPY",EDGE,{"derivedFrom":makeQuery(id+"F3.opExtrude","SWEPT_EDGE",EDGE,{"disambiguationData":[OSD([sQuery(id+"F2.wireOp",EDGE,"E24.trimOffspring"),sQuery(id+"F2.wireOp",EDGE,"E45.filletArc")])]})});
            var Q397;
            Q397=makeQuery(id+"F3.boolean.opBoolean","COPY",EDGE,{"derivedFrom":makeQuery(id+"F3.opExtrude","CAP_EDGE",EDGE,{"disambiguationData":[OSD([sQuery(id+"F2.wireOp",EDGE,"E5.right")])],"isStart":false})});
            var Q398;
            Q398=makeQuery(id+"F3.boolean.opBoolean","COPY",EDGE,{"derivedFrom":makeQuery(id+"F3.opExtrude","CAP_EDGE",EDGE,{"disambiguationData":[OSD([sQuery(id+"F2.wireOp",EDGE,"E14.0.2.1")])],"isStart":false})});
            var Q399;
            Q399=makeQuery(id+"F3.boolean.opBoolean","COPY",EDGE,{"derivedFrom":makeQuery(id+"F3.opExtrude","CAP_EDGE",EDGE,{"disambiguationData":[OSD([sQuery(id+"F2.wireOp",EDGE,"E14.0.3.4")])],"isStart":false})});
            var Q400;
            Q400=makeQuery(id+"F3.boolean.opBoolean","COPY",EDGE,{"derivedFrom":makeQuery(id+"F3.opExtrude","CAP_EDGE",EDGE,{"disambiguationData":[OSD([sQuery(id+"F2.wireOp",EDGE,"E24.trimOffspring")])],"isStart":false})});
            var Q401;
            Q401=makeQuery(id+"F3.boolean.opBoolean","COPY",EDGE,{"derivedFrom":makeQuery(id+"F3.opExtrude","CAP_EDGE",EDGE,{"disambiguationData":[OSD([sQuery(id+"F2.wireOp",EDGE,"E41.filletArc")])],"isStart":false})});
            var Q402;
            Q402=makeQuery(id+"F3.boolean.opBoolean","COPY",EDGE,{"derivedFrom":makeQuery(id+"F3.opExtrude","SWEPT_EDGE",EDGE,{"disambiguationData":[OSD([sQuery(id+"F2.wireOp",EDGE,"E14.0.2.4"),sQuery(id+"F2.wireOp",EDGE,"E14.0.2.13")])]})});
            var Q403;
            Q403=makeQuery(id+"F3.boolean.opBoolean","COPY",EDGE,{"derivedFrom":makeQuery(id+"F3.opExtrude","SWEPT_EDGE",EDGE,{"disambiguationData":[OSD([sQuery(id+"F2.wireOp",EDGE,"E14.0.4.4"),sQuery(id+"F2.wireOp",EDGE,"E14.0.4.13")])]})});
            var Q404;
            Q404=makeQuery(id+"F3.boolean.opBoolean","COPY",EDGE,{"derivedFrom":makeQuery(id+"F3.opExtrude","SWEPT_EDGE",EDGE,{"disambiguationData":[OSD([sQuery(id+"F2.wireOp",EDGE,"E24.trimOffspring"),sQuery(id+"F2.wireOp",EDGE,"E44.filletArc")])]})});
            var Q405;
            Q405=makeQuery(id+"F3.boolean.opBoolean","COPY",EDGE,{"derivedFrom":makeQuery(id+"F3.opExtrude","SWEPT_EDGE",EDGE,{"disambiguationData":[OSD([sQuery(id+"F2.wireOp",EDGE,"E14.0.3.0"),sQuery(id+"F2.wireOp",EDGE,"E37.filletArc")])]})});
            var Q406;
            Q406=makeQuery(id+"F3.boolean.opBoolean","COPY",EDGE,{"derivedFrom":makeQuery(id+"F3.opExtrude","SWEPT_EDGE",EDGE,{"disambiguationData":[OSD([sQuery(id+"F2.wireOp",EDGE,"E26.filletArc"),sQuery(id+"F2.wireOp",EDGE,"E30")])]})});
            var Q407;
            Q407=makeQuery(id+"F3.boolean.opBoolean","COPY",EDGE,{"derivedFrom":makeQuery(id+"F3.opExtrude","CAP_EDGE",EDGE,{"disambiguationData":[OSD([sQuery(id+"F2.wireOp",EDGE,"E14.0.1.0")])],"isStart":false})});
            var Q408;
            Q408=makeQuery(id+"F3.boolean.opBoolean","COPY",EDGE,{"derivedFrom":makeQuery(id+"F3.opExtrude","CAP_EDGE",EDGE,{"disambiguationData":[OSD([sQuery(id+"F2.wireOp",EDGE,"E14.0.2.3")])],"isStart":false})});
            var Q409;
            Q409=makeQuery(id+"F3.boolean.opBoolean","COPY",EDGE,{"derivedFrom":makeQuery(id+"F3.opExtrude","CAP_EDGE",EDGE,{"disambiguationData":[OSD([sQuery(id+"F2.wireOp",EDGE,"E42.filletArc")])],"isStart":false})});
            var Q410;
            Q410=makeQuery(id+"F3.boolean.opBoolean","COPY",EDGE,{"derivedFrom":makeQuery(id+"F3.opExtrude","SWEPT_EDGE",EDGE,{"disambiguationData":[OSD([sQuery(id+"F2.wireOp",EDGE,"E14.0.1.0"),sQuery(id+"F2.wireOp",EDGE,"E14.0.1.12")])]})});
            var Q411;
            Q411=makeQuery(id+"F3.boolean.opBoolean","COPY",EDGE,{"derivedFrom":makeQuery(id+"F3.opExtrude","SWEPT_EDGE",EDGE,{"disambiguationData":[OSD([sQuery(id+"F2.wireOp",EDGE,"E14.0.3.0"),sQuery(id+"F2.wireOp",EDGE,"E14.0.3.12")])]})});
            var Q412;
            Q412=makeQuery(id+"F3.boolean.opBoolean","COPY",EDGE,{"derivedFrom":makeQuery(id+"F3.opExtrude","SWEPT_EDGE",EDGE,{"disambiguationData":[OSD([sQuery(id+"F2.wireOp",EDGE,"E27.trimOffspring"),sQuery(id+"F2.wireOp",EDGE,"E46.filletArc")])]})});
            var Q413;
            Q413=makeQuery(id+"F3.boolean.opBoolean","COPY",FACE,{"derivedFrom":makeQuery(id+"F3.opExtrude","SWEPT_FACE",FACE,{"disambiguationData":[OSD([sQuery(id+"F2.wireOp",EDGE,"E14.0.1.10"),sQuery(id+"F2.wireOp",EDGE,"E14.0.1.11")])]})});
            var Q414;
            Q414=makeQuery(id+"F3.boolean.opBoolean","COPY",EDGE,{"derivedFrom":makeQuery(id+"F3.opExtrude","SWEPT_EDGE",EDGE,{"disambiguationData":[OSD([sQuery(id+"F2.wireOp",EDGE,"E14.0.1.1"),sQuery(id+"F2.wireOp",EDGE,"E47.filletArc")])]})});
            var Q415;
            Q415=makeQuery(id+"F3.boolean.opBoolean","COPY",EDGE,{"derivedFrom":makeQuery(id+"F3.opExtrude","SWEPT_EDGE",EDGE,{"disambiguationData":[OSD([sQuery(id+"F2.wireOp",EDGE,"E14.0.3.1"),sQuery(id+"F2.wireOp",EDGE,"E43.filletArc")])]})});
            var Q416;
            Q416=makeQuery(id+"F3.boolean.opBoolean","COPY",EDGE,{"derivedFrom":makeQuery(id+"F3.opExtrude","SWEPT_EDGE",EDGE,{"disambiguationData":[OSD([sQuery(id+"F2.wireOp",EDGE,"E27.trimOffspring"),sQuery(id+"F2.wireOp",EDGE,"E47.filletArc")])]})});
            var Q417;
            Q417=makeQuery(id+"F3.boolean.opBoolean","COPY",EDGE,{"derivedFrom":makeQuery(id+"F3.opExtrude","CAP_EDGE",EDGE,{"disambiguationData":[OSD([sQuery(id+"F2.wireOp",EDGE,"E7.filletArc")])],"isStart":false})});
            var Q418;
            Q418=makeQuery(id+"F3.boolean.opBoolean","COPY",EDGE,{"derivedFrom":makeQuery(id+"F3.opExtrude","CAP_EDGE",EDGE,{"disambiguationData":[OSD([sQuery(id+"F2.wireOp",EDGE,"E14.0.1.1")])],"isStart":false})});
            var Q419;
            Q419=makeQuery(id+"F3.boolean.opBoolean","COPY",EDGE,{"derivedFrom":makeQuery(id+"F3.opExtrude","CAP_EDGE",EDGE,{"disambiguationData":[OSD([sQuery(id+"F2.wireOp",EDGE,"E14.0.2.4")])],"isStart":false})});
            var Q420;
            Q420=makeQuery(id+"F3.boolean.opBoolean","COPY",EDGE,{"derivedFrom":makeQuery(id+"F3.opExtrude","CAP_EDGE",EDGE,{"disambiguationData":[OSD([sQuery(id+"F2.wireOp",EDGE,"E43.filletArc")])],"isStart":false})});
            var Q421;
            Q421=makeQuery(id+"F3.boolean.opBoolean","COPY",EDGE,{"derivedFrom":makeQuery(id+"F3.opExtrude","SWEPT_EDGE",EDGE,{"disambiguationData":[OSD([sQuery(id+"F2.wireOp",EDGE,"E14.0.1.1"),sQuery(id+"F2.wireOp",EDGE,"E14.0.1.11")])]})});
            var Q422;
            Q422=makeQuery(id+"F3.boolean.opBoolean","COPY",EDGE,{"derivedFrom":makeQuery(id+"F3.opExtrude","SWEPT_EDGE",EDGE,{"disambiguationData":[OSD([sQuery(id+"F2.wireOp",EDGE,"E14.0.3.1"),sQuery(id+"F2.wireOp",EDGE,"E14.0.3.11")])]})});
            var Q423;
            Q423=makeQuery(id+"F3.boolean.opBoolean","COPY",FACE,{"derivedFrom":makeQuery(id+"F3.opExtrude","SWEPT_FACE",FACE,{"disambiguationData":[OSD([sQuery(id+"F2.wireOp",EDGE,"E14.0.4.10"),sQuery(id+"F2.wireOp",EDGE,"E14.0.4.11")])]})});
            var Q424;
            Q424=makeQuery(id+"F3.boolean.opBoolean","COPY",EDGE,{"derivedFrom":makeQuery(id+"F3.opExtrude","SWEPT_EDGE",EDGE,{"disambiguationData":[OSD([sQuery(id+"F2.wireOp",EDGE,"E14.0.1.3"),sQuery(id+"F2.wireOp",EDGE,"E52.filletArc")])]})});
            var Q425;
            Q425=makeQuery(id+"F3.boolean.opBoolean","COPY",EDGE,{"derivedFrom":makeQuery(id+"F3.opExtrude","SWEPT_EDGE",EDGE,{"disambiguationData":[OSD([sQuery(id+"F2.wireOp",EDGE,"E14.0.3.3"),sQuery(id+"F2.wireOp",EDGE,"E45.filletArc")])]})});
            var Q426;
            Q426=makeQuery(id+"F3.boolean.opBoolean","COPY",EDGE,{"derivedFrom":makeQuery(id+"F3.opExtrude","CAP_EDGE",EDGE,{"disambiguationData":[OSD([sQuery(id+"F2.wireOp",EDGE,"E8.bottom")])],"isStart":false})});
            var Q427;
            Q427=makeQuery(id+"F3.boolean.opBoolean","COPY",EDGE,{"derivedFrom":makeQuery(id+"F3.opExtrude","CAP_EDGE",EDGE,{"disambiguationData":[OSD([sQuery(id+"F2.wireOp",EDGE,"E14.0.1.3")])],"isStart":false})});
            var Q428;
            Q428=makeQuery(id+"F3.boolean.opBoolean","COPY",EDGE,{"derivedFrom":makeQuery(id+"F3.opExtrude","CAP_EDGE",EDGE,{"disambiguationData":[OSD([sQuery(id+"F2.wireOp",EDGE,"E14.0.4.0")])],"isStart":false})});
            var Q429;
            Q429=makeQuery(id+"F3.boolean.opBoolean","COPY",EDGE,{"derivedFrom":makeQuery(id+"F3.opExtrude","CAP_EDGE",EDGE,{"disambiguationData":[OSD([sQuery(id+"F2.wireOp",EDGE,"E27.trimOffspring")])],"isStart":false})});
            var Q430;
            Q430=makeQuery(id+"F3.boolean.opBoolean","COPY",EDGE,{"derivedFrom":makeQuery(id+"F3.opExtrude","CAP_EDGE",EDGE,{"disambiguationData":[OSD([sQuery(id+"F2.wireOp",EDGE,"E44.filletArc")])],"isStart":false})});
            var Q431;
            Q431=makeQuery(id+"F3.boolean.opBoolean","COPY",EDGE,{"derivedFrom":makeQuery(id+"F3.opExtrude","SWEPT_EDGE",EDGE,{"disambiguationData":[OSD([sQuery(id+"F2.wireOp",EDGE,"E14.0.1.3"),sQuery(id+"F2.wireOp",EDGE,"E14.0.1.10")])]})});
            var Q432;
            Q432=makeQuery(id+"F3.boolean.opBoolean","COPY",EDGE,{"derivedFrom":makeQuery(id+"F3.opExtrude","SWEPT_EDGE",EDGE,{"disambiguationData":[OSD([sQuery(id+"F2.wireOp",EDGE,"E14.0.3.3"),sQuery(id+"F2.wireOp",EDGE,"E14.0.3.10")])]})});
            var Q433;
            Q433=makeQuery(id+"F3.boolean.opBoolean","COPY",EDGE,{"derivedFrom":makeQuery(id+"F3.opExtrude","SWEPT_EDGE",EDGE,{"disambiguationData":[OSD([sQuery(id+"F2.wireOp",EDGE,"E14.0.1.4"),sQuery(id+"F2.wireOp",EDGE,"E40.filletArc")])]})});
            var Q434;
            Q434=makeQuery(id+"F3.boolean.opBoolean","COPY",EDGE,{"derivedFrom":makeQuery(id+"F3.opExtrude","SWEPT_EDGE",EDGE,{"disambiguationData":[OSD([sQuery(id+"F2.wireOp",EDGE,"E14.0.3.4"),sQuery(id+"F2.wireOp",EDGE,"E36.filletArc")])]})});
            var Q435;
            Q435=makeQuery(id+"F3.boolean.opBoolean","COPY",EDGE,{"derivedFrom":makeQuery(id+"F3.opExtrude","CAP_EDGE",EDGE,{"disambiguationData":[OSD([sQuery(id+"F2.wireOp",EDGE,"E8.top")])],"isStart":false})});
            var Q436;
            Q436=makeQuery(id+"F3.boolean.opBoolean","COPY",EDGE,{"derivedFrom":makeQuery(id+"F3.opExtrude","CAP_EDGE",EDGE,{"disambiguationData":[OSD([sQuery(id+"F2.wireOp",EDGE,"E14.0.1.4")])],"isStart":false})});
            var Q437;
            Q437=makeQuery(id+"F3.boolean.opBoolean","COPY",EDGE,{"derivedFrom":makeQuery(id+"F3.opExtrude","CAP_EDGE",EDGE,{"disambiguationData":[OSD([sQuery(id+"F2.wireOp",EDGE,"E14.0.4.1")])],"isStart":false})});
            var Q438;
            Q438=makeQuery(id+"F3.boolean.opBoolean","COPY",EDGE,{"derivedFrom":makeQuery(id+"F3.opExtrude","CAP_EDGE",EDGE,{"disambiguationData":[OSD([sQuery(id+"F2.wireOp",EDGE,"E45.filletArc")])],"isStart":false})});
            var Q439;
            Q439=makeQuery(id+"F3.boolean.opBoolean","COPY",EDGE,{"derivedFrom":makeQuery(id+"F3.opExtrude","SWEPT_EDGE",EDGE,{"disambiguationData":[OSD([sQuery(id+"F2.wireOp",EDGE,"E14.0.1.4"),sQuery(id+"F2.wireOp",EDGE,"E14.0.1.13")])]})});
            var Q440;
            Q440=makeQuery(id+"F3.boolean.opBoolean","COPY",EDGE,{"derivedFrom":makeQuery(id+"F3.opExtrude","SWEPT_EDGE",EDGE,{"disambiguationData":[OSD([sQuery(id+"F2.wireOp",EDGE,"E14.0.3.4"),sQuery(id+"F2.wireOp",EDGE,"E14.0.3.13")])]})});
            var Q441;
            Q441=makeQuery(id+"F3.boolean.opBoolean","COPY",FACE,{"derivedFrom":makeQuery(id+"F3.opExtrude","SWEPT_FACE",FACE,{"disambiguationData":[OSD([sQuery(id+"F2.wireOp",EDGE,"E14.0.2.10"),sQuery(id+"F2.wireOp",EDGE,"E14.0.2.11")])]})});
            var Q442;
            Q442=makeQuery(id+"F3.boolean.opBoolean","COPY",EDGE,{"derivedFrom":makeQuery(id+"F3.opExtrude","SWEPT_EDGE",EDGE,{"disambiguationData":[OSD([sQuery(id+"F2.wireOp",EDGE,"E14.0.2.0"),sQuery(id+"F2.wireOp",EDGE,"E39.filletArc")])]})});
            var Q443;
            Q443=makeQuery(id+"F3.boolean.opBoolean","COPY",EDGE,{"derivedFrom":makeQuery(id+"F3.opExtrude","SWEPT_EDGE",EDGE,{"disambiguationData":[OSD([sQuery(id+"F2.wireOp",EDGE,"E14.0.4.0"),sQuery(id+"F2.wireOp",EDGE,"E35.filletArc")])]})});
            var Q444;
            Q444=makeQuery(id+"F3.boolean.opBoolean","COPY",EDGE,{"derivedFrom":makeQuery(id+"F3.opExtrude","CAP_EDGE",EDGE,{"disambiguationData":[OSD([sQuery(id+"F2.wireOp",EDGE,"E9.bottom")])],"isStart":false})});
            var Q445;
            Q445=makeQuery(id+"F3.boolean.opBoolean","COPY",EDGE,{"derivedFrom":makeQuery(id+"F3.opExtrude","CAP_EDGE",EDGE,{"disambiguationData":[OSD([sQuery(id+"F2.wireOp",EDGE,"E14.0.3.0")])],"isStart":false})});
            var Q446;
            Q446=makeQuery(id+"F3.boolean.opBoolean","COPY",EDGE,{"derivedFrom":makeQuery(id+"F3.opExtrude","CAP_EDGE",EDGE,{"disambiguationData":[OSD([sQuery(id+"F2.wireOp",EDGE,"E14.0.4.3")])],"isStart":false})});
            var Q447;
            Q447=makeQuery(id+"F3.boolean.opBoolean","COPY",EDGE,{"derivedFrom":makeQuery(id+"F3.opExtrude","CAP_EDGE",EDGE,{"disambiguationData":[OSD([sQuery(id+"F2.wireOp",EDGE,"E46.filletArc")])],"isStart":false})});
            var Q448;
            Q448=makeQuery(id+"F3.boolean.opBoolean","COPY",EDGE,{"derivedFrom":makeQuery(id+"F3.opExtrude","SWEPT_EDGE",EDGE,{"disambiguationData":[OSD([sQuery(id+"F2.wireOp",EDGE,"E14.0.2.0"),sQuery(id+"F2.wireOp",EDGE,"E14.0.2.12")])]})});
            var Q449;
            Q449=makeQuery(id+"F3.boolean.opBoolean","COPY",EDGE,{"derivedFrom":makeQuery(id+"F3.opExtrude","SWEPT_EDGE",EDGE,{"disambiguationData":[OSD([sQuery(id+"F2.wireOp",EDGE,"E14.0.4.0"),sQuery(id+"F2.wireOp",EDGE,"E14.0.4.12")])]})});
            var Q450;
            Q450=makeQuery(id+"F3.boolean.opBoolean","COPY",EDGE,{"derivedFrom":makeQuery(id+"F3.opExtrude","SWEPT_EDGE",EDGE,{"disambiguationData":[OSD([sQuery(id+"F2.wireOp",EDGE,"E14.0.2.1"),sQuery(id+"F2.wireOp",EDGE,"E44.filletArc")])]})});
            var Q451;
            Q451=makeQuery(id+"F3.boolean.opBoolean","COPY",EDGE,{"derivedFrom":makeQuery(id+"F3.opExtrude","SWEPT_EDGE",EDGE,{"disambiguationData":[OSD([sQuery(id+"F2.wireOp",EDGE,"E14.0.4.1"),sQuery(id+"F2.wireOp",EDGE,"E41.filletArc")])]})});
            var Q452;
            Q452=makeQuery(id+"F3.boolean.opBoolean","COPY",EDGE,{"derivedFrom":makeQuery(id+"F3.opExtrude","SWEPT_EDGE",EDGE,{"disambiguationData":[OSD([sQuery(id+"F2.wireOp",EDGE,"E22.trimOffspring"),sQuery(id+"F2.wireOp",EDGE,"E52.filletArc")])]})});
            var Q453;
            Q453=makeQuery(id+"F3.boolean.opBoolean","COPY",EDGE,{"derivedFrom":makeQuery(id+"F3.opExtrude","CAP_EDGE",EDGE,{"disambiguationData":[OSD([sQuery(id+"F2.wireOp",EDGE,"E5.bottom")])],"isStart":false})});
            var Q454;
            Q454=makeQuery(id+"F3.boolean.opBoolean","COPY",EDGE,{"derivedFrom":makeQuery(id+"F3.opExtrude","CAP_EDGE",EDGE,{"disambiguationData":[OSD([sQuery(id+"F2.wireOp",EDGE,"E9.top")])],"isStart":false})});
            var Q455;
            Q455=makeQuery(id+"F3.boolean.opBoolean","COPY",EDGE,{"derivedFrom":makeQuery(id+"F3.opExtrude","CAP_EDGE",EDGE,{"disambiguationData":[OSD([sQuery(id+"F2.wireOp",EDGE,"E14.0.3.1")])],"isStart":false})});
            var Q456;
            Q456=makeQuery(id+"F3.boolean.opBoolean","COPY",EDGE,{"derivedFrom":makeQuery(id+"F3.opExtrude","CAP_EDGE",EDGE,{"disambiguationData":[OSD([sQuery(id+"F2.wireOp",EDGE,"E14.0.4.4")])],"isStart":false})});
            var Q457;
            Q457=makeQuery(id+"F3.boolean.opBoolean","COPY",EDGE,{"derivedFrom":makeQuery(id+"F3.opExtrude","CAP_EDGE",EDGE,{"disambiguationData":[OSD([sQuery(id+"F2.wireOp",EDGE,"E22.trimOffspring")])],"isStart":false})});
            var Q458;
            Q458=makeQuery(id+"F3.boolean.opBoolean","COPY",EDGE,{"derivedFrom":makeQuery(id+"F3.opExtrude","SWEPT_EDGE",EDGE,{"disambiguationData":[OSD([sQuery(id+"F2.wireOp",EDGE,"E14.0.2.1"),sQuery(id+"F2.wireOp",EDGE,"E14.0.2.11")])]})});
            var Q459;
            Q459=makeQuery(id+"F3.boolean.opBoolean","COPY",EDGE,{"derivedFrom":makeQuery(id+"F3.opExtrude","SWEPT_EDGE",EDGE,{"disambiguationData":[OSD([sQuery(id+"F2.wireOp",EDGE,"E14.0.4.1"),sQuery(id+"F2.wireOp",EDGE,"E14.0.4.11")])]})});
            var Q460;
            Q460=makeQuery(id+"F3.boolean.opBoolean","COPY",EDGE,{"derivedFrom":makeQuery(id+"F3.opExtrude","SWEPT_EDGE",EDGE,{"disambiguationData":[OSD([sQuery(id+"F2.wireOp",EDGE,"E22.trimOffspring"),sQuery(id+"F2.wireOp",EDGE,"E48.filletArc")])]})});
            var Q461;
            Q461=makeQuery(id+"F3.boolean.opBoolean","COPY",EDGE,{"derivedFrom":makeQuery(id+"F3.opExtrude","SWEPT_EDGE",EDGE,{"disambiguationData":[OSD([sQuery(id+"F2.wireOp",EDGE,"E14.0.2.3"),sQuery(id+"F2.wireOp",EDGE,"E46.filletArc")])]})});
            var Q462;
            Q462=makeQuery(id+"F3.boolean.opBoolean","COPY",EDGE,{"derivedFrom":makeQuery(id+"F3.opExtrude","SWEPT_EDGE",EDGE,{"disambiguationData":[OSD([sQuery(id+"F2.wireOp",EDGE,"E14.0.4.3"),sQuery(id+"F2.wireOp",EDGE,"E42.filletArc")])]})});
            var Q463;
            Q463=makeQuery(id+"F3.boolean.opBoolean","COPY",EDGE,{"derivedFrom":makeQuery(id+"F3.opExtrude","SWEPT_EDGE",EDGE,{"disambiguationData":[OSD([sQuery(id+"F2.wireOp",EDGE,"E23.trimOffspring"),sQuery(id+"F2.wireOp",EDGE,"E42.filletArc")])]})});
            var Q464;
            Q464=makeQuery(id+"F3.boolean.opBoolean","COPY",EDGE,{"derivedFrom":makeQuery(id+"F3.opExtrude","CAP_EDGE",EDGE,{"disambiguationData":[OSD([sQuery(id+"F2.wireOp",EDGE,"E14.0.2.0")])],"isStart":false})});
            var Q465;
            Q465=makeQuery(id+"F3.boolean.opBoolean","COPY",EDGE,{"derivedFrom":makeQuery(id+"F3.opExtrude","CAP_EDGE",EDGE,{"disambiguationData":[OSD([sQuery(id+"F2.wireOp",EDGE,"E14.0.3.3")])],"isStart":false})});
            var Q466;
            Q466=makeQuery(id+"F3.boolean.opBoolean","COPY",EDGE,{"derivedFrom":makeQuery(id+"F3.opExtrude","CAP_EDGE",EDGE,{"disambiguationData":[OSD([sQuery(id+"F2.wireOp",EDGE,"E23.trimOffspring")])],"isStart":false})});
            var Q467;
            Q467=makeQuery(id+"F3.boolean.opBoolean","COPY",EDGE,{"derivedFrom":makeQuery(id+"F3.opExtrude","SWEPT_EDGE",EDGE,{"disambiguationData":[OSD([sQuery(id+"F2.wireOp",EDGE,"E14.0.2.3"),sQuery(id+"F2.wireOp",EDGE,"E14.0.2.10")])]})});
            var Q468;
            Q468=makeQuery(id+"F3.boolean.opBoolean","COPY",EDGE,{"derivedFrom":makeQuery(id+"F3.opExtrude","SWEPT_EDGE",EDGE,{"disambiguationData":[OSD([sQuery(id+"F2.wireOp",EDGE,"E14.0.4.3"),sQuery(id+"F2.wireOp",EDGE,"E14.0.4.10")])]})});
            var Q469;
            Q469=makeQuery(id+"F3.boolean.opBoolean","COPY",EDGE,{"derivedFrom":makeQuery(id+"F3.opExtrude","SWEPT_EDGE",EDGE,{"disambiguationData":[OSD([sQuery(id+"F2.wireOp",EDGE,"E23.trimOffspring"),sQuery(id+"F2.wireOp",EDGE,"E43.filletArc")])]})});
            var Q470;
            Q470=makeQuery(id+"F3.boolean.opBoolean","COPY",EDGE,{"derivedFrom":makeQuery(id+"F3.opExtrude","CAP_EDGE",EDGE,{"disambiguationData":[OSD([sQuery(id+"F2.wireOp",EDGE,"E12.filletArc"),sQuery(id+"F2.wireOp",EDGE,"E13.filletArc")])],"isStart":true})});
            var Q471;
            Q471=makeQuery(id+"F3.boolean.opBoolean","COPY",FACE,{"derivedFrom":makeQuery(id+"F3.opExtrude","SWEPT_FACE",FACE,{"disambiguationData":[OSD([sQuery(id+"F2.wireOp",EDGE,"E14.0.3.10"),sQuery(id+"F2.wireOp",EDGE,"E14.0.3.11")])]})});
            var Q472;
            Q472=makeQuery(id+"F5.opExtrude","SWEPT_EDGE",EDGE,{"disambiguationData":[OSD([sQuery(id+"F4.wireOp",EDGE,"E56.0.2.3"),sQuery(id+"F4.wireOp",EDGE,"E67")])]});
            var Q473;
            Q473=makeQuery(id+"F5.opExtrude","SWEPT_EDGE",EDGE,{"disambiguationData":[OSD([sQuery(id+"F4.wireOp",EDGE,"E56.0.3.5"),sQuery(id+"F4.wireOp",EDGE,"E56.0.3.10"),sQuery(id+"F4.wireOp",EDGE,"E76.0.1.4")])]});
            var Q474;
            Q474=makeQuery(id+"F5.opExtrude","SWEPT_EDGE",EDGE,{"disambiguationData":[OSD([sQuery(id+"F4.wireOp",EDGE,"E56.0.5.1"),sQuery(id+"F4.wireOp",EDGE,"E56.0.5.11"),sQuery(id+"F4.wireOp",EDGE,"E76.0.2.1")])]});
            var Q475;
            Q475=makeQuery(id+"F5.opExtrude","SWEPT_EDGE",EDGE,{"disambiguationData":[OSD([sQuery(id+"F4.wireOp",EDGE,"E56.0.6.3"),sQuery(id+"F4.wireOp",EDGE,"E56.0.6.11"),sQuery(id+"F4.wireOp",EDGE,"E76.0.2.0")])]});
            var Q476;
            Q476=makeQuery(id+"F5.opExtrude","SWEPT_EDGE",EDGE,{"disambiguationData":[OSD([sQuery(id+"F4.wireOp",EDGE,"E56.0.9.1"),sQuery(id+"F4.wireOp",EDGE,"E56.0.9.11"),sQuery(id+"F4.wireOp",EDGE,"E76.0.4.1")])]});
            var Q477;
            Q477=makeQuery(id+"F5.opExtrude","SWEPT_EDGE",EDGE,{"disambiguationData":[OSD([sQuery(id+"F4.wireOp",EDGE,"E56.0.10.4"),sQuery(id+"F4.wireOp",EDGE,"E56.0.10.7")])]});
            var Q478;
            Q478=makeQuery(id+"F5.opExtrude","CAP_EDGE",EDGE,{"disambiguationData":[OSD([sQuery(id+"F4.wireOp",EDGE,"E56.0.1.4")])],"isStart":false});
            var Q479;
            Q479=makeQuery(id+"F5.opExtrude","CAP_EDGE",EDGE,{"disambiguationData":[OSD([sQuery(id+"F4.wireOp",EDGE,"E56.0.3.0")])],"isStart":false});
            var Q480;
            Q480=makeQuery(id+"F5.opExtrude","CAP_EDGE",EDGE,{"disambiguationData":[OSD([sQuery(id+"F4.wireOp",EDGE,"E56.0.8.2")])],"isStart":false});
            var Q481;
            Q481=makeQuery(id+"F5.opExtrude","CAP_EDGE",EDGE,{"disambiguationData":[OSD([sQuery(id+"F4.wireOp",EDGE,"E56.0.10.7")])],"isStart":false});
            var Q482;
            Q482=makeQuery(id+"F5.opExtrude","SWEPT_EDGE",EDGE,{"disambiguationData":[OSD([sQuery(id+"F4.wireOp",EDGE,"E56.0.2.4"),sQuery(id+"F4.wireOp",EDGE,"E66.0.1.8"),sQuery(id+"F4.wireOp",EDGE,"E56.0.2.7")])]});
            var Q483;
            Q483=makeQuery(id+"F5.opExtrude","SWEPT_EDGE",EDGE,{"disambiguationData":[OSD([sQuery(id+"F4.wireOp",EDGE,"E56.0.4.0"),sQuery(id+"F4.wireOp",EDGE,"E66.0.2.2"),sQuery(id+"F4.wireOp",EDGE,"E56.0.4.7")])]});
            var Q484;
            Q484=makeQuery(id+"F5.opExtrude","SWEPT_EDGE",EDGE,{"disambiguationData":[OSD([sQuery(id+"F4.wireOp",EDGE,"E56.0.5.2"),sQuery(id+"F4.wireOp",EDGE,"E56.0.5.12"),sQuery(id+"F4.wireOp",EDGE,"E66.0.2.3")])]});
            var Q485;
            Q485=makeQuery(id+"F5.opExtrude","SWEPT_EDGE",EDGE,{"disambiguationData":[OSD([sQuery(id+"F4.wireOp",EDGE,"E56.0.6.4"),sQuery(id+"F4.wireOp",EDGE,"E66.0.3.8"),sQuery(id+"F4.wireOp",EDGE,"E56.0.6.7")])]});
            var Q486;
            Q486=makeQuery(id+"F5.opExtrude","SWEPT_EDGE",EDGE,{"disambiguationData":[OSD([sQuery(id+"F4.wireOp",EDGE,"E56.0.8.0"),sQuery(id+"F4.wireOp",EDGE,"E66.0.4.2"),sQuery(id+"F4.wireOp",EDGE,"E56.0.8.7")])]});
            var Q487;
            Q487=makeQuery(id+"F5.opExtrude","SWEPT_EDGE",EDGE,{"disambiguationData":[OSD([sQuery(id+"F4.wireOp",EDGE,"E56.0.9.2"),sQuery(id+"F4.wireOp",EDGE,"E56.0.9.12"),sQuery(id+"F4.wireOp",EDGE,"E66.0.4.3")])]});
            var Q488;
            Q488=makeQuery(id+"F5.opExtrude","SWEPT_EDGE",EDGE,{"disambiguationData":[OSD([sQuery(id+"F4.wireOp",EDGE,"E56.0.10.4"),sQuery(id+"F4.wireOp",EDGE,"E56.0.10.8"),sQuery(id+"F4.wireOp",EDGE,"E76.0.4.2")])]});
            var Q489;
            Q489=makeQuery(id+"F5.opExtrude","SWEPT_EDGE",EDGE,{"disambiguationData":[OSD([sQuery(id+"F4.wireOp",EDGE,"E56.0.5.2"),sQuery(id+"F4.wireOp",EDGE,"E56.0.5.10"),sQuery(id+"F4.wireOp",EDGE,"E76.0.2.3")])]});
            var Q490;
            Q490=makeQuery(id+"F5.opExtrude","SWEPT_EDGE",EDGE,{"disambiguationData":[OSD([sQuery(id+"F4.wireOp",EDGE,"E56.0.6.4"),sQuery(id+"F4.wireOp",EDGE,"E56.0.6.8"),sQuery(id+"F4.wireOp",EDGE,"E76.0.2.2")])]});
            var Q491;
            Q491=makeQuery(id+"F5.opExtrude","SWEPT_EDGE",EDGE,{"disambiguationData":[OSD([sQuery(id+"F4.wireOp",EDGE,"E56.0.8.0"),sQuery(id+"F4.wireOp",EDGE,"E56.0.8.8"),sQuery(id+"F4.wireOp",EDGE,"E76.0.3.1")])]});
            var Q492;
            Q492=makeQuery(id+"F5.opExtrude","CAP_EDGE",EDGE,{"disambiguationData":[OSD([sQuery(id+"F4.wireOp",EDGE,"E56.0.9.5")])],"isStart":false});
            var Q493;
            Q493=makeQuery(id+"F5.opExtrude","CAP_EDGE",EDGE,{"disambiguationData":[OSD([sQuery(id+"F4.wireOp",EDGE,"E56.0.10.13")])],"isStart":false});
            var Q494;
            Q494=makeQuery(id+"F5.opExtrude","SWEPT_EDGE",EDGE,{"disambiguationData":[OSD([sQuery(id+"F4.wireOp",EDGE,"E56.0.5.3"),sQuery(id+"F4.wireOp",EDGE,"E66.0.2.8"),sQuery(id+"F4.wireOp",EDGE,"E56.0.5.13")])]});
            var Q495;
            Q495=makeQuery(id+"F5.opExtrude","SWEPT_EDGE",EDGE,{"disambiguationData":[OSD([sQuery(id+"F4.wireOp",EDGE,"E56.0.6.5"),sQuery(id+"F4.wireOp",EDGE,"E66.0.3.3"),sQuery(id+"F4.wireOp",EDGE,"E56.0.6.12")])]});
            var Q496;
            Q496=makeQuery(id+"F5.opExtrude","SWEPT_EDGE",EDGE,{"disambiguationData":[OSD([sQuery(id+"F4.wireOp",EDGE,"E56.0.8.1"),sQuery(id+"F4.wireOp",EDGE,"E66.0.4.9"),sQuery(id+"F4.wireOp",EDGE,"E56.0.8.13")])]});
            var Q497;
            Q497=makeQuery(id+"F5.opExtrude","SWEPT_EDGE",EDGE,{"disambiguationData":[OSD([sQuery(id+"F4.wireOp",EDGE,"E56.0.9.3"),sQuery(id+"F4.wireOp",EDGE,"E66.0.4.8"),sQuery(id+"F4.wireOp",EDGE,"E56.0.9.13")])]});
            var Q498;
            Q498=makeQuery(id+"F5.opExtrude","SWEPT_EDGE",EDGE,{"disambiguationData":[OSD([sQuery(id+"F4.wireOp",EDGE,"E74.bottom"),sQuery(id+"F4.wireOp",EDGE,"E74.right")])]});
            var Q499;
            Q499=makeQuery(id+"F5.opExtrude","SWEPT_EDGE",EDGE,{"disambiguationData":[OSD([sQuery(id+"F4.wireOp",EDGE,"E56.0.2.5"),sQuery(id+"F4.wireOp",EDGE,"E69")])]});
            var Q500;
            Q500=makeQuery(id+"F5.opExtrude","SWEPT_EDGE",EDGE,{"disambiguationData":[OSD([sQuery(id+"F4.wireOp",EDGE,"E56.0.4.1"),sQuery(id+"F4.wireOp",EDGE,"E56.0.4.11"),sQuery(id+"F4.wireOp",EDGE,"E76.0.1.5")])]});
            var Q501;
            Q501=makeQuery(id+"F5.opExtrude","SWEPT_EDGE",EDGE,{"disambiguationData":[OSD([sQuery(id+"F4.wireOp",EDGE,"E56.0.5.3"),sQuery(id+"F4.wireOp",EDGE,"E56.0.5.11"),sQuery(id+"F4.wireOp",EDGE,"E76.0.2.2")])]});
            var Q502;
            Q502=makeQuery(id+"F5.opExtrude","SWEPT_EDGE",EDGE,{"disambiguationData":[OSD([sQuery(id+"F4.wireOp",EDGE,"E56.0.6.5"),sQuery(id+"F4.wireOp",EDGE,"E56.0.6.10"),sQuery(id+"F4.wireOp",EDGE,"E76.0.2.3")])]});
            var Q503;
            Q503=makeQuery(id+"F5.opExtrude","SWEPT_EDGE",EDGE,{"disambiguationData":[OSD([sQuery(id+"F4.wireOp",EDGE,"E56.0.8.1"),sQuery(id+"F4.wireOp",EDGE,"E56.0.8.11"),sQuery(id+"F4.wireOp",EDGE,"E76.0.3.5")])]});
            var Q504;
            Q504=makeQuery(id+"F5.opExtrude","SWEPT_EDGE",EDGE,{"disambiguationData":[OSD([sQuery(id+"F4.wireOp",EDGE,"E56.0.9.3"),sQuery(id+"F4.wireOp",EDGE,"E56.0.9.11"),sQuery(id+"F4.wireOp",EDGE,"E76.0.4.2")])]});
            var Q505;
            Q505=makeQuery(id+"F5.opExtrude","SWEPT_EDGE",EDGE,{"disambiguationData":[OSD([sQuery(id+"F4.wireOp",EDGE,"E74.top"),sQuery(id+"F4.wireOp",EDGE,"E74.right")])]});
            var Q506;
            Q506=makeQuery(id+"F5.opExtrude","CAP_EDGE",EDGE,{"disambiguationData":[OSD([sQuery(id+"F4.wireOp",EDGE,"E55.0.2.1")])],"isStart":false});
            var Q507;
            Q507=makeQuery(id+"F5.opExtrude","CAP_EDGE",EDGE,{"disambiguationData":[OSD([sQuery(id+"F4.wireOp",EDGE,"E56.0.2.0")])],"isStart":false});
            var Q508;
            Q508=makeQuery(id+"F5.opExtrude","CAP_EDGE",EDGE,{"disambiguationData":[OSD([sQuery(id+"F4.wireOp",EDGE,"E56.0.4.4")])],"isStart":false});
            var Q509;
            Q509=makeQuery(id+"F5.opExtrude","CAP_EDGE",EDGE,{"disambiguationData":[OSD([sQuery(id+"F4.wireOp",EDGE,"E56.0.7.2")])],"isStart":false});
            var Q510;
            Q510=makeQuery(id+"F5.opExtrude","SWEPT_EDGE",EDGE,{"disambiguationData":[OSD([sQuery(id+"F4.wireOp",EDGE,"E56.0.4.2"),sQuery(id+"F4.wireOp",EDGE,"E66.0.2.5"),sQuery(id+"F4.wireOp",EDGE,"E56.0.4.12")])]});
            var Q511;
            Q511=makeQuery(id+"F5.opExtrude","SWEPT_EDGE",EDGE,{"disambiguationData":[OSD([sQuery(id+"F4.wireOp",EDGE,"E56.0.5.4"),sQuery(id+"F4.wireOp",EDGE,"E56.0.5.7"),sQuery(id+"F4.wireOp",EDGE,"E66.0.2.0")])]});
            var Q512;
            Q512=makeQuery(id+"F5.opExtrude","SWEPT_EDGE",EDGE,{"disambiguationData":[OSD([sQuery(id+"F4.wireOp",EDGE,"E56.0.7.0"),sQuery(id+"F4.wireOp",EDGE,"E56.0.7.7"),sQuery(id+"F4.wireOp",EDGE,"E66.0.3.9")])]});
            var Q513;
            Q513=makeQuery(id+"F5.opExtrude","SWEPT_EDGE",EDGE,{"disambiguationData":[OSD([sQuery(id+"F4.wireOp",EDGE,"E56.0.9.4"),sQuery(id+"F4.wireOp",EDGE,"E56.0.9.7"),sQuery(id+"F4.wireOp",EDGE,"E66.0.4.0")])]});
            var Q514;
            Q514=makeQuery(id+"F5.opExtrude","SWEPT_EDGE",EDGE,{"disambiguationData":[OSD([sQuery(id+"F4.wireOp",EDGE,"E56.0.4.2"),sQuery(id+"F4.wireOp",EDGE,"E56.0.4.10"),sQuery(id+"F4.wireOp",EDGE,"E76.0.1.4")])]});
            var Q515;
            Q515=makeQuery(id+"F5.opExtrude","SWEPT_EDGE",EDGE,{"disambiguationData":[OSD([sQuery(id+"F4.wireOp",EDGE,"E56.0.5.4"),sQuery(id+"F4.wireOp",EDGE,"E56.0.5.8"),sQuery(id+"F4.wireOp",EDGE,"E76.0.2.0")])]});
            var Q516;
            Q516=makeQuery(id+"F5.opExtrude","SWEPT_EDGE",EDGE,{"disambiguationData":[OSD([sQuery(id+"F4.wireOp",EDGE,"E56.0.7.0"),sQuery(id+"F4.wireOp",EDGE,"E56.0.7.8"),sQuery(id+"F4.wireOp",EDGE,"E76.0.3.5")])]});
            var Q517;
            Q517=makeQuery(id+"F5.opExtrude","SWEPT_EDGE",EDGE,{"disambiguationData":[OSD([sQuery(id+"F4.wireOp",EDGE,"E56.0.9.4"),sQuery(id+"F4.wireOp",EDGE,"E56.0.9.8"),sQuery(id+"F4.wireOp",EDGE,"E76.0.4.0")])]});
            var Q518;
            Q518=makeQuery(id+"F5.opExtrude","SWEPT_EDGE",EDGE,{"disambiguationData":[OSD([sQuery(id+"F4.wireOp",EDGE,"E56.0.1.5"),sQuery(id+"F4.wireOp",EDGE,"E61")])]});
            var Q519;
            Q519=makeQuery(id+"F5.opExtrude","SWEPT_EDGE",EDGE,{"disambiguationData":[OSD([sQuery(id+"F4.wireOp",EDGE,"E56.0.3.1"),sQuery(id+"F4.wireOp",EDGE,"E66.0.1.2"),sQuery(id+"F4.wireOp",EDGE,"E56.0.3.13")])]});
            var Q520;
            Q520=makeQuery(id+"F5.opExtrude","SWEPT_EDGE",EDGE,{"disambiguationData":[OSD([sQuery(id+"F4.wireOp",EDGE,"E56.0.4.3"),sQuery(id+"F4.wireOp",EDGE,"E66.0.2.0"),sQuery(id+"F4.wireOp",EDGE,"E56.0.4.13")])]});
            var Q521;
            Q521=makeQuery(id+"F5.opExtrude","SWEPT_EDGE",EDGE,{"disambiguationData":[OSD([sQuery(id+"F4.wireOp",EDGE,"E56.0.5.5"),sQuery(id+"F4.wireOp",EDGE,"E56.0.5.12"),sQuery(id+"F4.wireOp",EDGE,"E66.0.2.5")])]});
            var Q522;
            Q522=makeQuery(id+"F5.opExtrude","SWEPT_EDGE",EDGE,{"disambiguationData":[OSD([sQuery(id+"F4.wireOp",EDGE,"E56.0.7.1"),sQuery(id+"F4.wireOp",EDGE,"E66.0.3.2"),sQuery(id+"F4.wireOp",EDGE,"E56.0.7.13")])]});
            var Q523;
            Q523=makeQuery(id+"F5.opExtrude","SWEPT_EDGE",EDGE,{"disambiguationData":[OSD([sQuery(id+"F4.wireOp",EDGE,"E56.0.8.3"),sQuery(id+"F4.wireOp",EDGE,"E66.0.4.0"),sQuery(id+"F4.wireOp",EDGE,"E56.0.8.13")])]});
            var Q524;
            Q524=makeQuery(id+"F5.opExtrude","SWEPT_EDGE",EDGE,{"disambiguationData":[OSD([sQuery(id+"F4.wireOp",EDGE,"E56.0.1.5"),sQuery(id+"F4.wireOp",EDGE,"E70")])]});
            var Q525;
            Q525=makeQuery(id+"F5.opExtrude","SWEPT_EDGE",EDGE,{"disambiguationData":[OSD([sQuery(id+"F4.wireOp",EDGE,"E56.0.3.1"),sQuery(id+"F4.wireOp",EDGE,"E56.0.3.11"),sQuery(id+"F4.wireOp",EDGE,"E76.0.1.1")])]});
            var Q526;
            Q526=makeQuery(id+"F5.opExtrude","SWEPT_EDGE",EDGE,{"disambiguationData":[OSD([sQuery(id+"F4.wireOp",EDGE,"E56.0.4.3"),sQuery(id+"F4.wireOp",EDGE,"E56.0.4.11"),sQuery(id+"F4.wireOp",EDGE,"E76.0.1.0")])]});
            var Q527;
            Q527=makeQuery(id+"F5.opExtrude","SWEPT_EDGE",EDGE,{"disambiguationData":[OSD([sQuery(id+"F4.wireOp",EDGE,"E56.0.5.5"),sQuery(id+"F4.wireOp",EDGE,"E56.0.5.10"),sQuery(id+"F4.wireOp",EDGE,"E76.0.2.4")])]});
            var Q528;
            Q528=makeQuery(id+"F5.opExtrude","SWEPT_EDGE",EDGE,{"disambiguationData":[OSD([sQuery(id+"F4.wireOp",EDGE,"E56.0.7.1"),sQuery(id+"F4.wireOp",EDGE,"E56.0.7.11"),sQuery(id+"F4.wireOp",EDGE,"E76.0.3.1")])]});
            var Q529;
            Q529=makeQuery(id+"F5.opExtrude","SWEPT_EDGE",EDGE,{"disambiguationData":[OSD([sQuery(id+"F4.wireOp",EDGE,"E56.0.8.3"),sQuery(id+"F4.wireOp",EDGE,"E56.0.8.11"),sQuery(id+"F4.wireOp",EDGE,"E76.0.3.0")])]});
            var Q530;
            Q530=makeQuery(id+"F5.opExtrude","CAP_EDGE",EDGE,{"disambiguationData":[OSD([sQuery(id+"F4.wireOp",EDGE,"E54.bottom")])],"isStart":false});
            var Q531;
            Q531=makeQuery(id+"F5.opExtrude","SWEPT_EDGE",EDGE,{"disambiguationData":[OSD([sQuery(id+"F4.wireOp",EDGE,"E56.0.3.2"),sQuery(id+"F4.wireOp",EDGE,"E56.0.3.12"),sQuery(id+"F4.wireOp",EDGE,"E66.0.1.3")])]});
            var Q532;
            Q532=makeQuery(id+"F5.opExtrude","SWEPT_EDGE",EDGE,{"disambiguationData":[OSD([sQuery(id+"F4.wireOp",EDGE,"E56.0.6.0"),sQuery(id+"F4.wireOp",EDGE,"E66.0.3.2"),sQuery(id+"F4.wireOp",EDGE,"E56.0.6.7")])]});
            var Q533;
            Q533=makeQuery(id+"F5.opExtrude","SWEPT_EDGE",EDGE,{"disambiguationData":[OSD([sQuery(id+"F4.wireOp",EDGE,"E56.0.8.4"),sQuery(id+"F4.wireOp",EDGE,"E66.0.4.8"),sQuery(id+"F4.wireOp",EDGE,"E56.0.8.7")])]});
            var Q534;
            Q534=makeQuery(id+"F5.opExtrude","SWEPT_EDGE",EDGE,{"disambiguationData":[OSD([sQuery(id+"F4.wireOp",EDGE,"E56.0.3.2"),sQuery(id+"F4.wireOp",EDGE,"E56.0.3.10"),sQuery(id+"F4.wireOp",EDGE,"E76.0.1.3")])]});
            var Q535;
            Q535=makeQuery(id+"F5.opExtrude","SWEPT_EDGE",EDGE,{"disambiguationData":[OSD([sQuery(id+"F4.wireOp",EDGE,"E56.0.6.0"),sQuery(id+"F4.wireOp",EDGE,"E56.0.6.8"),sQuery(id+"F4.wireOp",EDGE,"E76.0.2.1")])]});
            var Q536;
            Q536=makeQuery(id+"F5.opExtrude","SWEPT_EDGE",EDGE,{"disambiguationData":[OSD([sQuery(id+"F4.wireOp",EDGE,"E56.0.8.4"),sQuery(id+"F4.wireOp",EDGE,"E56.0.8.8"),sQuery(id+"F4.wireOp",EDGE,"E76.0.3.2")])]});
            var Q537;
            Q537=makeQuery(id+"F5.opExtrude","SWEPT_EDGE",EDGE,{"disambiguationData":[OSD([sQuery(id+"F4.wireOp",EDGE,"E56.0.10.0"),sQuery(id+"F4.wireOp",EDGE,"E56.0.10.8"),sQuery(id+"F4.wireOp",EDGE,"E76.0.4.1")])]});
            var Q538;
            Q538=makeQuery(id+"F5.opExtrude","CAP_EDGE",EDGE,{"disambiguationData":[OSD([sQuery(id+"F4.wireOp",EDGE,"E56.0.1.1")])],"isStart":false});
            var Q539;
            Q539=makeQuery(id+"F5.opExtrude","SWEPT_EDGE",EDGE,{"disambiguationData":[OSD([sQuery(id+"F4.wireOp",EDGE,"E56.0.2.1"),sQuery(id+"F4.wireOp",EDGE,"E66.0.1.9"),sQuery(id+"F4.wireOp",EDGE,"E56.0.2.13")])]});
            var Q540;
            Q540=makeQuery(id+"F5.opExtrude","SWEPT_EDGE",EDGE,{"disambiguationData":[OSD([sQuery(id+"F4.wireOp",EDGE,"E56.0.3.3"),sQuery(id+"F4.wireOp",EDGE,"E66.0.1.8"),sQuery(id+"F4.wireOp",EDGE,"E56.0.3.13")])]});
            var Q541;
            Q541=makeQuery(id+"F5.opExtrude","SWEPT_EDGE",EDGE,{"disambiguationData":[OSD([sQuery(id+"F4.wireOp",EDGE,"E56.0.4.5"),sQuery(id+"F4.wireOp",EDGE,"E66.0.2.3"),sQuery(id+"F4.wireOp",EDGE,"E56.0.4.12")])]});
            var Q542;
            Q542=makeQuery(id+"F5.opExtrude","SWEPT_EDGE",EDGE,{"disambiguationData":[OSD([sQuery(id+"F4.wireOp",EDGE,"E56.0.6.1"),sQuery(id+"F4.wireOp",EDGE,"E66.0.3.9"),sQuery(id+"F4.wireOp",EDGE,"E56.0.6.13")])]});
            var Q543;
            Q543=makeQuery(id+"F5.opExtrude","SWEPT_EDGE",EDGE,{"disambiguationData":[OSD([sQuery(id+"F4.wireOp",EDGE,"E56.0.7.3"),sQuery(id+"F4.wireOp",EDGE,"E66.0.3.8"),sQuery(id+"F4.wireOp",EDGE,"E56.0.7.13")])]});
            var Q544;
            Q544=makeQuery(id+"F5.opExtrude","SWEPT_EDGE",EDGE,{"disambiguationData":[OSD([sQuery(id+"F4.wireOp",EDGE,"E56.0.2.1"),sQuery(id+"F4.wireOp",EDGE,"E68")])]});
            var Q545;
            Q545=makeQuery(id+"F5.opExtrude","SWEPT_EDGE",EDGE,{"disambiguationData":[OSD([sQuery(id+"F4.wireOp",EDGE,"E56.0.3.3"),sQuery(id+"F4.wireOp",EDGE,"E56.0.3.11"),sQuery(id+"F4.wireOp",EDGE,"E76.0.1.2")])]});
            var Q546;
            Q546=makeQuery(id+"F5.opExtrude","SWEPT_EDGE",EDGE,{"disambiguationData":[OSD([sQuery(id+"F4.wireOp",EDGE,"E56.0.4.5"),sQuery(id+"F4.wireOp",EDGE,"E56.0.4.10"),sQuery(id+"F4.wireOp",EDGE,"E76.0.1.3")])]});
            var Q547;
            Q547=makeQuery(id+"F5.opExtrude","SWEPT_EDGE",EDGE,{"disambiguationData":[OSD([sQuery(id+"F4.wireOp",EDGE,"E56.0.6.1"),sQuery(id+"F4.wireOp",EDGE,"E56.0.6.11"),sQuery(id+"F4.wireOp",EDGE,"E76.0.2.5")])]});
            var Q548;
            Q548=makeQuery(id+"F5.opExtrude","SWEPT_EDGE",EDGE,{"disambiguationData":[OSD([sQuery(id+"F4.wireOp",EDGE,"E56.0.7.3"),sQuery(id+"F4.wireOp",EDGE,"E56.0.7.11"),sQuery(id+"F4.wireOp",EDGE,"E76.0.3.2")])]});
            var Q549;
            Q549=makeQuery(id+"F5.opExtrude","SWEPT_EDGE",EDGE,{"disambiguationData":[OSD([sQuery(id+"F4.wireOp",EDGE,"E56.0.10.1"),sQuery(id+"F4.wireOp",EDGE,"E56.0.10.11"),sQuery(id+"F4.wireOp",EDGE,"E76.0.4.5")])]});
            var Q550;
            Q550=makeQuery(id+"F5.opExtrude","SWEPT_FACE",FACE,{"disambiguationData":[OSD([sQuery(id+"F4.wireOp",EDGE,"E56.0.10.5"),sQuery(id+"F4.wireOp",EDGE,"E75.top")])]});
            var Q551;
            Q551=makeQuery(id+"F5.opExtrude","SWEPT_EDGE",EDGE,{"disambiguationData":[OSD([sQuery(id+"F4.wireOp",EDGE,"E56.0.5.0"),sQuery(id+"F4.wireOp",EDGE,"E56.0.5.7"),sQuery(id+"F4.wireOp",EDGE,"E66.0.2.9")])]});
            var Q552;
            Q552=makeQuery(id+"F5.opExtrude","SWEPT_EDGE",EDGE,{"disambiguationData":[OSD([sQuery(id+"F4.wireOp",EDGE,"E56.0.6.2"),sQuery(id+"F4.wireOp",EDGE,"E66.0.3.5"),sQuery(id+"F4.wireOp",EDGE,"E56.0.6.12")])]});
            var Q553;
            Q553=makeQuery(id+"F5.opExtrude","SWEPT_EDGE",EDGE,{"disambiguationData":[OSD([sQuery(id+"F4.wireOp",EDGE,"E56.0.7.4"),sQuery(id+"F4.wireOp",EDGE,"E56.0.7.7"),sQuery(id+"F4.wireOp",EDGE,"E66.0.3.0")])]});
            var Q554;
            Q554=makeQuery(id+"F5.opExtrude","SWEPT_EDGE",EDGE,{"disambiguationData":[OSD([sQuery(id+"F4.wireOp",EDGE,"E56.0.9.0"),sQuery(id+"F4.wireOp",EDGE,"E56.0.9.7"),sQuery(id+"F4.wireOp",EDGE,"E66.0.4.9")])]});
            var Q555;
            Q555=makeQuery(id+"F5.opExtrude","SWEPT_FACE",FACE,{"disambiguationData":[OSD([sQuery(id+"F4.wireOp",EDGE,"E56.0.3.0")])]});
            var Q556;
            Q556=makeQuery(id+"F5.opExtrude","SWEPT_FACE",FACE,{"disambiguationData":[OSD([sQuery(id+"F4.wireOp",EDGE,"E67")])]});
            var Q557;
            Q557=makeQuery(id+"F5.opExtrude","SWEPT_EDGE",EDGE,{"disambiguationData":[OSD([sQuery(id+"F4.wireOp",EDGE,"E56.0.2.2"),sQuery(id+"F4.wireOp",EDGE,"E70")])]});
            var Q558;
            Q558=makeQuery(id+"F5.opExtrude","SWEPT_EDGE",EDGE,{"disambiguationData":[OSD([sQuery(id+"F4.wireOp",EDGE,"E56.0.5.0"),sQuery(id+"F4.wireOp",EDGE,"E56.0.5.8"),sQuery(id+"F4.wireOp",EDGE,"E76.0.2.5")])]});
            var Q559;
            Q559=makeQuery(id+"F5.opExtrude","SWEPT_EDGE",EDGE,{"disambiguationData":[OSD([sQuery(id+"F4.wireOp",EDGE,"E56.0.6.2"),sQuery(id+"F4.wireOp",EDGE,"E56.0.6.10"),sQuery(id+"F4.wireOp",EDGE,"E76.0.2.4")])]});
            var Q560;
            Q560=makeQuery(id+"F5.opExtrude","SWEPT_EDGE",EDGE,{"disambiguationData":[OSD([sQuery(id+"F4.wireOp",EDGE,"E56.0.7.4"),sQuery(id+"F4.wireOp",EDGE,"E56.0.7.8"),sQuery(id+"F4.wireOp",EDGE,"E76.0.3.0")])]});
            var Q561;
            Q561=makeQuery(id+"F5.opExtrude","SWEPT_EDGE",EDGE,{"disambiguationData":[OSD([sQuery(id+"F4.wireOp",EDGE,"E56.0.9.0"),sQuery(id+"F4.wireOp",EDGE,"E56.0.9.8"),sQuery(id+"F4.wireOp",EDGE,"E76.0.4.5")])]});
            var Q562;
            Q562=makeQuery(id+"F5.opExtrude","CAP_EDGE",EDGE,{"disambiguationData":[OSD([sQuery(id+"F4.wireOp",EDGE,"E75.right")])],"isStart":false});
            var Q563;
            Q563=makeQuery(id+"F5.opExtrude","SWEPT_EDGE",EDGE,{"disambiguationData":[OSD([sQuery(id+"F4.wireOp",EDGE,"E56.0.2.3"),sQuery(id+"F4.wireOp",EDGE,"E66.0.1.0"),sQuery(id+"F4.wireOp",EDGE,"E56.0.2.13")])]});
            var Q564;
            Q564=makeQuery(id+"F5.opExtrude","SWEPT_EDGE",EDGE,{"disambiguationData":[OSD([sQuery(id+"F4.wireOp",EDGE,"E56.0.3.5"),sQuery(id+"F4.wireOp",EDGE,"E56.0.3.12"),sQuery(id+"F4.wireOp",EDGE,"E66.0.1.5")])]});
            var Q565;
            Q565=makeQuery(id+"F5.opExtrude","SWEPT_EDGE",EDGE,{"disambiguationData":[OSD([sQuery(id+"F4.wireOp",EDGE,"E56.0.5.1"),sQuery(id+"F4.wireOp",EDGE,"E66.0.2.2"),sQuery(id+"F4.wireOp",EDGE,"E56.0.5.13")])]});
            var Q566;
            Q566=makeQuery(id+"F5.opExtrude","SWEPT_EDGE",EDGE,{"disambiguationData":[OSD([sQuery(id+"F4.wireOp",EDGE,"E56.0.6.3"),sQuery(id+"F4.wireOp",EDGE,"E66.0.3.0"),sQuery(id+"F4.wireOp",EDGE,"E56.0.6.13")])]});
            var Q567;
            Q567=makeQuery(id+"F5.opExtrude","SWEPT_EDGE",EDGE,{"disambiguationData":[OSD([sQuery(id+"F4.wireOp",EDGE,"E56.0.9.1"),sQuery(id+"F4.wireOp",EDGE,"E66.0.4.2"),sQuery(id+"F4.wireOp",EDGE,"E56.0.9.13")])]});
            var Q568;
            Q568=makeQuery(id+"F5.opExtrude","SWEPT_EDGE",EDGE,{"disambiguationData":[OSD([sQuery(id+"F4.wireOp",EDGE,"E56.0.10.3"),sQuery(id+"F4.wireOp",EDGE,"E56.0.10.11"),sQuery(id+"F4.wireOp",EDGE,"E76.0.4.0")])]});
            var Q569;
            Q569=makeQuery(id+"F5.opExtrude","CAP_EDGE",EDGE,{"disambiguationData":[OSD([sQuery(id+"F4.wireOp",EDGE,"E56.0.4.3")])],"isStart":true});
            var Q570;
            Q570=makeQuery(id+"F5.opExtrude","CAP_EDGE",EDGE,{"disambiguationData":[OSD([sQuery(id+"F4.wireOp",EDGE,"E56.0.7.1")])],"isStart":true});
            var Q571;
            Q571=makeQuery(id+"F5.opExtrude","CAP_EDGE",EDGE,{"disambiguationData":[OSD([sQuery(id+"F4.wireOp",EDGE,"E66.0.1.2")])],"isStart":true});
            var Q572;
            Q572=makeQuery(id+"F5.opExtrude","CAP_EDGE",EDGE,{"disambiguationData":[OSD([sQuery(id+"F4.wireOp",EDGE,"E56.0.10.0")])],"isStart":true});
            var Q573;
            Q573=makeQuery(id+"F5.opExtrude","CAP_EDGE",EDGE,{"disambiguationData":[OSD([sQuery(id+"F4.wireOp",EDGE,"E76.0.4.0")])],"isStart":true});
            var Q574;
            Q574=makeQuery(id+"F5.opExtrude","CAP_EDGE",EDGE,{"disambiguationData":[OSD([sQuery(id+"F4.wireOp",EDGE,"E56.0.4.5")])],"isStart":true});
            var Q575;
            Q575=makeQuery(id+"F5.opExtrude","CAP_EDGE",EDGE,{"disambiguationData":[OSD([sQuery(id+"F4.wireOp",EDGE,"E56.0.7.3")])],"isStart":true});
            var Q576;
            Q576=makeQuery(id+"F5.opExtrude","CAP_EDGE",EDGE,{"disambiguationData":[OSD([sQuery(id+"F4.wireOp",EDGE,"E56.0.10.1")])],"isStart":true});
            var Q577;
            Q577=makeQuery(id+"F5.opExtrude","CAP_EDGE",EDGE,{"disambiguationData":[OSD([sQuery(id+"F4.wireOp",EDGE,"E66.0.1.5")])],"isStart":true});
            var Q578;
            Q578=makeQuery(id+"F5.opExtrude","CAP_EDGE",EDGE,{"disambiguationData":[OSD([sQuery(id+"F4.wireOp",EDGE,"E56.0.2.2")])],"isStart":true});
            var Q579;
            Q579=makeQuery(id+"F5.opExtrude","CAP_EDGE",EDGE,{"disambiguationData":[OSD([sQuery(id+"F4.wireOp",EDGE,"E56.0.5.0")])],"isStart":true});
            var Q580;
            Q580=makeQuery(id+"F5.opExtrude","CAP_EDGE",EDGE,{"disambiguationData":[OSD([sQuery(id+"F4.wireOp",EDGE,"E56.0.7.4")])],"isStart":true});
            var Q581;
            Q581=makeQuery(id+"F5.opExtrude","CAP_EDGE",EDGE,{"disambiguationData":[OSD([sQuery(id+"F4.wireOp",EDGE,"E66.0.1.8")])],"isStart":true});
            var Q582;
            Q582=makeQuery(id+"F5.opExtrude","CAP_EDGE",EDGE,{"disambiguationData":[OSD([sQuery(id+"F4.wireOp",EDGE,"E56.0.2.3")])],"isStart":true});
            var Q583;
            Q583=makeQuery(id+"F5.opExtrude","CAP_EDGE",EDGE,{"disambiguationData":[OSD([sQuery(id+"F4.wireOp",EDGE,"E56.0.5.1")])],"isStart":true});
            var Q584;
            Q584=makeQuery(id+"F5.opExtrude","CAP_EDGE",EDGE,{"disambiguationData":[OSD([sQuery(id+"F4.wireOp",EDGE,"E56.0.10.3")])],"isStart":true});
            var Q585;
            Q585=makeQuery(id+"F5.opExtrude","CAP_EDGE",EDGE,{"disambiguationData":[OSD([sQuery(id+"F4.wireOp",EDGE,"E66.0.1.9")])],"isStart":true});
            var Q586;
            Q586=makeQuery(id+"F5.opExtrude","CAP_EDGE",EDGE,{"disambiguationData":[OSD([sQuery(id+"F4.wireOp",EDGE,"E66.0.4.5")])],"isStart":true});
            var Q587;
            Q587=makeQuery(id+"F5.opExtrude","CAP_EDGE",EDGE,{"disambiguationData":[OSD([sQuery(id+"F4.wireOp",EDGE,"E76.0.4.3")])],"isStart":true});
            var Q588;
            Q588=makeQuery(id+"F5.opExtrude","CAP_EDGE",EDGE,{"disambiguationData":[OSD([sQuery(id+"F4.wireOp",EDGE,"E56.0.5.2")])],"isStart":true});
            var Q589;
            Q589=makeQuery(id+"F5.opExtrude","CAP_EDGE",EDGE,{"disambiguationData":[OSD([sQuery(id+"F4.wireOp",EDGE,"E56.0.8.0")])],"isStart":true});
            var Q590;
            Q590=makeQuery(id+"F5.opExtrude","CAP_EDGE",EDGE,{"disambiguationData":[OSD([sQuery(id+"F4.wireOp",EDGE,"E56.0.10.4")])],"isStart":true});
            var Q591;
            Q591=makeQuery(id+"F5.opExtrude","CAP_EDGE",EDGE,{"disambiguationData":[OSD([sQuery(id+"F4.wireOp",EDGE,"E66.0.4.8")])],"isStart":true});
            var Q592;
            Q592=makeQuery(id+"F5.opExtrude","CAP_EDGE",EDGE,{"disambiguationData":[OSD([sQuery(id+"F4.wireOp",EDGE,"E76.0.2.0")])],"isStart":true});
            var Q593;
            Q593=makeQuery(id+"F5.opExtrude","CAP_EDGE",EDGE,{"disambiguationData":[OSD([sQuery(id+"F4.wireOp",EDGE,"E56.0.2.5")])],"isStart":true});
            var Q594;
            Q594=makeQuery(id+"F5.opExtrude","CAP_EDGE",EDGE,{"disambiguationData":[OSD([sQuery(id+"F4.wireOp",EDGE,"E56.0.5.3")])],"isStart":true});
            var Q595;
            Q595=makeQuery(id+"F5.opExtrude","CAP_EDGE",EDGE,{"disambiguationData":[OSD([sQuery(id+"F4.wireOp",EDGE,"E56.0.8.1")])],"isStart":true});
            var Q596;
            Q596=makeQuery(id+"F5.opExtrude","CAP_EDGE",EDGE,{"disambiguationData":[OSD([sQuery(id+"F4.wireOp",EDGE,"E76.0.2.1")])],"isStart":true});
            var Q597;
            Q597=makeQuery(id+"F5.opExtrude","CAP_EDGE",EDGE,{"disambiguationData":[OSD([sQuery(id+"F4.wireOp",EDGE,"E56.0.5.4")])],"isStart":true});
            var Q598;
            Q598=makeQuery(id+"F5.opExtrude","CAP_EDGE",EDGE,{"disambiguationData":[OSD([sQuery(id+"F4.wireOp",EDGE,"E56.0.3.1")])],"isStart":true});
            var Q599;
            Q599=makeQuery(id+"F5.opExtrude","CAP_EDGE",EDGE,{"disambiguationData":[OSD([sQuery(id+"F4.wireOp",EDGE,"E56.0.5.5")])],"isStart":true});
            var Q600;
            Q600=makeQuery(id+"F5.opExtrude","CAP_EDGE",EDGE,{"disambiguationData":[OSD([sQuery(id+"F4.wireOp",EDGE,"E56.0.8.3")])],"isStart":true});
            var Q601;
            Q601=makeQuery(id+"F5.opExtrude","CAP_EDGE",EDGE,{"disambiguationData":[OSD([sQuery(id+"F4.wireOp",EDGE,"E66.0.2.5")])],"isStart":true});
            var Q602;
            Q602=makeQuery(id+"F5.opExtrude","CAP_EDGE",EDGE,{"disambiguationData":[OSD([sQuery(id+"F4.wireOp",EDGE,"E56.0.3.2")])],"isStart":true});
            var Q603;
            Q603=makeQuery(id+"F5.opExtrude","CAP_EDGE",EDGE,{"disambiguationData":[OSD([sQuery(id+"F4.wireOp",EDGE,"E56.0.6.0")])],"isStart":true});
            var Q604;
            Q604=makeQuery(id+"F5.opExtrude","CAP_EDGE",EDGE,{"disambiguationData":[OSD([sQuery(id+"F4.wireOp",EDGE,"E56.0.8.4")])],"isStart":true});
            var Q605;
            Q605=makeQuery(id+"F5.opExtrude","CAP_EDGE",EDGE,{"disambiguationData":[OSD([sQuery(id+"F4.wireOp",EDGE,"E58")])],"isStart":true});
            var Q606;
            Q606=makeQuery(id+"F5.opExtrude","CAP_EDGE",EDGE,{"disambiguationData":[OSD([sQuery(id+"F4.wireOp",EDGE,"E66.0.2.8")])],"isStart":true});
            var Q607;
            Q607=makeQuery(id+"F5.opExtrude","CAP_EDGE",EDGE,{"disambiguationData":[OSD([sQuery(id+"F4.wireOp",EDGE,"E56.0.3.3")])],"isStart":true});
            var Q608;
            Q608=makeQuery(id+"F5.opExtrude","CAP_EDGE",EDGE,{"disambiguationData":[OSD([sQuery(id+"F4.wireOp",EDGE,"E56.0.6.1")])],"isStart":true});
            var Q609;
            Q609=makeQuery(id+"F5.opExtrude","CAP_EDGE",EDGE,{"disambiguationData":[OSD([sQuery(id+"F4.wireOp",EDGE,"E59")])],"isStart":true});
            var Q610;
            Q610=makeQuery(id+"F5.opExtrude","CAP_EDGE",EDGE,{"disambiguationData":[OSD([sQuery(id+"F4.wireOp",EDGE,"E56.0.6.2")])],"isStart":true});
            var Q611;
            Q611=makeQuery(id+"F5.opExtrude","CAP_EDGE",EDGE,{"disambiguationData":[OSD([sQuery(id+"F4.wireOp",EDGE,"E56.0.9.0")])],"isStart":true});
            var Q612;
            Q612=makeQuery(id+"F5.opExtrude","CAP_EDGE",EDGE,{"disambiguationData":[OSD([sQuery(id+"F4.wireOp",EDGE,"E61")])],"isStart":true});
            var Q613;
            Q613=makeQuery(id+"F5.opExtrude","CAP_EDGE",EDGE,{"disambiguationData":[OSD([sQuery(id+"F4.wireOp",EDGE,"E76.0.3.0")])],"isStart":true});
            var Q614;
            Q614=makeQuery(id+"F5.opExtrude","CAP_EDGE",EDGE,{"disambiguationData":[OSD([sQuery(id+"F4.wireOp",EDGE,"E56.0.3.5")])],"isStart":true});
            var Q615;
            Q615=makeQuery(id+"F5.opExtrude","CAP_EDGE",EDGE,{"disambiguationData":[OSD([sQuery(id+"F4.wireOp",EDGE,"E56.0.6.3")])],"isStart":true});
            var Q616;
            Q616=makeQuery(id+"F5.opExtrude","CAP_EDGE",EDGE,{"disambiguationData":[OSD([sQuery(id+"F4.wireOp",EDGE,"E56.0.9.1")])],"isStart":true});
            var Q617;
            Q617=makeQuery(id+"F5.opExtrude","CAP_EDGE",EDGE,{"disambiguationData":[OSD([sQuery(id+"F4.wireOp",EDGE,"E56.0.6.4")])],"isStart":true});
            var Q618;
            Q618=makeQuery(id+"F5.opExtrude","CAP_EDGE",EDGE,{"disambiguationData":[OSD([sQuery(id+"F4.wireOp",EDGE,"E56.0.4.1")])],"isStart":true});
            var Q619;
            Q619=makeQuery(id+"F5.opExtrude","CAP_EDGE",EDGE,{"disambiguationData":[OSD([sQuery(id+"F4.wireOp",EDGE,"E56.0.6.5")])],"isStart":true});
            var Q620;
            Q620=makeQuery(id+"F5.opExtrude","CAP_EDGE",EDGE,{"disambiguationData":[OSD([sQuery(id+"F4.wireOp",EDGE,"E56.0.9.3")])],"isStart":true});
            var Q621;
            Q621=makeQuery(id+"F5.opExtrude","CAP_EDGE",EDGE,{"disambiguationData":[OSD([sQuery(id+"F4.wireOp",EDGE,"E66.0.3.5")])],"isStart":true});
            var Q622;
            Q622=makeQuery(id+"F5.opExtrude","CAP_EDGE",EDGE,{"disambiguationData":[OSD([sQuery(id+"F4.wireOp",EDGE,"E56.0.4.2")])],"isStart":true});
            var Q623;
            Q623=makeQuery(id+"F5.opExtrude","CAP_EDGE",EDGE,{"disambiguationData":[OSD([sQuery(id+"F4.wireOp",EDGE,"E56.0.7.0")])],"isStart":true});
            var Q624;
            Q624=makeQuery(id+"F5.opExtrude","CAP_EDGE",EDGE,{"disambiguationData":[OSD([sQuery(id+"F4.wireOp",EDGE,"E56.0.9.4")])],"isStart":true});
            var Q625;
            Q625=makeQuery(id+"F5.opExtrude","CAP_EDGE",EDGE,{"disambiguationData":[OSD([sQuery(id+"F4.wireOp",EDGE,"E66.0.3.8")])],"isStart":true});
            var Q626;
            Q626=makeQuery(id+"F5.opExtrude","CAP_EDGE",EDGE,{"disambiguationData":[OSD([sQuery(id+"F4.wireOp",EDGE,"E76.0.1.0")])],"isStart":true});
            var Q627;
            Q627=makeQuery(id+"F3.boolean.opBoolean","COPY",FACE,{"derivedFrom":makeQuery(id+"F3.opExtrude","SWEPT_FACE",FACE,{"disambiguationData":[OSD([sQuery(id+"F2.wireOp",EDGE,"E12.filletArc"),sQuery(id+"F2.wireOp",EDGE,"E13.filletArc")])]})});
            var Q628;
            Q628=makeQuery(id+"F5.opExtrude","SWEPT_EDGE",EDGE,{"disambiguationData":[OSD([sQuery(id+"F4.wireOp",EDGE,"E55.0.2.1"),sQuery(id+"F4.wireOp",EDGE,"E55.0.2.3"),sQuery(id+"F4.wireOp",EDGE,"E59")])]});
            var Q629;
            Q629=makeQuery(id+"F5.opExtrude","CAP_EDGE",EDGE,{"disambiguationData":[OSD([sQuery(id+"F4.wireOp",EDGE,"E55.0.2.0")])],"isStart":true});
            var Q630;
            Q630=makeQuery(id+"F3.boolean.opBoolean","COPY",FACE,{"derivedFrom":makeQuery(id+"F3.opExtrude","SWEPT_FACE",FACE,{"disambiguationData":[OSD([sQuery(id+"F2.wireOp",EDGE,"E14.0.3.12"),sQuery(id+"F2.wireOp",EDGE,"E14.0.3.13")])]})});
            var Q631;
            Q631=makeQuery(id+"F3.boolean.opBoolean","COPY",EDGE,{"derivedFrom":makeQuery(id+"F3.opExtrude","CAP_EDGE",EDGE,{"disambiguationData":[OSD([sQuery(id+"F2.wireOp",EDGE,"E14.0.3.10"),sQuery(id+"F2.wireOp",EDGE,"E14.0.3.11")])],"isStart":false})});
            var Q632;
            Q632=makeQuery(id+"F3.boolean.opBoolean","COPY",FACE,{"derivedFrom":makeQuery(id+"F3.opExtrude","SWEPT_FACE",FACE,{"disambiguationData":[OSD([sQuery(id+"F2.wireOp",EDGE,"E14.0.1.12"),sQuery(id+"F2.wireOp",EDGE,"E14.0.1.13")])]})});
            var Q633;
            Q633=makeQuery(id+"F3.boolean.opBoolean","COPY",EDGE,{"derivedFrom":makeQuery(id+"F3.opExtrude","CAP_EDGE",EDGE,{"disambiguationData":[OSD([sQuery(id+"F2.wireOp",EDGE,"E14.0.2.10"),sQuery(id+"F2.wireOp",EDGE,"E14.0.2.11")])],"isStart":false})});
            var Q634;
            Q634=makeQuery(id+"F3.boolean.opBoolean","COPY",FACE,{"derivedFrom":makeQuery(id+"F3.opExtrude","SWEPT_FACE",FACE,{"disambiguationData":[OSD([sQuery(id+"F2.wireOp",EDGE,"E14.0.4.12"),sQuery(id+"F2.wireOp",EDGE,"E14.0.4.13")])]})});
            var Q635;
            Q635=makeQuery(id+"F3.boolean.opBoolean","COPY",EDGE,{"derivedFrom":makeQuery(id+"F3.opExtrude","CAP_EDGE",EDGE,{"disambiguationData":[OSD([sQuery(id+"F2.wireOp",EDGE,"E14.0.1.10"),sQuery(id+"F2.wireOp",EDGE,"E14.0.1.11")])],"isStart":false})});
            var Q636;
            Q636=makeQuery(id+"F3.boolean.opBoolean","COPY",FACE,{"derivedFrom":makeQuery(id+"F3.opExtrude","SWEPT_FACE",FACE,{"disambiguationData":[OSD([sQuery(id+"F2.wireOp",EDGE,"E14.0.2.12"),sQuery(id+"F2.wireOp",EDGE,"E14.0.2.13")])]})});
            var Q637;
            Q637=makeQuery(id+"F3.boolean.opBoolean","COPY",EDGE,{"derivedFrom":makeQuery(id+"F3.opExtrude","CAP_EDGE",EDGE,{"disambiguationData":[OSD([sQuery(id+"F2.wireOp",EDGE,"E10.filletArc"),sQuery(id+"F2.wireOp",EDGE,"E11.filletArc")])],"isStart":false})});
            var Q638;
            Q638=makeQuery(id+"F3.boolean.opBoolean","COPY",EDGE,{"derivedFrom":makeQuery(id+"F3.opExtrude","CAP_EDGE",EDGE,{"disambiguationData":[OSD([sQuery(id+"F2.wireOp",EDGE,"E14.0.4.10"),sQuery(id+"F2.wireOp",EDGE,"E14.0.4.11")])],"isStart":false})});
            var Q639;
            Q639=makeQuery(id+"F5.opExtrude","SWEPT_EDGE",EDGE,{"disambiguationData":[OSD([sQuery(id+"F4.wireOp",EDGE,"E56.0.1.3"),sQuery(id+"F4.wireOp",EDGE,"E56.0.1.13"),sQuery(id+"F4.wireOp",EDGE,"E58")])]});
            var Q640;
            Q640=makeQuery(id+"F5.opExtrude","SWEPT_EDGE",EDGE,{"disambiguationData":[OSD([sQuery(id+"F4.wireOp",EDGE,"E56.0.2.5"),sQuery(id+"F4.wireOp",EDGE,"E66.0.1.3"),sQuery(id+"F4.wireOp",EDGE,"E56.0.2.12")])]});
            var Q641;
            Q641=makeQuery(id+"F5.opExtrude","SWEPT_EDGE",EDGE,{"disambiguationData":[OSD([sQuery(id+"F4.wireOp",EDGE,"E56.0.1.4"),sQuery(id+"F4.wireOp",EDGE,"E64")])]});
            var Q642;
            Q642=makeQuery(id+"F5.opExtrude","SWEPT_EDGE",EDGE,{"disambiguationData":[OSD([sQuery(id+"F4.wireOp",EDGE,"E56.0.3.0"),sQuery(id+"F4.wireOp",EDGE,"E56.0.3.7"),sQuery(id+"F4.wireOp",EDGE,"E66.0.1.9")])]});
            var Q643;
            Q643=makeQuery(id+"F5.opExtrude","SWEPT_EDGE",EDGE,{"disambiguationData":[OSD([sQuery(id+"F4.wireOp",EDGE,"E56.0.8.2"),sQuery(id+"F4.wireOp",EDGE,"E66.0.4.5"),sQuery(id+"F4.wireOp",EDGE,"E56.0.8.12")])]});
            var Q644;
            Q644=makeQuery(id+"F5.opExtrude","SWEPT_EDGE",EDGE,{"disambiguationData":[OSD([sQuery(id+"F4.wireOp",EDGE,"E75.bottom"),sQuery(id+"F4.wireOp",EDGE,"E75.right")])]});
            var Q645;
            Q645=makeQuery(id+"F5.opExtrude","CAP_EDGE",EDGE,{"disambiguationData":[OSD([sQuery(id+"F4.wireOp",EDGE,"E55.0.2.2")])],"isStart":false});
            var Q646;
            Q646=makeQuery(id+"F5.opExtrude","CAP_EDGE",EDGE,{"disambiguationData":[OSD([sQuery(id+"F4.wireOp",EDGE,"E56.0.8.5")])],"isStart":false});
            var Q647;
            Q647=makeQuery(id+"F5.opExtrude","SWEPT_EDGE",EDGE,{"disambiguationData":[OSD([sQuery(id+"F4.wireOp",EDGE,"E56.0.9.5"),sQuery(id+"F4.wireOp",EDGE,"E56.0.9.12"),sQuery(id+"F4.wireOp",EDGE,"E66.0.4.5")])]});
            var Q648;
            Q648=makeQuery(id+"F5.opExtrude","CAP_EDGE",EDGE,{"disambiguationData":[OSD([sQuery(id+"F4.wireOp",EDGE,"E56.0.1.0")])],"isStart":false});
            var Q649;
            Q649=makeQuery(id+"F5.opExtrude","CAP_EDGE",EDGE,{"disambiguationData":[OSD([sQuery(id+"F4.wireOp",EDGE,"E56.0.3.4")])],"isStart":false});
            var Q650;
            Q650=makeQuery(id+"F5.opExtrude","CAP_EDGE",EDGE,{"disambiguationData":[OSD([sQuery(id+"F4.wireOp",EDGE,"E56.0.10.2"),sQuery(id+"F4.wireOp",EDGE,"E75.bottom")])],"isStart":false});
            var Q651;
            Q651=makeQuery(id+"F5.opExtrude","SWEPT_EDGE",EDGE,{"disambiguationData":[OSD([sQuery(id+"F4.wireOp",EDGE,"E56.0.2.0"),sQuery(id+"F4.wireOp",EDGE,"E66.0.1.2"),sQuery(id+"F4.wireOp",EDGE,"E56.0.2.7")])]});
            var Q652;
            Q652=makeQuery(id+"F5.opExtrude","SWEPT_EDGE",EDGE,{"disambiguationData":[OSD([sQuery(id+"F4.wireOp",EDGE,"E56.0.4.4"),sQuery(id+"F4.wireOp",EDGE,"E66.0.2.8"),sQuery(id+"F4.wireOp",EDGE,"E56.0.4.7")])]});
            var Q653;
            Q653=makeQuery(id+"F5.opExtrude","SWEPT_EDGE",EDGE,{"disambiguationData":[OSD([sQuery(id+"F4.wireOp",EDGE,"E56.0.7.2"),sQuery(id+"F4.wireOp",EDGE,"E56.0.7.12"),sQuery(id+"F4.wireOp",EDGE,"E66.0.3.3")])]});
            var Q654;
            Q654=makeQuery(id+"F5.opExtrude","SWEPT_EDGE",EDGE,{"disambiguationData":[OSD([sQuery(id+"F4.wireOp",EDGE,"E56.0.10.0"),sQuery(id+"F4.wireOp",EDGE,"E56.0.10.7")])]});
            var Q655;
            Q655=makeQuery(id+"F5.opExtrude","CAP_EDGE",EDGE,{"disambiguationData":[OSD([sQuery(id+"F4.wireOp",EDGE,"E54.top")])],"isStart":false});
            var Q656;
            Q656=makeQuery(id+"F5.opExtrude","CAP_EDGE",EDGE,{"disambiguationData":[OSD([sQuery(id+"F4.wireOp",EDGE,"E56.0.7.5")])],"isStart":false});
            var Q657;
            Q657=makeQuery(id+"F5.opExtrude","SWEPT_EDGE",EDGE,{"disambiguationData":[OSD([sQuery(id+"F4.wireOp",EDGE,"E56.0.10.1"),sQuery(id+"F4.wireOp",EDGE,"E56.0.10.13")])]});
            var Q658;
            Q658=makeQuery(id+"F5.opExtrude","CAP_EDGE",EDGE,{"disambiguationData":[OSD([sQuery(id+"F4.wireOp",EDGE,"E56.0.2.4")])],"isStart":false});
            var Q659;
            Q659=makeQuery(id+"F5.opExtrude","CAP_EDGE",EDGE,{"disambiguationData":[OSD([sQuery(id+"F4.wireOp",EDGE,"E56.0.4.0")])],"isStart":false});
            var Q660;
            Q660=makeQuery(id+"F5.opExtrude","CAP_EDGE",EDGE,{"disambiguationData":[OSD([sQuery(id+"F4.wireOp",EDGE,"E56.0.9.2")])],"isStart":false});
            var Q661;
            Q661=makeQuery(id+"F5.opExtrude","CAP_EDGE",EDGE,{"disambiguationData":[OSD([sQuery(id+"F4.wireOp",EDGE,"E74.right")])],"isStart":false});
            var Q662;
            Q662=makeQuery(id+"F5.opExtrude","SWEPT_EDGE",EDGE,{"disambiguationData":[OSD([sQuery(id+"F4.wireOp",EDGE,"E56.0.2.2"),sQuery(id+"F4.wireOp",EDGE,"E66.0.1.5"),sQuery(id+"F4.wireOp",EDGE,"E56.0.2.12")])]});
            var Q663;
            Q663=makeQuery(id+"F5.opExtrude","SWEPT_EDGE",EDGE,{"disambiguationData":[OSD([sQuery(id+"F4.wireOp",EDGE,"E56.0.10.3"),sQuery(id+"F4.wireOp",EDGE,"E56.0.10.13")])]});
            var Q664;
            Q664=makeQuery(id+"F5.opExtrude","CAP_EDGE",EDGE,{"disambiguationData":[OSD([sQuery(id+"F4.wireOp",EDGE,"E56.0.1.3")])],"isStart":false});
            var Q665;
            Q665=makeQuery(id+"F5.opExtrude","CAP_EDGE",EDGE,{"disambiguationData":[OSD([sQuery(id+"F4.wireOp",EDGE,"E67")])],"isStart":true});
            var Q666;
            Q666=makeQuery(id+"F5.opExtrude","SWEPT_EDGE",EDGE,{"disambiguationData":[OSD([sQuery(id+"F4.wireOp",EDGE,"E56.0.1.1"),sQuery(id+"F4.wireOp",EDGE,"E71")])]});
            var Q667;
            Q667=makeQuery(id+"F5.opExtrude","SWEPT_EDGE",EDGE,{"disambiguationData":[OSD([sQuery(id+"F4.wireOp",EDGE,"E55.0.2.0"),sQuery(id+"F4.wireOp",EDGE,"E55.0.2.2")])]});
            var Q668;
            Q668=makeQuery(id+"F5.opExtrude","SWEPT_EDGE",EDGE,{"disambiguationData":[OSD([sQuery(id+"F4.wireOp",EDGE,"E56.0.1.0"),sQuery(id+"F4.wireOp",EDGE,"E68")])]});
            var Q669;
            Q669=makeQuery(id+"F5.opExtrude","CAP_EDGE",EDGE,{"disambiguationData":[OSD([sQuery(id+"F4.wireOp",EDGE,"E56.0.2.0")])],"isStart":true});
            var Q670;
            Q670=makeQuery(id+"F5.opExtrude","CAP_EDGE",EDGE,{"disambiguationData":[OSD([sQuery(id+"F4.wireOp",EDGE,"E54.bottom")])],"isStart":true});
            var Q671;
            Q671=makeQuery(id+"F5.opExtrude","CAP_EDGE",EDGE,{"disambiguationData":[OSD([sQuery(id+"F4.wireOp",EDGE,"E55.0.2.1")])],"isStart":true});
            var Q672;
            Q672=makeQuery(id+"F5.opExtrude","CAP_EDGE",EDGE,{"disambiguationData":[OSD([sQuery(id+"F4.wireOp",EDGE,"E56.0.1.0")])],"isStart":true});
            var Q673;
            Q673=makeQuery(id+"F5.opExtrude","CAP_EDGE",EDGE,{"disambiguationData":[OSD([sQuery(id+"F4.wireOp",EDGE,"E56.0.1.1")])],"isStart":true});
            var Q674;
            Q674=makeQuery(id+"F3.boolean.opBoolean","COPY",EDGE,{"derivedFrom":makeQuery(id+"F3.opExtrude","CAP_EDGE",EDGE,{"disambiguationData":[OSD([sQuery(id+"F2.wireOp",EDGE,"E12.filletArc"),sQuery(id+"F2.wireOp",EDGE,"E13.filletArc")])],"isStart":false})});
            var Q675;
            Q675=makeQuery(id+"F3.boolean.opBoolean","COPY",EDGE,{"derivedFrom":makeQuery(id+"F3.opExtrude","CAP_EDGE",EDGE,{"disambiguationData":[OSD([sQuery(id+"F2.wireOp",EDGE,"E14.0.4.12"),sQuery(id+"F2.wireOp",EDGE,"E14.0.4.13")])],"isStart":false})});
            var Q676;
            Q676=makeQuery(id+"F3.boolean.opBoolean","COPY",EDGE,{"derivedFrom":makeQuery(id+"F3.opExtrude","CAP_EDGE",EDGE,{"disambiguationData":[OSD([sQuery(id+"F2.wireOp",EDGE,"E14.0.3.12"),sQuery(id+"F2.wireOp",EDGE,"E14.0.3.13")])],"isStart":false})});
            var Q677;
            Q677=makeQuery(id+"F3.boolean.opBoolean","COPY",EDGE,{"derivedFrom":makeQuery(id+"F3.opExtrude","CAP_EDGE",EDGE,{"disambiguationData":[OSD([sQuery(id+"F2.wireOp",EDGE,"E14.0.2.12"),sQuery(id+"F2.wireOp",EDGE,"E14.0.2.13")])],"isStart":false})});
            var Q678;
            Q678=makeQuery(id+"F3.boolean.opBoolean","COPY",EDGE,{"derivedFrom":makeQuery(id+"F3.opExtrude","CAP_EDGE",EDGE,{"disambiguationData":[OSD([sQuery(id+"F2.wireOp",EDGE,"E14.0.1.12"),sQuery(id+"F2.wireOp",EDGE,"E14.0.1.13")])],"isStart":false})});
            var Q679;
            Q679=makeQuery(id+"F5.opExtrude","SWEPT_EDGE",EDGE,{"disambiguationData":[OSD([sQuery(id+"F4.wireOp",EDGE,"E56.0.7.5"),sQuery(id+"F4.wireOp",EDGE,"E56.0.7.10"),sQuery(id+"F4.wireOp",EDGE,"E76.0.3.4")])]});
            var Q680;
            Q680=makeQuery(id+"F5.opExtrude","SWEPT_EDGE",EDGE,{"disambiguationData":[OSD([sQuery(id+"F4.wireOp",EDGE,"E56.0.2.4"),sQuery(id+"F4.wireOp",EDGE,"E72")])]});
            var Q681;
            Q681=makeQuery(id+"F5.opExtrude","SWEPT_EDGE",EDGE,{"disambiguationData":[OSD([sQuery(id+"F4.wireOp",EDGE,"E56.0.4.0"),sQuery(id+"F4.wireOp",EDGE,"E56.0.4.8"),sQuery(id+"F4.wireOp",EDGE,"E76.0.1.1")])]});
            var Q682;
            Q682=makeQuery(id+"F5.opExtrude","SWEPT_EDGE",EDGE,{"disambiguationData":[OSD([sQuery(id+"F4.wireOp",EDGE,"E56.0.9.2"),sQuery(id+"F4.wireOp",EDGE,"E56.0.9.10"),sQuery(id+"F4.wireOp",EDGE,"E76.0.4.3")])]});
            var Q683;
            Q683=makeQuery(id+"F5.opExtrude","SWEPT_EDGE",EDGE,{"disambiguationData":[OSD([sQuery(id+"F4.wireOp",EDGE,"E56.0.3.0"),sQuery(id+"F4.wireOp",EDGE,"E56.0.3.8"),sQuery(id+"F4.wireOp",EDGE,"E76.0.1.5")])]});
            var Q684;
            Q684=makeQuery(id+"F5.opExtrude","SWEPT_EDGE",EDGE,{"disambiguationData":[OSD([sQuery(id+"F4.wireOp",EDGE,"E56.0.8.2"),sQuery(id+"F4.wireOp",EDGE,"E56.0.8.10"),sQuery(id+"F4.wireOp",EDGE,"E76.0.3.4")])]});
            var Q685;
            Q685=makeQuery(id+"F5.opExtrude","SWEPT_EDGE",EDGE,{"disambiguationData":[OSD([sQuery(id+"F4.wireOp",EDGE,"E75.top"),sQuery(id+"F4.wireOp",EDGE,"E75.right")])]});
            var Q686;
            Q686=makeQuery(id+"F5.opExtrude","SWEPT_EDGE",EDGE,{"disambiguationData":[OSD([sQuery(id+"F4.wireOp",EDGE,"E56.0.8.5"),sQuery(id+"F4.wireOp",EDGE,"E66.0.4.3"),sQuery(id+"F4.wireOp",EDGE,"E56.0.8.12")])]});
            var Q687;
            Q687=makeQuery(id+"F5.opExtrude","CAP_EDGE",EDGE,{"disambiguationData":[OSD([sQuery(id+"F4.wireOp",EDGE,"E54.right")])],"isStart":false});
            var Q688;
            Q688=makeQuery(id+"F5.opExtrude","SWEPT_EDGE",EDGE,{"disambiguationData":[OSD([sQuery(id+"F4.wireOp",EDGE,"E56.0.3.4"),sQuery(id+"F4.wireOp",EDGE,"E56.0.3.7"),sQuery(id+"F4.wireOp",EDGE,"E66.0.1.0")])]});
            var Q689;
            Q689=makeQuery(id+"F5.opExtrude","CAP_EDGE",EDGE,{"disambiguationData":[OSD([sQuery(id+"F4.wireOp",EDGE,"E56.0.10.5"),sQuery(id+"F4.wireOp",EDGE,"E75.top")])],"isStart":false});
            var Q690;
            Q690=makeQuery(id+"F5.opExtrude","SWEPT_EDGE",EDGE,{"disambiguationData":[OSD([sQuery(id+"F4.wireOp",EDGE,"E56.0.7.5"),sQuery(id+"F4.wireOp",EDGE,"E56.0.7.12"),sQuery(id+"F4.wireOp",EDGE,"E66.0.3.5")])]});
            var Q691;
            Q691=makeQuery(id+"F5.opExtrude","CAP_EDGE",EDGE,{"disambiguationData":[OSD([sQuery(id+"F4.wireOp",EDGE,"E56.0.9.5")])],"isStart":true});
            var Q692;
            Q692=makeQuery(id+"F5.opExtrude","CAP_EDGE",EDGE,{"disambiguationData":[OSD([sQuery(id+"F4.wireOp",EDGE,"E56.0.4.4")])],"isStart":true});
            var Q693;
            Q693=makeQuery(id+"F5.opExtrude","CAP_EDGE",EDGE,{"disambiguationData":[OSD([sQuery(id+"F4.wireOp",EDGE,"E56.0.7.2")])],"isStart":true});
            var Q694;
            Q694=makeQuery(id+"F5.opExtrude","CAP_EDGE",EDGE,{"disambiguationData":[OSD([sQuery(id+"F4.wireOp",EDGE,"E56.0.3.0")])],"isStart":true});
            var Q695;
            Q695=makeQuery(id+"F5.opExtrude","CAP_EDGE",EDGE,{"disambiguationData":[OSD([sQuery(id+"F4.wireOp",EDGE,"E56.0.8.2")])],"isStart":true});
            var Q696;
            Q696=makeQuery(id+"F5.opExtrude","CAP_EDGE",EDGE,{"disambiguationData":[OSD([sQuery(id+"F4.wireOp",EDGE,"E56.0.10.7")])],"isStart":true});
            var Q697;
            Q697=makeQuery(id+"F5.opExtrude","CAP_EDGE",EDGE,{"disambiguationData":[OSD([sQuery(id+"F4.wireOp",EDGE,"E56.0.10.13")])],"isStart":true});
            var Q698;
            Q698=makeQuery(id+"F5.opExtrude","CAP_EDGE",EDGE,{"disambiguationData":[OSD([sQuery(id+"F4.wireOp",EDGE,"E74.right")])],"isStart":true});
            var Q699;
            Q699=makeQuery(id+"F5.opExtrude","SWEPT_EDGE",EDGE,{"disambiguationData":[OSD([sQuery(id+"F4.wireOp",EDGE,"E54.bottom"),sQuery(id+"F4.wireOp",EDGE,"E54.right")])]});
            var Q700;
            Q700=makeQuery(id+"F5.opExtrude","SWEPT_EDGE",EDGE,{"disambiguationData":[OSD([sQuery(id+"F4.wireOp",EDGE,"E55.0.2.1"),sQuery(id+"F4.wireOp",EDGE,"E55.0.2.2")])]});
            var Q701;
            Q701=makeQuery(id+"F5.opExtrude","CAP_EDGE",EDGE,{"disambiguationData":[OSD([sQuery(id+"F4.wireOp",EDGE,"E54.top")])],"isStart":true});
            var Q702;
            Q702=makeQuery(id+"F5.opExtrude","CAP_EDGE",EDGE,{"disambiguationData":[OSD([sQuery(id+"F4.wireOp",EDGE,"E56.0.1.3")])],"isStart":true});
            var Q703;
            Q703=makeQuery(id+"F5.opExtrude","CAP_EDGE",EDGE,{"disambiguationData":[OSD([sQuery(id+"F4.wireOp",EDGE,"E56.0.1.4")])],"isStart":true});
            var Q704;
            Q704=makeQuery(id+"F5.opExtrude","SWEPT_EDGE",EDGE,{"disambiguationData":[OSD([sQuery(id+"F4.wireOp",EDGE,"E56.0.10.5"),sQuery(id+"F4.wireOp",EDGE,"E56.0.10.10"),sQuery(id+"F4.wireOp",EDGE,"E76.0.4.3")])]});
            var Q705;
            Q705=makeQuery(id+"F5.opExtrude","SWEPT_EDGE",EDGE,{"disambiguationData":[OSD([sQuery(id+"F4.wireOp",EDGE,"E56.0.1.3"),sQuery(id+"F4.wireOp",EDGE,"E72")])]});
            var Q706;
            Q706=makeQuery(id+"F5.opExtrude","SWEPT_EDGE",EDGE,{"disambiguationData":[OSD([sQuery(id+"F4.wireOp",EDGE,"E56.0.1.4"),sQuery(id+"F4.wireOp",EDGE,"E67")])]});
            var Q707;
            Q707=makeQuery(id+"F5.opExtrude","SWEPT_EDGE",EDGE,{"disambiguationData":[OSD([sQuery(id+"F4.wireOp",EDGE,"E56.0.9.5"),sQuery(id+"F4.wireOp",EDGE,"E56.0.9.10"),sQuery(id+"F4.wireOp",EDGE,"E76.0.4.4")])]});
            var Q708;
            Q708=makeQuery(id+"F5.opExtrude","SWEPT_EDGE",EDGE,{"disambiguationData":[OSD([sQuery(id+"F4.wireOp",EDGE,"E56.0.2.0"),sQuery(id+"F4.wireOp",EDGE,"E71")])]});
            var Q709;
            Q709=makeQuery(id+"F5.opExtrude","SWEPT_EDGE",EDGE,{"disambiguationData":[OSD([sQuery(id+"F4.wireOp",EDGE,"E56.0.4.4"),sQuery(id+"F4.wireOp",EDGE,"E56.0.4.8"),sQuery(id+"F4.wireOp",EDGE,"E76.0.1.2")])]});
            var Q710;
            Q710=makeQuery(id+"F5.opExtrude","SWEPT_EDGE",EDGE,{"disambiguationData":[OSD([sQuery(id+"F4.wireOp",EDGE,"E56.0.7.2"),sQuery(id+"F4.wireOp",EDGE,"E56.0.7.10"),sQuery(id+"F4.wireOp",EDGE,"E76.0.3.3")])]});
            var Q711;
            Q711=makeQuery(id+"F5.opExtrude","SWEPT_EDGE",EDGE,{"disambiguationData":[OSD([sQuery(id+"F4.wireOp",EDGE,"E56.0.8.5"),sQuery(id+"F4.wireOp",EDGE,"E56.0.8.10"),sQuery(id+"F4.wireOp",EDGE,"E76.0.3.3")])]});
            var Q712;
            Q712=makeQuery(id+"F5.opExtrude","SWEPT_EDGE",EDGE,{"disambiguationData":[OSD([sQuery(id+"F4.wireOp",EDGE,"E56.0.3.4"),sQuery(id+"F4.wireOp",EDGE,"E56.0.3.8"),sQuery(id+"F4.wireOp",EDGE,"E76.0.1.0")])]});
            var Q713;
            Q713=makeQuery(id+"F5.opExtrude","CAP_EDGE",EDGE,{"disambiguationData":[OSD([sQuery(id+"F4.wireOp",EDGE,"E56.0.10.2"),sQuery(id+"F4.wireOp",EDGE,"E75.bottom")])],"isStart":true});
            var Q714;
            Q714=makeQuery(id+"F5.opExtrude","CAP_EDGE",EDGE,{"disambiguationData":[OSD([sQuery(id+"F4.wireOp",EDGE,"E56.0.7.5")])],"isStart":true});
            var Q715;
            Q715=makeQuery(id+"F5.opExtrude","CAP_EDGE",EDGE,{"disambiguationData":[OSD([sQuery(id+"F4.wireOp",EDGE,"E56.0.2.4")])],"isStart":true});
            var Q716;
            Q716=makeQuery(id+"F5.opExtrude","CAP_EDGE",EDGE,{"disambiguationData":[OSD([sQuery(id+"F4.wireOp",EDGE,"E56.0.8.5")])],"isStart":true});
            var Q717;
            Q717=makeQuery(id+"F5.opExtrude","CAP_EDGE",EDGE,{"disambiguationData":[OSD([sQuery(id+"F4.wireOp",EDGE,"E56.0.3.4")])],"isStart":true});
            var Q718;
            Q718=makeQuery(id+"F5.opExtrude","CAP_EDGE",EDGE,{"disambiguationData":[OSD([sQuery(id+"F4.wireOp",EDGE,"E56.0.4.0")])],"isStart":true});
            var Q719;
            Q719=makeQuery(id+"F5.opExtrude","CAP_EDGE",EDGE,{"disambiguationData":[OSD([sQuery(id+"F4.wireOp",EDGE,"E56.0.9.2")])],"isStart":true});
            var Q720;
            Q720=makeQuery(id+"F5.opExtrude","CAP_EDGE",EDGE,{"disambiguationData":[OSD([sQuery(id+"F4.wireOp",EDGE,"E75.right")])],"isStart":true});
            var Q721;
            Q721=makeQuery(id+"F5.opExtrude","SWEPT_EDGE",EDGE,{"disambiguationData":[OSD([sQuery(id+"F4.wireOp",EDGE,"E54.top"),sQuery(id+"F4.wireOp",EDGE,"E54.right")])]});
            var Q722;
            Q722=makeQuery(id+"F5.opExtrude","CAP_EDGE",EDGE,{"disambiguationData":[OSD([sQuery(id+"F4.wireOp",EDGE,"E55.0.2.2")])],"isStart":true});
            var Q723;
            Q723=makeQuery(id+"F5.opExtrude","SWEPT_EDGE",EDGE,{"disambiguationData":[OSD([sQuery(id+"F4.wireOp",EDGE,"E56.0.10.2"),sQuery(id+"F4.wireOp",EDGE,"E56.0.10.10"),sQuery(id+"F4.wireOp",EDGE,"E76.0.4.4")])]});
            var Q724;
            Q724=makeQuery(id+"F5.opExtrude","CAP_EDGE",EDGE,{"disambiguationData":[OSD([sQuery(id+"F4.wireOp",EDGE,"E56.0.10.5"),sQuery(id+"F4.wireOp",EDGE,"E75.top")])],"isStart":true});
            var Q725;
            Q725=makeQuery(id+"F5.opExtrude","CAP_EDGE",EDGE,{"disambiguationData":[OSD([sQuery(id+"F4.wireOp",EDGE,"E54.right")])],"isStart":true});
            fillet(context, id + "F6", {"entities" : qUnion([Q0, Q1, Q2, Q3, Q4, Q5, Q6, Q7, Q8, Q9, Q10, Q11, Q12, Q13, Q14, Q15, Q16, Q17, Q18, Q19, Q20, Q21, Q22, Q23, Q24, Q25, Q26, Q27, Q28, Q29, Q30, Q31, Q32, Q33, Q34, Q35, Q36, Q37, Q38, Q39, Q40, Q41, Q42, Q43, Q44, Q45, Q46, Q47, Q48, Q49, Q50, Q51, Q52, Q53, Q54, Q55, Q56, Q57, Q58, Q59, Q60, Q61, Q62, Q63, Q64, Q65, Q66, Q67, Q68, Q69, Q70, Q71, Q72, Q73, Q74, Q75, Q76, Q77, Q78, Q79, Q80, Q81, Q82, Q83, Q84, Q85, Q86, Q87, Q88, Q89, Q90, Q91, Q92, Q93, Q94, Q95, Q96, Q97, Q98, Q99, Q100, Q101, Q102, Q103, Q104, Q105, Q106, Q107, Q108, Q109, Q110, Q111, Q112, Q113, Q114, Q115, Q116, Q117, Q118, Q119, Q120, Q121, Q122, Q123, Q124, Q125, Q126, Q127, Q128, Q129, Q130, Q131, Q132, Q133, Q134, Q135, Q136, Q137, Q138, Q139, Q140, Q141, Q142, Q143, Q144, Q145, Q146, Q147, Q148, Q149, Q150, Q151, Q152, Q153, Q154, Q155, Q156, Q157, Q158, Q159, Q160, Q161, Q162, Q163, Q164, Q165, Q166, Q167, Q168, Q169, Q170, Q171, Q172, Q173, Q174, Q175, Q176, Q177, Q178, Q179, Q180, Q181, Q182, Q183, Q184, Q185, Q186, Q187, Q188, Q189, Q190, Q191, Q192, Q193, Q194, Q195, Q196, Q197, Q198, Q199, Q200, Q201, Q202, Q203, Q204, Q205, Q206, Q207, Q208, Q209, Q210, Q211, Q212, Q213, Q214, Q215, Q216, Q217, Q218, Q219, Q220, Q221, Q222, Q223, Q224, Q225, Q226, Q227, Q228, Q229, Q230, Q231, Q232, Q233, Q234, Q235, Q236, Q237, Q238, Q239, Q240, Q241, Q242, Q243, Q244, Q245, Q246, Q247, Q248, Q249, Q250, Q251, Q252, Q253, Q254, Q255, Q256, Q257, Q258, Q259, Q260, Q261, Q262, Q263, Q264, Q265, Q266, Q267, Q268, Q269, Q270, Q271, Q272, Q273, Q274, Q275, Q276, Q277, Q278, Q279, Q280, Q281, Q282, Q283, Q284, Q285, Q286, Q287, Q288, Q289, Q290, Q291, Q292, Q293, Q294, Q295, Q296, Q297, Q298, Q299, Q300, Q301, Q302, Q303, Q304, Q305, Q306, Q307, Q308, Q309, Q310, Q311, Q312, Q313, Q314, Q315, Q316, Q317, Q318, Q319, Q320, Q321, Q322, Q323, Q324, Q325, Q326, Q327, Q328, Q329, Q330, Q331, Q332, Q333, Q334, Q335, Q336, Q337, Q338, Q339, Q340, Q341, Q342, Q343, Q344, Q345, Q346, Q347, Q348, Q349, Q350, Q351, Q352, Q353, Q354, Q355, Q356, Q357, Q358, Q359, Q360, Q361, Q362, Q363, Q364, Q365, Q366, Q367, Q368, Q369, Q370, Q371, Q372, Q373, Q374, Q375, Q376, Q377, Q378, Q379, Q380, Q381, Q382, Q383, Q384, Q385, Q386, Q387, Q388, Q389, Q390, Q391, Q392, Q393, Q394, Q395, Q396, Q397, Q398, Q399, Q400, Q401, Q402, Q403, Q404, Q405, Q406, Q407, Q408, Q409, Q410, Q411, Q412, Q413, Q414, Q415, Q416, Q417, Q418, Q419, Q420, Q421, Q422, Q423, Q424, Q425, Q426, Q427, Q428, Q429, Q430, Q431, Q432, Q433, Q434, Q435, Q436, Q437, Q438, Q439, Q440, Q441, Q442, Q443, Q444, Q445, Q446, Q447, Q448, Q449, Q450, Q451, Q452, Q453, Q454, Q455, Q456, Q457, Q458, Q459, Q460, Q461, Q462, Q463, Q464, Q465, Q466, Q467, Q468, Q469, Q470, Q471, Q472, Q473, Q474, Q475, Q476, Q477, Q478, Q479, Q480, Q481, Q482, Q483, Q484, Q485, Q486, Q487, Q488, Q489, Q490, Q491, Q492, Q493, Q494, Q495, Q496, Q497, Q498, Q499, Q500, Q501, Q502, Q503, Q504, Q505, Q506, Q507, Q508, Q509, Q510, Q511, Q512, Q513, Q514, Q515, Q516, Q517, Q518, Q519, Q520, Q521, Q522, Q523, Q524, Q525, Q526, Q527, Q528, Q529, Q530, Q531, Q532, Q533, Q534, Q535, Q536, Q537, Q538, Q539, Q540, Q541, Q542, Q543, Q544, Q545, Q546, Q547, Q548, Q549, Q550, Q551, Q552, Q553, Q554, Q555, Q556, Q557, Q558, Q559, Q560, Q561, Q562, Q563, Q564, Q565, Q566, Q567, Q568, Q569, Q570, Q571, Q572, Q573, Q574, Q575, Q576, Q577, Q578, Q579, Q580, Q581, Q582, Q583, Q584, Q585, Q586, Q587, Q588, Q589, Q590, Q591, Q592, Q593, Q594, Q595, Q596, Q597, Q598, Q599, Q600, Q601, Q602, Q603, Q604, Q605, Q606, Q607, Q608, Q609, Q610, Q611, Q612, Q613, Q614, Q615, Q616, Q617, Q618, Q619, Q620, Q621, Q622, Q623, Q624, Q625, Q626, Q627, Q628, Q629, Q630, Q631, Q632, Q633, Q634, Q635, Q636, Q637, Q638, Q639, Q640, Q641, Q642, Q643, Q644, Q645, Q646, Q647, Q648, Q649, Q650, Q651, Q652, Q653, Q654, Q655, Q656, Q657, Q658, Q659, Q660, Q661, Q662, Q663, Q664, Q665, Q666, Q667, Q668, Q669, Q670, Q671, Q672, Q673, Q674, Q675, Q676, Q677, Q678, Q679, Q680, Q681, Q682, Q683, Q684, Q685, Q686, Q687, Q688, Q689, Q690, Q691, Q692, Q693, Q694, Q695, Q696, Q697, Q698, Q699, Q700, Q701, Q702, Q703, Q704, Q705, Q706, Q707, Q708, Q709, Q710, Q711, Q712, Q713, Q714, Q715, Q716, Q717, Q718, Q719, Q720, Q721, Q722, Q723, Q724, Q725]), "radius" : 0.5 * mm, "tangentPropagation" : true, "allowEdgeOverflow" : false});
        }
    });
